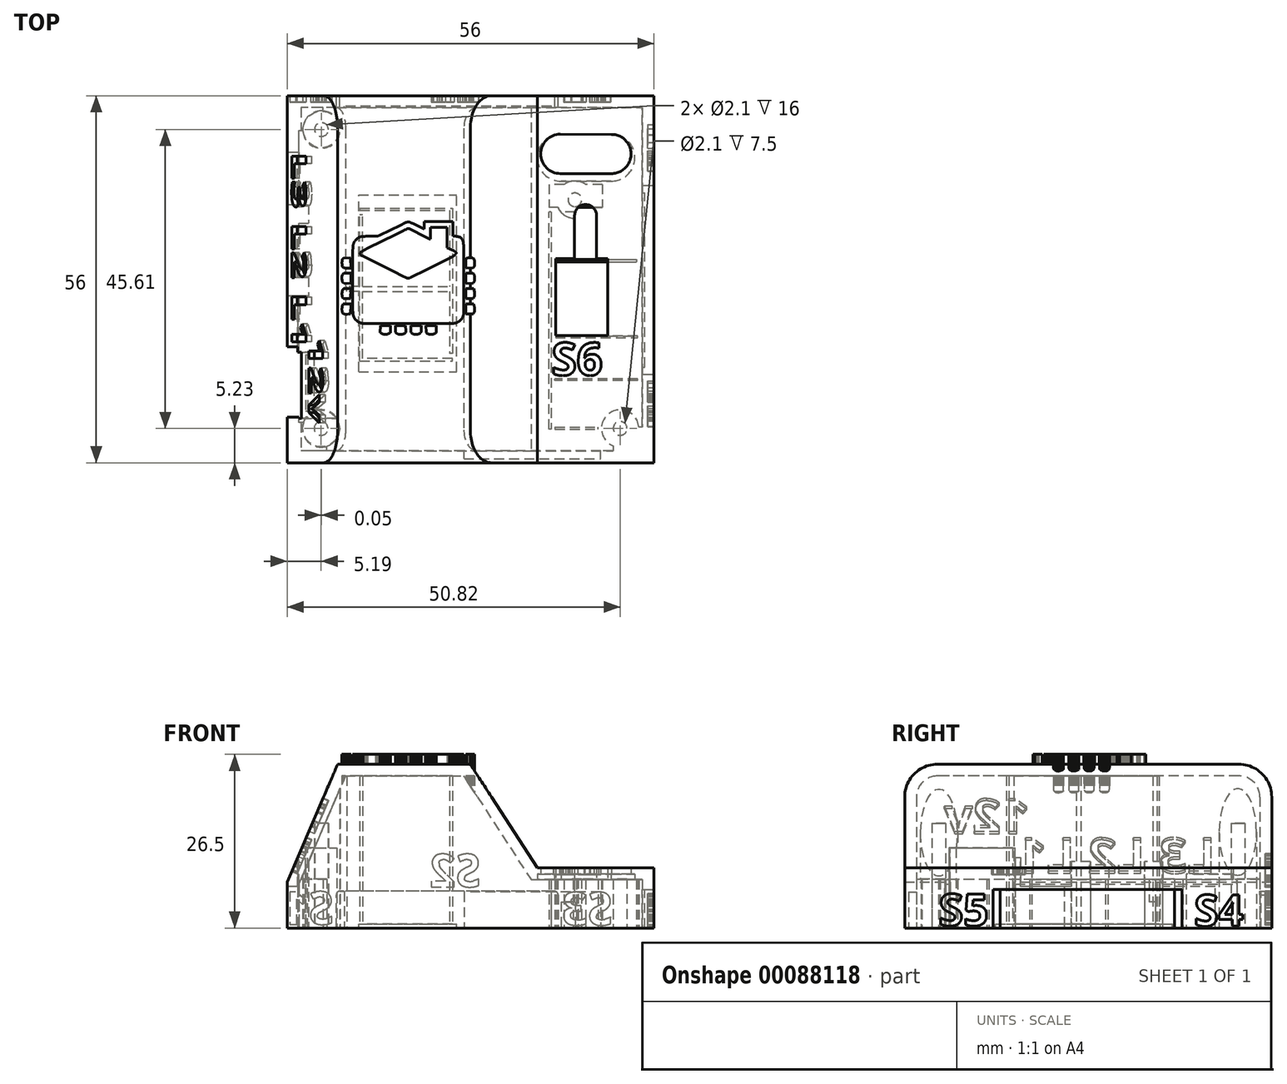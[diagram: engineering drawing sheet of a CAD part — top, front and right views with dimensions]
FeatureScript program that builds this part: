
annotation { "Feature Type Name" : "Feature", "Feature Type Description" : "" }
export const myFeature = defineFeature(function(context is Context, id is Id, definition is map)
    precondition{}
    {
        {
            var Q0;
            Q0=qCreatedBy(makeId("Top.planeOp"),FACE);
            var sketch = newSketch(context, id + "F0", { "sketchPlane" : qUnion([Q0])});
            skLineSegment(sketch, "E0.rect.bottom", {"start": v(22.84, -21.13) * mm, "end": v(-26.83, -21.13) * mm});
            skLineSegment(sketch, "E0.rect.top", {"start": v(22.84, 28.7) * mm, "end": v(-26.83, 28.7) * mm});
            skLineSegment(sketch, "E0.rect.left", {"start": v(22.84, -21.13) * mm, "end": v(22.84, 28.7) * mm});
            skPoint(sketch, "E0.rect.middle", {"position": v(-2, 3.78) * mm});
            skCircle(sketch, "E1", {"center": v(-24.81, -18.99) * mm, "radius": 1.05 * mm});
            skCircle(sketch, "E2", {"center": v(-24.76, 26.62) * mm, "radius": 1.05 * mm});
            skCircle(sketch, "E3", {"center": v(13.92, 15.91) * mm, "radius": 1.05 * mm});
            skLineSegment(sketch, "E4", {"start": v(-2, -21.13) * mm, "end": v(-2, -18.21) * mm});
            skCircle(sketch, "E5.MirrorC", {"center": v(20.82, -18.99) * mm, "radius": 1.05 * mm});
            skLineSegment(sketch, "E6.rect.bottom", {"start": v(24.75, -22.97) * mm, "end": v(-28.75, -22.97) * mm});
            skLineSegment(sketch, "E6.rect.top", {"start": v(24.75, 30.53) * mm, "end": v(-28.75, 30.53) * mm});
            skLineSegment(sketch, "E6.rect.left", {"start": v(24.75, -22.97) * mm, "end": v(24.75, 30.53) * mm});
            skLineSegment(sketch, "E6.rect.right", {"start": v(-28.75, -22.97) * mm, "end": v(-28.75, 30.53) * mm});
            skLineSegment(sketch, "E7.rect.bottom", {"start": v(26, -24.22) * mm, "end": v(-30, -24.22) * mm});
            skLineSegment(sketch, "E7.rect.top", {"start": v(26, 31.78) * mm, "end": v(-30, 31.78) * mm});
            skLineSegment(sketch, "E7.rect.left", {"start": v(26, -24.22) * mm, "end": v(26, 31.78) * mm});
            skLineSegment(sketch, "E7.rect.right", {"start": v(-30, -24.22) * mm, "end": v(-30, 31.78) * mm});
            skPoint(sketch, "E8", {"position": v(8.65, 14) * mm});
            skSolve(sketch);
        }
        {
            var Q0;
            Q0=qSketchRegion(id+"F0",true);
            var Q1;
            Q1=makeQuery(id+"F0.imprint","IMPRINT",FACE,{"disambiguationData":[TD([[makeQuery(id+"F0.imprint","IMPRINT",EDGE,{"derivedFrom":sQuery(id+"F0.wireOp",EDGE,"E1")}),-1.0]])]});
            extrude(context, id + "F1", {"entities" : qUnion([Q0, Q1]), "depth" : 25 * mm});
        }
        {
            var Q0;
            Q0=qCreatedBy(makeId("Front.planeOp"),FACE);
            var sketch = newSketch(context, id + "F2", { "sketchPlane" : qUnion([Q0])});
            skLineSegment(sketch, "E9", {"start": v(0, 0) * mm, "end": v(0, 7) * mm});
            skLineSegment(sketch, "E10", {"start": v(0, 7) * mm, "end": v(26.03, 7) * mm});
            skLineSegment(sketch, "E11", {"start": v(26.03, 9.19) * mm, "end": v(26.03, 25.51) * mm});
            skLineSegment(sketch, "E12", {"start": v(15.3, 7) * mm, "end": v(26.03, 7) * mm});
            skLineSegment(sketch, "E13", {"start": v(0, 7) * mm, "end": v(-30.02, 7) * mm});
            skLineSegment(sketch, "E14", {"start": v(-30.02, 7) * mm, "end": v(-22.06, 25.51) * mm});
            skLineSegment(sketch, "E15", {"start": v(-22.06, 25.51) * mm, "end": v(-2.39, 25.51) * mm});
            skLineSegment(sketch, "E16", {"start": v(26.03, 25.51) * mm, "end": v(-2.39, 25.51) * mm});
            skLineSegment(sketch, "E17", {"start": v(-22.06, 25.51) * mm, "end": v(-30.02, 25.51) * mm});
            skLineSegment(sketch, "E18", {"start": v(-30.02, 25.51) * mm, "end": v(-30.02, 7) * mm});
            skLineSegment(sketch, "E19", {"start": v(18.06, 10.7) * mm, "end": v(18.04, 10.7) * mm});
            skLineSegment(sketch, "E20", {"start": v(19.86, 9.19) * mm, "end": v(8.2, 9.19) * mm});
            skLineSegment(sketch, "E21", {"start": v(8.2, 9.19) * mm, "end": v(-2.39, 25.51) * mm});
            skLineSegment(sketch, "E22", {"start": v(19.86, 9.19) * mm, "end": v(26.03, 9.19) * mm});
            skSolve(sketch);
        }
        {
            var Q0;
            Q0=makeQuery(id+"F2.imprint","IMPRINT",FACE,{"disambiguationData":[TD([[makeQuery(id+"F2.imprint","IMPRINT",EDGE,{"derivedFrom":sQuery(id+"F2.wireOp",EDGE,"E14")}),1.0]])]});
            var Q1;
            {var subQ0=sQuery(id+"F2.wireOp",EDGE,"E11");Q1=makeQuery(id+"F2.imprint","IMPRINT",FACE,{"disambiguationData":[TD([[makeQuery(id+"F2.imprint","IMPRINT",EDGE,{"derivedFrom":subQ0}),1.0]])]});}
            extrude(context, id + "F3", {"entities" : qUnion([Q0, Q1]), "operationType" : NewBodyOperationType.REMOVE, "endBound" : BoundingType.UP_TO_NEXT, "oppositeDirection" : true, "depth" : 25 * mm, "hasSecondDirection" : true, "secondDirectionOppositeDirection" : false, "secondDirectionDepth" : 25 * mm});
        }
        {
            var Q0;
            Q0=makeQuery(id+"F1.opExtrude","CAP_EDGE",EDGE,{"disambiguationData":[OSD([sQuery(id+"F0.wireOp",EDGE,"E7.rect.right")])],"isStart":false});
            var Q1;
            Q1=makeQuery(id+"F3.boolean.opBoolean","COPY",EDGE,{"derivedFrom":makeQuery(id+"F3.opExtrude","TWEAK_EDGE",EDGE,{"derivedFrom":[makeQuery(id+"F1.opExtrude","CAP_FACE",FACE,{"disambiguationData":[OSD([sQuery(id+"F0.wireOp",EDGE,"E1"),sQuery(id+"F0.wireOp",EDGE,"E2"),sQuery(id+"F0.wireOp",EDGE,"E3"),sQuery(id+"F0.wireOp",EDGE,"E5.MirrorC"),sQuery(id+"F0.wireOp",EDGE,"E7.rect.bottom"),sQuery(id+"F0.wireOp",EDGE,"E7.rect.top"),sQuery(id+"F0.wireOp",EDGE,"E7.rect.left"),sQuery(id+"F0.wireOp",EDGE,"E7.rect.right")])],"isStart":false}),makeQuery(id+"F2.imprint","IMPRINT",EDGE,{"derivedFrom":sQuery(id+"F2.wireOp",EDGE,"ff17f17f-c23f-4b7b-92e3-773d52701edb")})]})});
            var Q2;
            Q2=makeQuery(id+"F3.boolean.opBoolean","COPY",EDGE,{"derivedFrom":makeQuery(id+"F3.opExtrude","TWEAK_EDGE",EDGE,{"derivedFrom":[makeQuery(id+"F1.opExtrude","CAP_FACE",FACE,{"disambiguationData":[OSD([sQuery(id+"F0.wireOp",EDGE,"E1"),sQuery(id+"F0.wireOp",EDGE,"E2"),sQuery(id+"F0.wireOp",EDGE,"E3"),sQuery(id+"F0.wireOp",EDGE,"E5.MirrorC"),sQuery(id+"F0.wireOp",EDGE,"E7.rect.bottom"),sQuery(id+"F0.wireOp",EDGE,"E7.rect.top"),sQuery(id+"F0.wireOp",EDGE,"E7.rect.left"),sQuery(id+"F0.wireOp",EDGE,"E7.rect.right")])],"isStart":false}),makeQuery(id+"F2.imprint","IMPRINT",EDGE,{"derivedFrom":sQuery(id+"F2.wireOp",EDGE,"7c30f75c-de24-4105-9ec6-0528e7197d9e")})]})});
            var Q3;
            {var subQ0=sQuery(id+"F2.wireOp",EDGE,"cpQ2IQLn-lepx-jHqE-Occg-QwCyzWVKbBFz");var subQ1=sQuery(id+"F2.wireOp",EDGE,"9136473a-ce9f-4df1-8e41-d79c079f6f02");var subQ2=makeQuery(id+"F2.imprint","INTERSECT",VERTEX,{"disambiguationData":[OD(0.0)],"derivedFrom":[subQ1,subQ0]});var subQ4=makeQuery(id+"F2.imprint","INTERSECT",VERTEX,{"disambiguationData":[OD(1.0)],"derivedFrom":[subQ1,subQ0]});Q3=makeQuery(id+"F3.boolean.opBoolean","COPY",EDGE,{"derivedFrom":makeQuery(id+"F3.opExtrude","TWEAK_EDGE",EDGE,{"derivedFrom":[makeQuery(id+"F1.opExtrude","CAP_FACE",FACE,{"disambiguationData":[OSD([sQuery(id+"F0.wireOp",EDGE,"E1"),sQuery(id+"F0.wireOp",EDGE,"E2"),sQuery(id+"F0.wireOp",EDGE,"E3"),sQuery(id+"F0.wireOp",EDGE,"E5.MirrorC"),sQuery(id+"F0.wireOp",EDGE,"E7.rect.bottom"),sQuery(id+"F0.wireOp",EDGE,"E7.rect.top"),sQuery(id+"F0.wireOp",EDGE,"E7.rect.left"),sQuery(id+"F0.wireOp",EDGE,"E7.rect.right")])],"isStart":false}),makeQuery(id+"F2.imprint","IMPRINT",EDGE,{"disambiguationData":[TD([[subQ4,1.0]])],"derivedFrom":subQ0}),makeQuery(id+"F2.imprint","IMPRINT",EDGE,{"disambiguationData":[TD([[subQ2,1.0]])],"derivedFrom":subQ0}),makeQuery(id+"F2.imprint","IMPRINT",EDGE,{"disambiguationData":[TD([[subQ2,-1.0]])],"derivedFrom":subQ0})]})});}
            var Q4;
            {var subQ0=sQuery(id+"F2.wireOp",EDGE,"cpQ2IQLn-lepx-jHqE-Occg-QwCyzWVKbBFz");var subQ1=sQuery(id+"F2.wireOp",EDGE,"9136473a-ce9f-4df1-8e41-d79c079f6f02");var subQ2=makeQuery(id+"F2.imprint","INTERSECT",VERTEX,{"disambiguationData":[OD(0.0)],"derivedFrom":[subQ1,subQ0]});var subQ3=sQuery(id+"F2.wireOp",EDGE,"7c30f75c-de24-4105-9ec6-0528e7197d9e");var subQ4=makeQuery(id+"F2.imprint","INTERSECT",VERTEX,{"derivedFrom":[subQ3,subQ0]});var subQ5=makeQuery(id+"F2.imprint","INTERSECT",VERTEX,{"disambiguationData":[OD(1.0)],"derivedFrom":[subQ1,subQ0]});Q4=makeQuery(id+"F3.boolean.opBoolean","COPY",EDGE,{"derivedFrom":makeQuery(id+"F3.opExtrude","TWEAK_EDGE",EDGE,{"disambiguationData":[OD(0.0)],"derivedFrom":[makeQuery(id+"F2.imprint","IMPRINT",EDGE,{"disambiguationData":[TD([[subQ4,1.0]])],"derivedFrom":subQ3}),makeQuery(id+"F2.imprint","IMPRINT",EDGE,{"disambiguationData":[TD([[subQ5,1.0]])],"derivedFrom":subQ0}),makeQuery(id+"F2.imprint","IMPRINT",EDGE,{"disambiguationData":[TD([[subQ2,1.0]])],"derivedFrom":subQ0}),makeQuery(id+"F2.imprint","IMPRINT",EDGE,{"disambiguationData":[TD([[subQ2,-1.0]])],"derivedFrom":subQ0})]})});}
            var Q5;
            {var subQ0=sQuery(id+"F2.wireOp",EDGE,"cpQ2IQLn-lepx-jHqE-Occg-QwCyzWVKbBFz");var subQ1=sQuery(id+"F2.wireOp",EDGE,"9136473a-ce9f-4df1-8e41-d79c079f6f02");var subQ2=makeQuery(id+"F2.imprint","INTERSECT",VERTEX,{"disambiguationData":[OD(0.0)],"derivedFrom":[subQ1,subQ0]});var subQ3=sQuery(id+"F2.wireOp",EDGE,"7c30f75c-de24-4105-9ec6-0528e7197d9e");var subQ4=makeQuery(id+"F2.imprint","INTERSECT",VERTEX,{"derivedFrom":[subQ3,subQ0]});var subQ5=makeQuery(id+"F2.imprint","INTERSECT",VERTEX,{"disambiguationData":[OD(1.0)],"derivedFrom":[subQ1,subQ0]});Q5=makeQuery(id+"F3.boolean.opBoolean","COPY",EDGE,{"derivedFrom":makeQuery(id+"F3.opExtrude","TWEAK_EDGE",EDGE,{"disambiguationData":[OD(1.0)],"derivedFrom":[makeQuery(id+"F2.imprint","IMPRINT",EDGE,{"disambiguationData":[TD([[subQ4,1.0]])],"derivedFrom":subQ3}),makeQuery(id+"F2.imprint","IMPRINT",EDGE,{"disambiguationData":[TD([[subQ5,1.0]])],"derivedFrom":subQ0}),makeQuery(id+"F2.imprint","IMPRINT",EDGE,{"disambiguationData":[TD([[subQ2,1.0]])],"derivedFrom":subQ0}),makeQuery(id+"F2.imprint","IMPRINT",EDGE,{"disambiguationData":[TD([[subQ2,-1.0]])],"derivedFrom":subQ0})]})});}
            var Q6;
            Q6=makeQuery(id+"F1.opExtrude","CAP_EDGE",EDGE,{"disambiguationData":[OSD([sQuery(id+"F0.wireOp",EDGE,"E7.rect.bottom")])],"isStart":false});
            var Q7;
            {var subQ0=sQuery(id+"F2.wireOp",EDGE,"cpQ2IQLn-lepx-jHqE-Occg-QwCyzWVKbBFz");var subQ1=sQuery(id+"F2.wireOp",EDGE,"9136473a-ce9f-4df1-8e41-d79c079f6f02");var subQ2=makeQuery(id+"F2.imprint","INTERSECT",VERTEX,{"disambiguationData":[OD(0.0)],"derivedFrom":[subQ1,subQ0]});var subQ4=makeQuery(id+"F2.imprint","INTERSECT",VERTEX,{"disambiguationData":[OD(1.0)],"derivedFrom":[subQ1,subQ0]});Q7=makeQuery(id+"F3.boolean.opBoolean","COPY",EDGE,{"derivedFrom":makeQuery(id+"F3.opExtrude","TWEAK_EDGE",EDGE,{"derivedFrom":[makeQuery(id+"F1.opExtrude","SWEPT_FACE",FACE,{"disambiguationData":[OSD([sQuery(id+"F0.wireOp",EDGE,"E7.rect.bottom")])]}),makeQuery(id+"F2.imprint","IMPRINT",EDGE,{"disambiguationData":[TD([[subQ4,1.0]])],"derivedFrom":subQ0}),makeQuery(id+"F2.imprint","IMPRINT",EDGE,{"disambiguationData":[TD([[subQ2,1.0]])],"derivedFrom":subQ0}),makeQuery(id+"F2.imprint","IMPRINT",EDGE,{"disambiguationData":[TD([[subQ2,-1.0]])],"derivedFrom":subQ0})]})});}
            var Q8;
            Q8=makeQuery(id+"F1.opExtrude","CAP_EDGE",EDGE,{"disambiguationData":[OSD([sQuery(id+"F0.wireOp",EDGE,"E7.rect.top")])],"isStart":false});
            var Q9;
            {var subQ0=sQuery(id+"F2.wireOp",EDGE,"cpQ2IQLn-lepx-jHqE-Occg-QwCyzWVKbBFz");var subQ1=sQuery(id+"F2.wireOp",EDGE,"9136473a-ce9f-4df1-8e41-d79c079f6f02");var subQ2=makeQuery(id+"F2.imprint","INTERSECT",VERTEX,{"disambiguationData":[OD(0.0)],"derivedFrom":[subQ1,subQ0]});var subQ4=makeQuery(id+"F2.imprint","INTERSECT",VERTEX,{"disambiguationData":[OD(1.0)],"derivedFrom":[subQ1,subQ0]});Q9=makeQuery(id+"F3.boolean.opBoolean","COPY",EDGE,{"derivedFrom":makeQuery(id+"F3.opExtrude","TWEAK_EDGE",EDGE,{"derivedFrom":[makeQuery(id+"F1.opExtrude","SWEPT_FACE",FACE,{"disambiguationData":[OSD([sQuery(id+"F0.wireOp",EDGE,"E7.rect.top")])]}),makeQuery(id+"F2.imprint","IMPRINT",EDGE,{"disambiguationData":[TD([[subQ4,1.0]])],"derivedFrom":subQ0}),makeQuery(id+"F2.imprint","IMPRINT",EDGE,{"disambiguationData":[TD([[subQ2,1.0]])],"derivedFrom":subQ0}),makeQuery(id+"F2.imprint","IMPRINT",EDGE,{"disambiguationData":[TD([[subQ2,-1.0]])],"derivedFrom":subQ0})]})});}
            var Q10;
            Q10=makeQuery(id+"F3.boolean.opBoolean","COPY",EDGE,{"derivedFrom":makeQuery(id+"F3.opExtrude","TWEAK_EDGE",EDGE,{"derivedFrom":[makeQuery(id+"F1.opExtrude","CAP_FACE",FACE,{"disambiguationData":[OSD([sQuery(id+"F0.wireOp",EDGE,"E1"),sQuery(id+"F0.wireOp",EDGE,"E2"),sQuery(id+"F0.wireOp",EDGE,"E3"),sQuery(id+"F0.wireOp",EDGE,"E5.MirrorC"),sQuery(id+"F0.wireOp",EDGE,"E7.rect.bottom"),sQuery(id+"F0.wireOp",EDGE,"E7.rect.top"),sQuery(id+"F0.wireOp",EDGE,"E7.rect.left"),sQuery(id+"F0.wireOp",EDGE,"E7.rect.right")])],"isStart":false}),makeQuery(id+"F2.imprint","IMPRINT",EDGE,{"derivedFrom":sQuery(id+"F2.wireOp",EDGE,"99fa5713-44e2-4710-8a3e-a5a5802f03ed")})]})});
            var Q11;
            Q11=makeQuery(id+"F3.boolean.opBoolean","COPY",EDGE,{"derivedFrom":makeQuery(id+"F3.opExtrude","TWEAK_EDGE",EDGE,{"derivedFrom":[makeQuery(id+"F1.opExtrude","CAP_FACE",FACE,{"disambiguationData":[OSD([sQuery(id+"F0.wireOp",EDGE,"E1"),sQuery(id+"F0.wireOp",EDGE,"E2"),sQuery(id+"F0.wireOp",EDGE,"E3"),sQuery(id+"F0.wireOp",EDGE,"E5.MirrorC"),sQuery(id+"F0.wireOp",EDGE,"E7.rect.bottom"),sQuery(id+"F0.wireOp",EDGE,"E7.rect.top"),sQuery(id+"F0.wireOp",EDGE,"E7.rect.left"),sQuery(id+"F0.wireOp",EDGE,"E7.rect.right")])],"isStart":false}),makeQuery(id+"F2.imprint","IMPRINT",EDGE,{"derivedFrom":sQuery(id+"F2.wireOp",EDGE,"E14")})]})});
            var Q12;
            Q12=makeQuery(id+"F3.boolean.opBoolean","COPY",EDGE,{"derivedFrom":makeQuery(id+"F3.opExtrude","TWEAK_EDGE",EDGE,{"derivedFrom":[makeQuery(id+"F1.opExtrude","CAP_FACE",FACE,{"disambiguationData":[OSD([sQuery(id+"F0.wireOp",EDGE,"E1"),sQuery(id+"F0.wireOp",EDGE,"E2"),sQuery(id+"F0.wireOp",EDGE,"E3"),sQuery(id+"F0.wireOp",EDGE,"E5.MirrorC"),sQuery(id+"F0.wireOp",EDGE,"E7.rect.bottom"),sQuery(id+"F0.wireOp",EDGE,"E7.rect.top"),sQuery(id+"F0.wireOp",EDGE,"E7.rect.left"),sQuery(id+"F0.wireOp",EDGE,"E7.rect.right")])],"isStart":false}),makeQuery(id+"F2.imprint","IMPRINT",EDGE,{"derivedFrom":sQuery(id+"F2.wireOp",EDGE,"E21")})]})});
            var Q13;
            Q13=makeQuery(id+"F3.boolean.opBoolean","COPY",EDGE,{"derivedFrom":makeQuery(id+"F3.opExtrude","TWEAK_EDGE",EDGE,{"derivedFrom":[makeQuery(id+"F2.imprint","IMPRINT",EDGE,{"derivedFrom":sQuery(id+"F2.wireOp",EDGE,"E20")}),makeQuery(id+"F2.imprint","IMPRINT",EDGE,{"derivedFrom":sQuery(id+"F2.wireOp",EDGE,"E21")})]})});
            var Q14;
            Q14=makeQuery(id+"F3.boolean.opBoolean","COPY",EDGE,{"derivedFrom":makeQuery(id+"F3.opExtrude","TWEAK_EDGE",EDGE,{"derivedFrom":[makeQuery(id+"F1.opExtrude","SWEPT_FACE",FACE,{"disambiguationData":[OSD([sQuery(id+"F0.wireOp",EDGE,"E7.rect.bottom")])]}),makeQuery(id+"F2.imprint","IMPRINT",EDGE,{"derivedFrom":sQuery(id+"F2.wireOp",EDGE,"E21")})]})});
            var Q15;
            Q15=makeQuery(id+"F3.boolean.opBoolean","COPY",EDGE,{"derivedFrom":makeQuery(id+"F3.opExtrude","TWEAK_EDGE",EDGE,{"derivedFrom":[makeQuery(id+"F1.opExtrude","SWEPT_FACE",FACE,{"disambiguationData":[OSD([sQuery(id+"F0.wireOp",EDGE,"E7.rect.top")])]}),makeQuery(id+"F2.imprint","IMPRINT",EDGE,{"derivedFrom":sQuery(id+"F2.wireOp",EDGE,"E21")})]})});
            var Q16;
            Q16=makeQuery(id+"F3.boolean.opBoolean","COPY",EDGE,{"derivedFrom":makeQuery(id+"F3.opExtrude","TWEAK_EDGE",EDGE,{"derivedFrom":[makeQuery(id+"F1.opExtrude","SWEPT_FACE",FACE,{"disambiguationData":[OSD([sQuery(id+"F0.wireOp",EDGE,"E7.rect.left")])]}),makeQuery(id+"F2.imprint","IMPRINT",EDGE,{"derivedFrom":sQuery(id+"F2.wireOp",EDGE,"E20")}),makeQuery(id+"F2.imprint","IMPRINT",EDGE,{"derivedFrom":sQuery(id+"F2.wireOp",EDGE,"E22")})]})});
            var Q17;
            Q17=makeQuery(id+"F3.boolean.opBoolean","COPY",EDGE,{"derivedFrom":makeQuery(id+"F3.opExtrude","TWEAK_EDGE",EDGE,{"derivedFrom":[makeQuery(id+"F2.imprint","IMPRINT",EDGE,{"derivedFrom":sQuery(id+"F2.wireOp",EDGE,"E20")}),makeQuery(id+"F2.imprint","IMPRINT",EDGE,{"derivedFrom":sQuery(id+"F2.wireOp",EDGE,"E21")}),makeQuery(id+"F2.imprint","IMPRINT",EDGE,{"derivedFrom":sQuery(id+"F2.wireOp",EDGE,"E22")})]})});
            fillet(context, id + "F4", {"entities" : qUnion([Q0, Q1, Q2, Q3, Q4, Q5, Q6, Q7, Q8, Q9, Q10, Q11, Q12, Q13, Q14, Q15, Q16, Q17]), "radius" : 5 * mm, "tangentPropagation" : true, "allowEdgeOverflow" : false});
        }
        {
            var Q0;
            Q0=makeQuery(id+"F1.opExtrude","SWEPT_BODY",BODY,{"disambiguationData":[OSD([sQuery(id+"F0.wireOp",EDGE,"E1"),sQuery(id+"F0.wireOp",EDGE,"E2"),sQuery(id+"F0.wireOp",EDGE,"E3"),sQuery(id+"F0.wireOp",EDGE,"E5.MirrorC"),sQuery(id+"F0.wireOp",EDGE,"E7.rect.bottom"),sQuery(id+"F0.wireOp",EDGE,"E7.rect.top"),sQuery(id+"F0.wireOp",EDGE,"E7.rect.left"),sQuery(id+"F0.wireOp",EDGE,"E7.rect.right")])]});
            transform(context, id + "F5", {"entities" : qUnion([Q0]), "transformType" : TransformType.TRANSLATION_3D, "dx" : -5 * mm, "dy" : -12 * mm, "dz" : 0 * mm, "makeCopy" : false});
        }
        {
            var Q0;
            Q0=makeQuery(id+"F1.opExtrude","CAP_FACE",FACE,{"disambiguationData":[OSD([sQuery(id+"F0.wireOp",EDGE,"E1"),sQuery(id+"F0.wireOp",EDGE,"E2"),sQuery(id+"F0.wireOp",EDGE,"E3"),sQuery(id+"F0.wireOp",EDGE,"E5.MirrorC"),sQuery(id+"F0.wireOp",EDGE,"E7.rect.bottom"),sQuery(id+"F0.wireOp",EDGE,"E7.rect.top"),sQuery(id+"F0.wireOp",EDGE,"E7.rect.left"),sQuery(id+"F0.wireOp",EDGE,"E7.rect.right")])],"isStart":true});
            shell(context, id + "F6", {"entities" : qUnion([Q0]), "thickness" : 1.8 * mm});
        }
        {
            var Q0;
            Q0=makeQuery(id+"F1.opExtrude","SWEPT_FACE",FACE,{"disambiguationData":[OSD([sQuery(id+"F0.wireOp",EDGE,"E7.rect.left")])]});
            cPlane(context, id + "F7", {"entities" : qUnion([Q0]), "cplaneType" : CPlaneType.OFFSET, "offset" : 0 * mm, "width" : 150 * mm, "height" : 150 * mm});
        }
        {
            var Q0;
            Q0=qCreatedBy(id+"F7.planeOp",FACE);
            var sketch = newSketch(context, id + "F8", { "sketchPlane" : qUnion([Q0])});
            skLineSegment(sketch, "E23.bottom", {"start": v(6.92, 0) * mm, "end": v(-20.2, 0) * mm});
            skLineSegment(sketch, "E23.top", {"start": v(6.12, 5.87) * mm, "end": v(-20.2, 5.87) * mm});
            skLineSegment(sketch, "E24", {"start": v(-20.2, 5.87) * mm, "end": v(-21.64, 5.87) * mm});
            skLineSegment(sketch, "E25", {"start": v(-21.64, 5.87) * mm, "end": v(-21.64, 0) * mm});
            skLineSegment(sketch, "E26", {"start": v(-21.64, 0) * mm, "end": v(-20.2, 0) * mm});
            skLineSegment(sketch, "E27", {"start": v(6.12, 5.87) * mm, "end": v(6.12, 0) * mm});
            skPoint(sketch, "E28.orphan", {"position": v(7.84, 0) * mm});
            skLineSegment(sketch, "E29", {"start": v(4.97, 0) * mm, "end": v(4.97, 5.87) * mm});
            skLineSegment(sketch, "E30", {"start": v(-21.64, 5.87) * mm, "end": v(-22.73, 5.87) * mm});
            skLineSegment(sketch, "E31", {"start": v(-22.73, 5.87) * mm, "end": v(-22.73, 0) * mm});
            skLineSegment(sketch, "E32", {"start": v(-22.73, 0) * mm, "end": v(-21.64, 0) * mm});
            skSolve(sketch);
        }
        {
            var Q0;
            {var subQ1=sQuery(id+"F8.wireOp",EDGE,"E24");Q0=makeQuery(id+"F8.imprint","IMPRINT",FACE,{"disambiguationData":[TD([[makeQuery(id+"F8.imprint","IMPRINT",EDGE,{"derivedFrom":subQ1}),1.0]])]});}
            extrude(context, id + "F9", {"entities" : qUnion([Q0]), "operationType" : NewBodyOperationType.REMOVE, "oppositeDirection" : true, "depth" : (1.7 - 0.3) * mm});
        }
        {
            var Q0;
            Q0=makeQuery(id+"F8.imprint","IMPRINT",FACE,{"disambiguationData":[TD([[makeQuery(id+"F8.imprint","IMPRINT",EDGE,{"derivedFrom":sQuery(id+"F8.wireOp",EDGE,"E25")}),-1.0]])]});
            var Q1;
            {var subQ0=sQuery(id+"F8.wireOp",EDGE,"E27");Q1=makeQuery(id+"F8.imprint","IMPRINT",FACE,{"disambiguationData":[TD([[makeQuery(id+"F8.imprint","IMPRINT",EDGE,{"derivedFrom":subQ0}),-1.0]])]});}
            extrude(context, id + "F10", {"entities" : qUnion([Q0, Q1]), "operationType" : NewBodyOperationType.REMOVE, "oppositeDirection" : true, "depth" : 2 * mm});
        }
        {
            var Q0;
            Q0=makeQuery(id+"F1.opExtrude","SWEPT_FACE",FACE,{"disambiguationData":[OSD([sQuery(id+"F0.wireOp",EDGE,"E7.rect.right")])]});
            cPlane(context, id + "F11", {"entities" : qUnion([Q0]), "cplaneType" : CPlaneType.OFFSET, "offset" : 0 * mm, "width" : 150 * mm, "height" : 150 * mm});
        }
        {
            var Q0;
            Q0=qCreatedBy(id+"F11.planeOp",FACE);
            var sketch = newSketch(context, id + "F12", { "sketchPlane" : qUnion([Q0])});
            skLineSegment(sketch, "E33.top", {"start": v(-11.15, 6.31) * mm, "end": v(-3.45, 6.31) * mm});
            skLineSegment(sketch, "E34", {"start": v(27.25, 11.15) * mm, "end": v(27.25, 11.15) * mm});
            skLineSegment(sketch, "E35", {"start": v(-11.15, 0) * mm, "end": v(-11.15, 6.31) * mm});
            skPoint(sketch, "E36.start.orphan", {"position": v(-15.15, 0) * mm});
            skLineSegment(sketch, "E37", {"start": v(29.28, 0) * mm, "end": v(-11.15, 0) * mm});
            skLineSegment(sketch, "E38", {"start": v(-10.29, 6.31) * mm, "end": v(-10.29, 0) * mm});
            skLineSegment(sketch, "E39", {"start": v(19.35, 12.2) * mm, "end": v(29.28, 12.2) * mm});
            skLineSegment(sketch, "E40", {"start": v(-11.15, 3.16) * mm, "end": v(-3.45, 3.16) * mm, "construction": true});
            skLineSegment(sketch, "E41", {"start": v(-3.45, 3.16) * mm, "end": v(-0.05, 3.16) * mm, "construction": true});
            skLineSegment(sketch, "E42", {"start": v(-0.05, 3.16) * mm, "end": v(7.65, 3.16) * mm, "construction": true});
            skLineSegment(sketch, "E43", {"start": v(7.65, 3.16) * mm, "end": v(11.05, 3.16) * mm, "construction": true});
            skLineSegment(sketch, "E44.trimOffspring", {"start": v(11.05, 6.31) * mm, "end": v(18.53, 6.31) * mm});
            skLineSegment(sketch, "E45", {"start": v(11.9, 6.31) * mm, "end": v(11.9, 0) * mm});
            skLineSegment(sketch, "E46", {"start": v(0, 6.31) * mm, "end": v(7.65, 6.31) * mm});
            skLineSegment(sketch, "E47", {"start": v(7.65, 0) * mm, "end": v(0, 0) * mm});
            skLineSegment(sketch, "E48", {"start": v(-3.45, 0) * mm, "end": v(-11.15, 0) * mm});
            skLineSegment(sketch, "E49", {"start": v(30.08, 0) * mm, "end": v(11.05, 0) * mm});
            skLineSegment(sketch, "E50.bottom", {"start": v(-0.32, 0) * mm, "end": v(-3.15, 0) * mm});
            skLineSegment(sketch, "E50.top", {"start": v(-0.32, 6.31) * mm, "end": v(-3.15, 6.31) * mm});
            skLineSegment(sketch, "E50.left", {"start": v(-0.32, 0) * mm, "end": v(-0.32, 6.31) * mm});
            skLineSegment(sketch, "E50.right", {"start": v(-3.15, 0) * mm, "end": v(-3.15, 6.31) * mm});
            skLineSegment(sketch, "E51.bottom", {"start": v(10.8, 0) * mm, "end": v(7.92, 0) * mm});
            skLineSegment(sketch, "E51.top", {"start": v(10.8, 6.31) * mm, "end": v(7.92, 6.31) * mm});
            skLineSegment(sketch, "E51.left", {"start": v(10.8, 0) * mm, "end": v(10.8, 6.31) * mm});
            skLineSegment(sketch, "E51.right", {"start": v(7.92, 0) * mm, "end": v(7.92, 6.31) * mm});
            skLineSegment(sketch, "E52", {"start": v(-3.45, 6.31) * mm, "end": v(11.05, 6.31) * mm});
            skLineSegment(sketch, "E53", {"start": v(29.28, 12.2) * mm, "end": v(29.28, 0) * mm});
            skPoint(sketch, "E54.end.orphan", {"position": v(30.08, 11.15) * mm});
            skPoint(sketch, "E54.start.orphan", {"position": v(30.08, 12.2) * mm});
            skLineSegment(sketch, "E55", {"start": v(18.53, 6.31) * mm, "end": v(18.53, 12.2) * mm});
            skLineSegment(sketch, "E56", {"start": v(18.53, 12.2) * mm, "end": v(19.35, 12.2) * mm});
            skPoint(sketch, "E57.start.orphan", {"position": v(19.35, 11.15) * mm});
            skPoint(sketch, "E58.end.orphan", {"position": v(19.35, 0) * mm});
            skPoint(sketch, "E58.start.orphan", {"position": v(19.35, 6.31) * mm});
            skLineSegment(sketch, "E59", {"start": v(28.38, 0) * mm, "end": v(28.38, 12.2) * mm});
            skLineSegment(sketch, "E60", {"start": v(19.35, 12.2) * mm, "end": v(19.35, 0) * mm});
            skSolve(sketch);
        }
        {
            var Q0;
            {var subQ0=sQuery(id+"F12.wireOp",EDGE,"E35");Q0=makeQuery(id+"F12.imprint","IMPRINT",FACE,{"disambiguationData":[TD([[makeQuery(id+"F12.imprint","IMPRINT",EDGE,{"derivedFrom":subQ0}),-1.0]])]});}
            var Q1;
            {var subQ1=sQuery(id+"F12.wireOp",EDGE,"E38");Q1=makeQuery(id+"F12.imprint","IMPRINT",FACE,{"disambiguationData":[TD([[makeQuery(id+"F12.imprint","IMPRINT",EDGE,{"derivedFrom":subQ1}),1.0]])]});}
            var Q2;
            {var subQ0=sQuery(id+"F12.wireOp",EDGE,"LVVauTd6-uSLQ-SWm0-nvuu-HrEgJgk2loCY");Q2=makeQuery(id+"F12.imprint","IMPRINT",FACE,{"disambiguationData":[TD([[makeQuery(id+"F12.imprint","IMPRINT",EDGE,{"derivedFrom":subQ0}),-1.0]])]});}
            var Q3;
            Q3=makeQuery(id+"F12.imprint","IMPRINT",FACE,{"disambiguationData":[TD([[makeQuery(id+"F12.imprint","IMPRINT",EDGE,{"derivedFrom":sQuery(id+"F12.wireOp",EDGE,"Bzj0w9RH-aYdH-ZF7y-Z4mK-Pif1xP8myCSu")}),1.0]])]});
            var Q4;
            {var subQ2=sQuery(id+"F12.wireOp",EDGE,"E45");Q4=makeQuery(id+"F12.imprint","IMPRINT",FACE,{"disambiguationData":[TD([[makeQuery(id+"F12.imprint","IMPRINT",EDGE,{"derivedFrom":subQ2}),1.0]])]});}
            extrude(context, id + "F13", {"entities" : qUnion([Q0, Q1, Q2, Q3, Q4]), "operationType" : NewBodyOperationType.REMOVE, "oppositeDirection" : true, "depth" : 1.6 * mm});
        }
        {
            var Q0;
            {var subQ2=sQuery(id+"F12.wireOp",EDGE,"E59");Q0=makeQuery(id+"F12.imprint","IMPRINT",FACE,{"disambiguationData":[TD([[makeQuery(id+"F12.imprint","IMPRINT",EDGE,{"derivedFrom":subQ2}),1.0]])]});}
            var Q1;
            {var subQ0=sQuery(id+"F12.wireOp",EDGE,"E35");Q1=makeQuery(id+"F12.imprint","IMPRINT",FACE,{"disambiguationData":[TD([[makeQuery(id+"F12.imprint","IMPRINT",EDGE,{"derivedFrom":subQ0}),-1.0]])]});}
            var Q2;
            {var subQ1=sQuery(id+"F12.wireOp",EDGE,"E47");Q2=makeQuery(id+"F12.imprint","IMPRINT",FACE,{"disambiguationData":[TD([[makeQuery(id+"F12.imprint","IMPRINT",EDGE,{"derivedFrom":subQ1}),-1.0]])]});}
            var Q3;
            {var subQ3=sQuery(id+"F12.wireOp",EDGE,"E38");Q3=makeQuery(id+"F12.imprint","IMPRINT",FACE,{"disambiguationData":[TD([[makeQuery(id+"F12.imprint","IMPRINT",EDGE,{"derivedFrom":subQ3}),1.0]])]});}
            var Q4;
            {var subQ3=sQuery(id+"F12.wireOp",EDGE,"E45");Q4=makeQuery(id+"F12.imprint","IMPRINT",FACE,{"disambiguationData":[TD([[makeQuery(id+"F12.imprint","IMPRINT",EDGE,{"derivedFrom":subQ3}),-1.0]])]});}
            var Q5;
            {var subQ0=sQuery(id+"F12.wireOp",EDGE,"E53");Q5=makeQuery(id+"F12.imprint","IMPRINT",FACE,{"disambiguationData":[TD([[makeQuery(id+"F12.imprint","IMPRINT",EDGE,{"derivedFrom":subQ0}),-1.0]])]});}
            extrude(context, id + "F14", {"entities" : qUnion([Q0, Q1, Q2, Q3, Q4, Q5]), "operationType" : NewBodyOperationType.REMOVE, "oppositeDirection" : true, "depth" : 8 * mm});
        }
        {
            var Q0;
            Q0=qCreatedBy(makeId("Top.planeOp"),FACE);
            var sketch = newSketch(context, id + "F15", { "sketchPlane" : qUnion([Q0])});
            skLineSegment(sketch, "E61.bottom", {"start": v(-27.19, -29.45) * mm, "end": v(-33.17, -29.45) * mm});
            skLineSegment(sketch, "E61.top", {"start": v(-27.19, -20) * mm, "end": v(-33.17, -20) * mm});
            skLineSegment(sketch, "E61.left", {"start": v(-27.19, -29.45) * mm, "end": v(-27.19, -21.32) * mm});
            skLineSegment(sketch, "E61.right", {"start": v(-33.17, -29.45) * mm, "end": v(-33.17, -21.32) * mm});
            skLineSegment(sketch, "E62", {"start": v(-33.17, -20.99) * mm, "end": v(-27.19, -20.99) * mm});
            skLineSegment(sketch, "E63", {"start": v(-33.17, -21.32) * mm, "end": v(-27.19, -21.32) * mm});
            skLineSegment(sketch, "E64.trimOffspring", {"start": v(-27.19, -20.99) * mm, "end": v(-27.19, -20) * mm});
            skLineSegment(sketch, "E65.trimOffspring", {"start": v(-33.17, -20.99) * mm, "end": v(-33.17, -20) * mm});
            skSolve(sketch);
        }
        {
            var Q0;
            Q0=qSketchRegion(id+"F15",true);
            var Q1;
            {var subQ0=sQuery(id+"F12.wireOp",EDGE,"E39");Q1=makeQuery(id+"F14.boolean.opBoolean","COPY",FACE,{"derivedFrom":makeQuery(id+"F14.opExtrude","SWEPT_FACE",FACE,{"disambiguationData":[OSD([subQ0]),TDD([makeQuery(id+"F12.imprint","IMPRINT",EDGE,{"disambiguationData":[TD([[makeQuery(id+"F12.imprint","INTERSECT",VERTEX,{"derivedFrom":[subQ0,sQuery(id+"F12.wireOp",EDGE,"E54")]}),1.0]])],"derivedFrom":subQ0})])]})});}
            extrude(context, id + "F16", {"entities" : qUnion([Q0]), "operationType" : NewBodyOperationType.REMOVE, "endBound" : BoundingType.UP_TO_SURFACE, "endBoundEntityFace" : qUnion([Q1]), "depth" : 11.3 * mm});
        }
        {
            var Q0;
            Q0=makeQuery(id+"F1.opExtrude","SWEPT_FACE",FACE,{"disambiguationData":[OSD([sQuery(id+"F0.wireOp",EDGE,"E7.rect.top")])]});
            cPlane(context, id + "F17", {"entities" : qUnion([Q0]), "cplaneType" : CPlaneType.OFFSET, "offset" : 0 * mm, "width" : 150 * mm, "height" : 150 * mm});
        }
        {
            var Q0;
            Q0=qCreatedBy(id+"F17.planeOp",FACE);
            var sketch = newSketch(context, id + "F18", { "sketchPlane" : qUnion([Q0])});
            skLineSegment(sketch, "E66.bottom", {"start": v(-6.36, 0) * mm, "end": v(27.5, 0) * mm});
            skLineSegment(sketch, "E66.left", {"start": v(-6.36, 0) * mm, "end": v(-6.36, 2.05) * mm});
            skLineSegment(sketch, "E67", {"start": v(-5.32, 3.26) * mm, "end": v(-5.32, 0) * mm});
            skLineSegment(sketch, "E68", {"start": v(27.5, 2.61) * mm, "end": v(27.5, 0) * mm});
            skLineSegment(sketch, "E69", {"start": v(26.27, 5.04) * mm, "end": v(26.27, 0) * mm});
            skPoint(sketch, "E70.visualSharp", {"position": v(-6.36, 7.05) * mm});
            skLineSegment(sketch, "E71", {"start": v(24.5, 5.61) * mm, "end": v(-1.9, 5.61) * mm});
            skPoint(sketch, "E72.visualSharp", {"position": v(-3.28, 5.61) * mm});
            skPoint(sketch, "E73.visualSharp", {"position": v(27.5, 5.61) * mm});
            skLineSegment(sketch, "E74", {"start": v(-6.36, 2.05) * mm, "end": v(-6.36, 5.08) * mm});
            skLineSegment(sketch, "E75", {"start": v(-5.83, 5.61) * mm, "end": v(-1.9, 5.61) * mm});
            skPoint(sketch, "E76.visualSharp", {"position": v(-6.36, 5.61) * mm});
            skArc(sketch, "E76.filletArc", {"start": v(-5.83, 5.61) * mm, "mid": v(-6.2, 5.45) * mm, "end": v(-6.36, 5.08) * mm});
            skLineSegment(sketch, "E77", {"start": v(-5.32, 3.26) * mm, "end": v(-5.32, 5.61) * mm});
            skLineSegment(sketch, "E78", {"start": v(24.5, 5.61) * mm, "end": v(26.98, 5.61) * mm});
            skLineSegment(sketch, "E79", {"start": v(27.5, 2.61) * mm, "end": v(27.5, 5.08) * mm});
            skLineSegment(sketch, "E80", {"start": v(26.27, 5.04) * mm, "end": v(26.27, 5.61) * mm});
            skArc(sketch, "E81.filletArc", {"start": v(27.5, 5.08) * mm, "mid": v(27.35, 5.45) * mm, "end": v(26.98, 5.61) * mm});
            skSolve(sketch);
        }
        {
            var Q0;
            Q0=qSketchRegion(id+"F18",true);
            extrude(context, id + "F19", {"entities" : qUnion([Q0]), "operationType" : NewBodyOperationType.REMOVE, "oppositeDirection" : true, "depth" : 1.6 * mm});
        }
        {
            var Q0;
            Q0=qCreatedBy(makeId("Top.planeOp"),FACE);
            var sketch = newSketch(context, id + "F20", { "sketchPlane" : qUnion([Q0])});
            skArc(sketch, "E82", {"start": v(6.16, 2.02) * mm, "mid": v(8.9, 0.56) * mm, "end": v(11.63, 2.02) * mm});
            skLineSegment(sketch, "E83", {"start": v(11.63, 2.02) * mm, "end": v(6.16, 2.02) * mm});
            skSolve(sketch);
        }
        {
            var Q0;
            Q0=qSketchRegion(id+"F20",true);
            extrude(context, id + "F21", {"entities" : qUnion([Q0]), "operationType" : NewBodyOperationType.REMOVE, "depth" : 4 * mm});
        }
        {
            var Q0;
            {var subQ0=sQuery(id+"F18.wireOp",EDGE,"E66.left");Q0=makeQuery(id+"F18.imprint","IMPRINT",FACE,{"disambiguationData":[TD([[makeQuery(id+"F18.imprint","IMPRINT",EDGE,{"derivedFrom":subQ0}),-1.0]])]});}
            var Q1;
            {var subQ0=sQuery(id+"F18.wireOp",EDGE,"E66.right");Q1=makeQuery(id+"F18.imprint","IMPRINT",FACE,{"disambiguationData":[TD([[makeQuery(id+"F18.imprint","IMPRINT",EDGE,{"derivedFrom":subQ0}),1.0]])]});}
            extrude(context, id + "F22", {"entities" : qUnion([Q0, Q1]), "operationType" : NewBodyOperationType.REMOVE, "oppositeDirection" : true, "depth" : 2 * mm});
        }
        {
            var Q0;
            Q0=qCreatedBy(makeId("Top.planeOp"),FACE);
            var sketch = newSketch(context, id + "F23", { "sketchPlane" : qUnion([Q0])});
            skLineSegment(sketch, "E84", {"start": v(21, 19.9) * mm, "end": v(21, 10.4) * mm, "construction": true});
            skLineSegment(sketch, "E85", {"start": v(12.22, 0) * mm, "end": v(12.22, -5.06) * mm});
            skLineSegment(sketch, "E86", {"start": v(12.22, 0) * mm, "end": v(12.22, 1.5) * mm});
            skArc(sketch, "E87", {"start": v(14.47, 7.9) * mm, "mid": v(17.49, 10.88) * mm, "end": v(14.5, 13.88) * mm});
            skArc(sketch, "E88", {"start": v(6.7, 13.9) * mm, "mid": v(3.7, 10.9) * mm, "end": v(6.7, 7.9) * mm});
            skLineSegment(sketch, "E89", {"start": v(14.5, 13.88) * mm, "end": v(6.7, 13.9) * mm});
            skLineSegment(sketch, "E90", {"start": v(6.7, 7.9) * mm, "end": v(14.54, 7.9) * mm});
            skLineSegment(sketch, "E91", {"start": v(6, -5.57) * mm, "end": v(6, -16.85) * mm});
            skLineSegment(sketch, "E92", {"start": v(12.6, -16.85) * mm, "end": v(6, -16.85) * mm});
            skPoint(sketch, "E93.center.orphan", {"position": v(10.72, -16.85) * mm});
            skLineSegment(sketch, "E94", {"start": v(8.87, -5.06) * mm, "end": v(8.87, 1.5) * mm});
            skArc(sketch, "E95", {"start": v(12.22, 1.5) * mm, "mid": v(10.54, 3.17) * mm, "end": v(8.87, 1.5) * mm});
            skPoint(sketch, "E96.orphan", {"position": v(12.22, -16.85) * mm});
            skLineSegment(sketch, "E97", {"start": v(0, 0) * mm, "end": v(0, 19.9) * mm, "construction": true});
            skLineSegment(sketch, "E98", {"start": v(0, 19.9) * mm, "end": v(21, 19.9) * mm, "construction": true});
            skLineSegment(sketch, "E99", {"start": v(14.5, 10.9) * mm, "end": v(21, 10.9) * mm, "construction": true});
            skLineSegment(sketch, "E100", {"start": v(8.87, -5.06) * mm, "end": v(6, -5.06) * mm});
            skLineSegment(sketch, "E101", {"start": v(6, -5.06) * mm, "end": v(6, -5.57) * mm});
            skLineSegment(sketch, "E102", {"start": v(12.22, -5.06) * mm, "end": v(12.6, -5.06) * mm});
            skLineSegment(sketch, "E103", {"start": v(12.6, -16.85) * mm, "end": v(13.95, -16.85) * mm});
            skLineSegment(sketch, "E104", {"start": v(13.95, -16.85) * mm, "end": v(13.95, -5.06) * mm});
            skLineSegment(sketch, "E105", {"start": v(13.95, -5.06) * mm, "end": v(12.6, -5.06) * mm});
            skPoint(sketch, "E106.end.orphan", {"position": v(12.6, -5.57) * mm});
            skSolve(sketch);
        }
        {
            var Q0;
            Q0=qSketchRegion(id+"F23",true);
            extrude(context, id + "F24", {"entities" : qUnion([Q0]), "operationType" : NewBodyOperationType.REMOVE, "depth" : 25 * mm});
        }
        {
            var Q0;
            Q0=qCreatedBy(makeId("Top.planeOp"),FACE);
            var sketch = newSketch(context, id + "F25", { "sketchPlane" : qUnion([Q0])});
            skLineSegment(sketch, "E107", {"start": v(18.49, -17.16) * mm, "end": v(5.97, -17.16) * mm});
            skLineSegment(sketch, "E108", {"start": v(18.49, -16.86) * mm, "end": v(5.97, -16.86) * mm});
            skLineSegment(sketch, "E109", {"start": v(12.44, -31.08) * mm, "end": v(5.87, -31.08) * mm});
            skLineSegment(sketch, "E110", {"start": v(12.44, -30.78) * mm, "end": v(5.87, -30.78) * mm});
            skLineSegment(sketch, "E111.bottom", {"start": v(-33.84, 14.47) * mm, "end": v(-32.16, 14.47) * mm});
            skLineSegment(sketch, "E111.top", {"start": v(-33.84, 18.7) * mm, "end": v(-29.5, 18.7) * mm});
            skLineSegment(sketch, "E111.left", {"start": v(-33.84, 14.47) * mm, "end": v(-33.84, 18.7) * mm});
            skLineSegment(sketch, "E111.right", {"start": v(-29.5, 16.74) * mm, "end": v(-29.5, 18.7) * mm});
            skArc(sketch, "E112", {"start": v(-29.5, 16.74) * mm, "mid": v(-31.35, 16.22) * mm, "end": v(-32.16, 14.47) * mm});
            skLineSegment(sketch, "E113.bottom", {"start": v(-33.6, -31.08) * mm, "end": v(-33.6, -31.08) * mm});
            skLineSegment(sketch, "E113.top", {"start": v(-33.6, -34.81) * mm, "end": v(-31.03, -34.81) * mm});
            skLineSegment(sketch, "E113.left", {"start": v(-33.6, -31.08) * mm, "end": v(-33.6, -34.81) * mm});
            skLineSegment(sketch, "E113.right", {"start": v(-31.03, -31.08) * mm, "end": v(-31.03, -33.21) * mm});
            skLineSegment(sketch, "E114.bottom", {"start": v(-31.03, -34.81) * mm, "end": v(-28.95, -34.81) * mm});
            skLineSegment(sketch, "E114.top", {"start": v(-31.03, -33.21) * mm, "end": v(-28.95, -33.21) * mm});
            skLineSegment(sketch, "E114.right", {"start": v(-28.95, -34.81) * mm, "end": v(-28.95, -33.21) * mm});
            skPoint(sketch, "E115.end.orphan", {"position": v(-34.98, -31.08) * mm});
            skPoint(sketch, "E115.start.orphan", {"position": v(-34.98, -30.78) * mm});
            skLineSegment(sketch, "E116.bottom", {"start": v(16.87, -34.88) * mm, "end": v(19.69, -34.88) * mm});
            skLineSegment(sketch, "E116.top", {"start": v(16.87, -30.79) * mm, "end": v(19.69, -30.79) * mm});
            skLineSegment(sketch, "E116.left", {"start": v(16.87, -33.4) * mm, "end": v(16.87, -30.79) * mm});
            skLineSegment(sketch, "E116.right", {"start": v(19.69, -34.88) * mm, "end": v(19.69, -30.79) * mm});
            skLineSegment(sketch, "E117.bottom", {"start": v(16.87, -34.88) * mm, "end": v(14.73, -34.88) * mm});
            skLineSegment(sketch, "E117.top", {"start": v(16.87, -33.4) * mm, "end": v(14.73, -33.4) * mm});
            skLineSegment(sketch, "E117.right", {"start": v(14.73, -34.88) * mm, "end": v(14.73, -33.4) * mm});
            skLineSegment(sketch, "E118.top", {"start": v(-31.03, -30.09) * mm, "end": v(-33.6, -30.09) * mm});
            skLineSegment(sketch, "E118.left", {"start": v(-31.03, -31.08) * mm, "end": v(-31.03, -30.09) * mm});
            skLineSegment(sketch, "E118.right", {"start": v(-33.6, -31.08) * mm, "end": v(-33.6, -30.09) * mm});
            skLineSegment(sketch, "E119", {"start": v(5.87, -31.08) * mm, "end": v(5.87, -30.78) * mm});
            skPoint(sketch, "E120.end.orphan", {"position": v(-34.98, -17.16) * mm});
            skPoint(sketch, "E120.start.orphan", {"position": v(-34.98, -16.86) * mm});
            skLineSegment(sketch, "E121.trimOffspring", {"start": v(5.97, -17.16) * mm, "end": v(5.97, -16.86) * mm});
            skLineSegment(sketch, "E122.bottom", {"start": v(5.85, -23.4) * mm, "end": v(18.49, -23.4) * mm});
            skLineSegment(sketch, "E122.top", {"start": v(5.85, -23.7) * mm, "end": v(18.49, -23.7) * mm});
            skLineSegment(sketch, "E122.left", {"start": v(5.85, -23.4) * mm, "end": v(5.85, -23.7) * mm});
            skLineSegment(sketch, "E123", {"start": v(5.29, -31.08) * mm, "end": v(5.29, 2.03) * mm});
            skLineSegment(sketch, "E124", {"start": v(4.99, -31.08) * mm, "end": v(5.29, -31.08) * mm});
            skLineSegment(sketch, "E125", {"start": v(12.44, -30.78) * mm, "end": v(12.44, -31.08) * mm});
            skLineSegment(sketch, "E126", {"start": v(18.49, -16.86) * mm, "end": v(18.49, -17.16) * mm});
            skPoint(sketch, "E127.orphan", {"position": v(19.24, -17.16) * mm});
            skLineSegment(sketch, "E128.trimOffspring", {"start": v(18.49, -23.4) * mm, "end": v(18.49, -23.7) * mm});
            skPoint(sketch, "E129.orphan", {"position": v(19.24, -23.7) * mm});
            skLineSegment(sketch, "E130.trimOffspring", {"start": v(4.99, 2.03) * mm, "end": v(4.99, -31.08) * mm});
            skLineSegment(sketch, "E131", {"start": v(4.99, 2.03) * mm, "end": v(5.29, 2.03) * mm});
            skLineSegment(sketch, "E132.bottom", {"start": v(4.99, 2.73) * mm, "end": v(13.12, 2.73) * mm});
            skLineSegment(sketch, "E132.top", {"start": v(4.99, 6.24) * mm, "end": v(13.12, 6.24) * mm});
            skLineSegment(sketch, "E132.left", {"start": v(4.99, 2.73) * mm, "end": v(4.99, 6.24) * mm});
            skLineSegment(sketch, "E132.right", {"start": v(13.12, 2.73) * mm, "end": v(13.12, 6.24) * mm});
            skCircle(sketch, "E133", {"center": v(8.91, 3.9) * mm, "radius": 1.04 * mm});
            skPoint(sketch, "E133.first.point", {"position": v(8.9, 2.86) * mm});
            skPoint(sketch, "E133.second.point", {"position": v(8.95, 4.94) * mm});
            skPoint(sketch, "E133.third.point", {"position": v(9.95, 3.84) * mm});
            skSolve(sketch);
        }
        {
            var Q0;
            Q0=qSketchRegion(id+"F25",true);
            var Q1;
            Q1=makeQuery(id+"F6.opShell","OFFSET_FACE",FACE,{"disambiguationData":[OSD([sQuery(id+"F2.wireOp",EDGE,"E20"),sQuery(id+"F2.wireOp",EDGE,"E22")])]});
            extrude(context, id + "F26", {"entities" : qUnion([Q0]), "operationType" : NewBodyOperationType.ADD, "endBoundEntityFace" : qUnion([Q1]), "depth" : 7.5 * mm});
        }
        {
            var Q0;
            Q0=qCreatedBy(makeId("Top.planeOp"),FACE);
            var sketch = newSketch(context, id + "F27", { "sketchPlane" : qUnion([Q0])});
            skLineSegment(sketch, "E134", {"start": v(-14.06, 0.58) * mm, "end": v(-9.7, 0.57) * mm});
            skLineSegment(sketch, "E135", {"start": v(-8.04, -3.57) * mm, "end": v(-8.03, -3.84) * mm});
            skLineSegment(sketch, "E136", {"start": v(-8.03, -3.84) * mm, "end": v(-8.04, -13.15) * mm});
            skLineSegment(sketch, "E137", {"start": v(-8.04, -13.15) * mm, "end": v(-8.03, -13.22) * mm});
            skLineSegment(sketch, "E138", {"start": v(-8.03, -13.22) * mm, "end": v(-8.03, -13.28) * mm});
            skLineSegment(sketch, "E139", {"start": v(-8.03, -13.28) * mm, "end": v(-8.04, -13.35) * mm});
            skLineSegment(sketch, "E140", {"start": v(-8.04, -13.35) * mm, "end": v(-8.04, -13.42) * mm});
            skLineSegment(sketch, "E141", {"start": v(-8.04, -13.42) * mm, "end": v(-8.05, -13.48) * mm});
            skLineSegment(sketch, "E142", {"start": v(-8.05, -13.48) * mm, "end": v(-8.06, -13.55) * mm});
            skLineSegment(sketch, "E143", {"start": v(-8.06, -13.55) * mm, "end": v(-8.07, -13.61) * mm});
            skLineSegment(sketch, "E144", {"start": v(-8.07, -13.61) * mm, "end": v(-8.1, -13.68) * mm});
            skLineSegment(sketch, "E145", {"start": v(-8.1, -13.68) * mm, "end": v(-8.1, -13.74) * mm});
            skLineSegment(sketch, "E146", {"start": v(-8.1, -13.74) * mm, "end": v(-8.13, -13.8) * mm});
            skLineSegment(sketch, "E147", {"start": v(-8.13, -13.8) * mm, "end": v(-8.15, -13.86) * mm});
            skLineSegment(sketch, "E148", {"start": v(-8.15, -13.86) * mm, "end": v(-8.18, -13.93) * mm});
            skLineSegment(sketch, "E149", {"start": v(-8.18, -13.93) * mm, "end": v(-8.2, -13.99) * mm});
            skLineSegment(sketch, "E150", {"start": v(-8.2, -13.99) * mm, "end": v(-8.23, -14.05) * mm});
            skLineSegment(sketch, "E151", {"start": v(-8.23, -14.05) * mm, "end": v(-8.26, -14.1) * mm});
            skLineSegment(sketch, "E152", {"start": v(-8.26, -14.1) * mm, "end": v(-8.3, -14.16) * mm});
            skLineSegment(sketch, "E153", {"start": v(-8.3, -14.16) * mm, "end": v(-8.33, -14.22) * mm});
            skLineSegment(sketch, "E154", {"start": v(-8.33, -14.22) * mm, "end": v(-8.37, -14.27) * mm});
            skLineSegment(sketch, "E155", {"start": v(-8.37, -14.27) * mm, "end": v(-8.4, -14.32) * mm});
            skLineSegment(sketch, "E156", {"start": v(-8.4, -14.32) * mm, "end": v(-8.45, -14.37) * mm});
            skLineSegment(sketch, "E157", {"start": v(-8.45, -14.37) * mm, "end": v(-8.5, -14.42) * mm});
            skLineSegment(sketch, "E158", {"start": v(-8.5, -14.42) * mm, "end": v(-8.54, -14.47) * mm});
            skLineSegment(sketch, "E159", {"start": v(-8.54, -14.47) * mm, "end": v(-8.59, -14.52) * mm});
            skLineSegment(sketch, "E160", {"start": v(-8.59, -14.52) * mm, "end": v(-8.63, -14.56) * mm});
            skLineSegment(sketch, "E161", {"start": v(-8.63, -14.56) * mm, "end": v(-8.69, -14.6) * mm});
            skLineSegment(sketch, "E162", {"start": v(-8.69, -14.6) * mm, "end": v(-8.74, -14.64) * mm});
            skLineSegment(sketch, "E163", {"start": v(-8.74, -14.64) * mm, "end": v(-8.8, -14.68) * mm});
            skLineSegment(sketch, "E164", {"start": v(-8.8, -14.68) * mm, "end": v(-8.85, -14.72) * mm});
            skLineSegment(sketch, "E165", {"start": v(-8.85, -14.72) * mm, "end": v(-8.9, -14.75) * mm});
            skLineSegment(sketch, "E166", {"start": v(-8.9, -14.75) * mm, "end": v(-8.95, -14.77) * mm});
            skLineSegment(sketch, "E167", {"start": v(-8.95, -14.77) * mm, "end": v(-8.99, -14.8) * mm});
            skLineSegment(sketch, "E168", {"start": v(-8.99, -14.8) * mm, "end": v(-9.03, -14.81) * mm});
            skLineSegment(sketch, "E169", {"start": v(-9.03, -14.81) * mm, "end": v(-9.07, -14.83) * mm});
            skLineSegment(sketch, "E170", {"start": v(-9.07, -14.83) * mm, "end": v(-9.11, -14.85) * mm});
            skLineSegment(sketch, "E171", {"start": v(-9.11, -14.85) * mm, "end": v(-9.16, -14.86) * mm});
            skLineSegment(sketch, "E172", {"start": v(-9.16, -14.86) * mm, "end": v(-9.2, -14.88) * mm});
            skLineSegment(sketch, "E173", {"start": v(-9.2, -14.88) * mm, "end": v(-9.24, -14.9) * mm});
            skLineSegment(sketch, "E174", {"start": v(-9.24, -14.9) * mm, "end": v(-9.29, -14.9) * mm});
            skLineSegment(sketch, "E175", {"start": v(-9.29, -14.9) * mm, "end": v(-9.33, -14.91) * mm});
            skLineSegment(sketch, "E176", {"start": v(-9.33, -14.91) * mm, "end": v(-9.38, -14.92) * mm});
            skLineSegment(sketch, "E177", {"start": v(-9.38, -14.92) * mm, "end": v(-9.42, -14.93) * mm});
            skLineSegment(sketch, "E178", {"start": v(-9.42, -14.93) * mm, "end": v(-9.51, -14.94) * mm});
            skLineSegment(sketch, "E179", {"start": v(-9.51, -14.94) * mm, "end": v(-9.6, -14.96) * mm});
            skLineSegment(sketch, "E180", {"start": v(-9.6, -14.96) * mm, "end": v(-9.74, -14.97) * mm});
            skLineSegment(sketch, "E181", {"start": v(-9.74, -14.97) * mm, "end": v(-10.2, -14.98) * mm});
            skLineSegment(sketch, "E182", {"start": v(-10.2, -14.98) * mm, "end": v(-23.2, -14.97) * mm});
            skLineSegment(sketch, "E183", {"start": v(-23.2, -14.97) * mm, "end": v(-23.28, -14.97) * mm});
            skLineSegment(sketch, "E184", {"start": v(-23.28, -14.97) * mm, "end": v(-23.35, -14.97) * mm});
            skLineSegment(sketch, "E185", {"start": v(-23.35, -14.97) * mm, "end": v(-23.43, -14.97) * mm});
            skLineSegment(sketch, "E186", {"start": v(-23.43, -14.97) * mm, "end": v(-23.5, -14.96) * mm});
            skLineSegment(sketch, "E187", {"start": v(-23.5, -14.96) * mm, "end": v(-23.58, -14.94) * mm});
            skLineSegment(sketch, "E188", {"start": v(-23.58, -14.94) * mm, "end": v(-23.65, -14.93) * mm});
            skLineSegment(sketch, "E189", {"start": v(-23.65, -14.93) * mm, "end": v(-23.72, -14.9) * mm});
            skLineSegment(sketch, "E190", {"start": v(-23.72, -14.9) * mm, "end": v(-23.8, -14.89) * mm});
            skLineSegment(sketch, "E191", {"start": v(-23.8, -14.89) * mm, "end": v(-23.86, -14.86) * mm});
            skLineSegment(sketch, "E192", {"start": v(-23.86, -14.86) * mm, "end": v(-23.93, -14.83) * mm});
            skLineSegment(sketch, "E193", {"start": v(-23.93, -14.83) * mm, "end": v(-24, -14.8) * mm});
            skLineSegment(sketch, "E194", {"start": v(-24, -14.8) * mm, "end": v(-24.07, -14.77) * mm});
            skLineSegment(sketch, "E195", {"start": v(-24.07, -14.77) * mm, "end": v(-24.13, -14.73) * mm});
            skLineSegment(sketch, "E196", {"start": v(-24.13, -14.73) * mm, "end": v(-24.2, -14.7) * mm});
            skLineSegment(sketch, "E197", {"start": v(-24.2, -14.7) * mm, "end": v(-24.26, -14.65) * mm});
            skLineSegment(sketch, "E198", {"start": v(-24.26, -14.65) * mm, "end": v(-24.32, -14.6) * mm});
            skLineSegment(sketch, "E199", {"start": v(-24.32, -14.6) * mm, "end": v(-24.38, -14.56) * mm});
            skLineSegment(sketch, "E200", {"start": v(-24.38, -14.56) * mm, "end": v(-24.43, -14.51) * mm});
            skLineSegment(sketch, "E201", {"start": v(-24.43, -14.51) * mm, "end": v(-24.48, -14.46) * mm});
            skLineSegment(sketch, "E202", {"start": v(-24.48, -14.46) * mm, "end": v(-24.54, -14.4) * mm});
            skLineSegment(sketch, "E203", {"start": v(-24.54, -14.4) * mm, "end": v(-24.59, -14.35) * mm});
            skLineSegment(sketch, "E204", {"start": v(-24.59, -14.35) * mm, "end": v(-24.63, -14.3) * mm});
            skLineSegment(sketch, "E205", {"start": v(-24.63, -14.3) * mm, "end": v(-24.68, -14.23) * mm});
            skLineSegment(sketch, "E206", {"start": v(-24.68, -14.23) * mm, "end": v(-24.72, -14.17) * mm});
            skLineSegment(sketch, "E207", {"start": v(-24.72, -14.17) * mm, "end": v(-24.76, -14.1) * mm});
            skLineSegment(sketch, "E208", {"start": v(-24.76, -14.1) * mm, "end": v(-24.8, -14.04) * mm});
            skLineSegment(sketch, "E209", {"start": v(-24.8, -14.04) * mm, "end": v(-24.82, -13.97) * mm});
            skLineSegment(sketch, "E210", {"start": v(-24.82, -13.97) * mm, "end": v(-24.85, -13.9) * mm});
            skLineSegment(sketch, "E211", {"start": v(-24.85, -13.9) * mm, "end": v(-24.88, -13.83) * mm});
            skLineSegment(sketch, "E212", {"start": v(-24.88, -13.83) * mm, "end": v(-24.9, -13.76) * mm});
            skLineSegment(sketch, "E213", {"start": v(-24.9, -13.76) * mm, "end": v(-24.92, -13.66) * mm});
            skLineSegment(sketch, "E214", {"start": v(-24.92, -13.66) * mm, "end": v(-24.94, -13.55) * mm});
            skLineSegment(sketch, "E215", {"start": v(-24.94, -13.55) * mm, "end": v(-24.96, -13.38) * mm});
            skLineSegment(sketch, "E216", {"start": v(-24.96, -13.38) * mm, "end": v(-24.98, -12.8) * mm});
            skLineSegment(sketch, "E217", {"start": v(-24.98, -12.8) * mm, "end": v(-24.98, -3.92) * mm});
            skLineSegment(sketch, "E218", {"start": v(-24.98, -3.92) * mm, "end": v(-24.97, -3.38) * mm});
            skLineSegment(sketch, "E219", {"start": v(-24.97, -3.38) * mm, "end": v(-24.96, -3.24) * mm});
            skLineSegment(sketch, "E220", {"start": v(-24.96, -3.24) * mm, "end": v(-24.95, -3.15) * mm});
            skLineSegment(sketch, "E221", {"start": v(-24.95, -3.15) * mm, "end": v(-24.94, -3.1) * mm});
            skLineSegment(sketch, "E222", {"start": v(-24.94, -3.1) * mm, "end": v(-24.93, -3.06) * mm});
            skLineSegment(sketch, "E223", {"start": v(-24.93, -3.06) * mm, "end": v(-24.93, -3.02) * mm});
            skLineSegment(sketch, "E224", {"start": v(-24.93, -3.02) * mm, "end": v(-24.92, -2.97) * mm});
            skLineSegment(sketch, "E225", {"start": v(-24.92, -2.97) * mm, "end": v(-24.9, -2.93) * mm});
            skLineSegment(sketch, "E226", {"start": v(-24.9, -2.93) * mm, "end": v(-24.9, -2.88) * mm});
            skLineSegment(sketch, "E227", {"start": v(-24.9, -2.88) * mm, "end": v(-24.88, -2.84) * mm});
            skLineSegment(sketch, "E228", {"start": v(-24.88, -2.84) * mm, "end": v(-24.87, -2.8) * mm});
            skLineSegment(sketch, "E229", {"start": v(-24.87, -2.8) * mm, "end": v(-24.85, -2.76) * mm});
            skLineSegment(sketch, "E230", {"start": v(-24.85, -2.76) * mm, "end": v(-24.83, -2.71) * mm});
            skLineSegment(sketch, "E231", {"start": v(-24.83, -2.71) * mm, "end": v(-24.81, -2.67) * mm});
            skLineSegment(sketch, "E232", {"start": v(-24.81, -2.67) * mm, "end": v(-24.8, -2.63) * mm});
            skLineSegment(sketch, "E233", {"start": v(-24.8, -2.63) * mm, "end": v(-24.77, -2.58) * mm});
            skLineSegment(sketch, "E234", {"start": v(-24.77, -2.58) * mm, "end": v(-24.74, -2.53) * mm});
            skLineSegment(sketch, "E235", {"start": v(-24.74, -2.53) * mm, "end": v(-24.7, -2.48) * mm});
            skLineSegment(sketch, "E236", {"start": v(-24.7, -2.48) * mm, "end": v(-24.68, -2.43) * mm});
            skLineSegment(sketch, "E237", {"start": v(-24.68, -2.43) * mm, "end": v(-24.64, -2.38) * mm});
            skLineSegment(sketch, "E238", {"start": v(-24.64, -2.38) * mm, "end": v(-24.6, -2.34) * mm});
            skLineSegment(sketch, "E239", {"start": v(-24.6, -2.34) * mm, "end": v(-24.57, -2.3) * mm});
            skLineSegment(sketch, "E240", {"start": v(-24.57, -2.3) * mm, "end": v(-24.53, -2.25) * mm});
            skLineSegment(sketch, "E241", {"start": v(-24.53, -2.25) * mm, "end": v(-24.5, -2.2) * mm});
            skLineSegment(sketch, "E242", {"start": v(-24.5, -2.2) * mm, "end": v(-24.45, -2.16) * mm});
            skLineSegment(sketch, "E243", {"start": v(-24.45, -2.16) * mm, "end": v(-24.41, -2.12) * mm});
            skLineSegment(sketch, "E244", {"start": v(-24.41, -2.12) * mm, "end": v(-24.37, -2.08) * mm});
            skLineSegment(sketch, "E245", {"start": v(-24.37, -2.08) * mm, "end": v(-24.32, -2.05) * mm});
            skLineSegment(sketch, "E246", {"start": v(-24.32, -2.05) * mm, "end": v(-24.28, -2.01) * mm});
            skLineSegment(sketch, "E247", {"start": v(-24.28, -2.01) * mm, "end": v(-24.23, -1.98) * mm});
            skLineSegment(sketch, "E248", {"start": v(-24.23, -1.98) * mm, "end": v(-24.18, -1.94) * mm});
            skLineSegment(sketch, "E249", {"start": v(-24.18, -1.94) * mm, "end": v(-24.13, -1.91) * mm});
            skLineSegment(sketch, "E250", {"start": v(-24.13, -1.91) * mm, "end": v(-24.08, -1.88) * mm});
            skLineSegment(sketch, "E251", {"start": v(-24.08, -1.88) * mm, "end": v(-24.03, -1.86) * mm});
            skLineSegment(sketch, "E252", {"start": v(-24.03, -1.86) * mm, "end": v(-23.98, -1.83) * mm});
            skLineSegment(sketch, "E253", {"start": v(-23.98, -1.83) * mm, "end": v(-23.93, -1.8) * mm});
            skLineSegment(sketch, "E254", {"start": v(-23.93, -1.8) * mm, "end": v(-23.87, -1.79) * mm});
            skLineSegment(sketch, "E255", {"start": v(-23.87, -1.79) * mm, "end": v(-23.82, -1.77) * mm});
            skLineSegment(sketch, "E256", {"start": v(-23.82, -1.77) * mm, "end": v(-23.76, -1.75) * mm});
            skLineSegment(sketch, "E257", {"start": v(-23.76, -1.75) * mm, "end": v(-23.7, -1.73) * mm});
            skLineSegment(sketch, "E258", {"start": v(-23.7, -1.73) * mm, "end": v(-23.65, -1.72) * mm});
            skLineSegment(sketch, "E259", {"start": v(-23.65, -1.72) * mm, "end": v(-23.6, -1.71) * mm});
            skLineSegment(sketch, "E260", {"start": v(-23.6, -1.71) * mm, "end": v(-23.53, -1.7) * mm});
            skLineSegment(sketch, "E261", {"start": v(-23.53, -1.7) * mm, "end": v(-23.48, -1.7) * mm});
            skLineSegment(sketch, "E262", {"start": v(-23.48, -1.7) * mm, "end": v(-23.32, -1.69) * mm});
            skLineSegment(sketch, "E263", {"start": v(-23.32, -1.69) * mm, "end": v(-23.17, -1.68) * mm});
            skLineSegment(sketch, "E264", {"start": v(-23.17, -1.68) * mm, "end": v(-22.95, -1.67) * mm});
            skLineSegment(sketch, "E265", {"start": v(-22.95, -1.67) * mm, "end": v(-21.9, -1.67) * mm});
            skLineSegment(sketch, "E266", {"start": v(-21.9, -1.67) * mm, "end": v(-21.52, -1.67) * mm});
            skLineSegment(sketch, "E267", {"start": v(-21.52, -1.67) * mm, "end": v(-21.3, -1.66) * mm});
            skLineSegment(sketch, "E268", {"start": v(-21.3, -1.66) * mm, "end": v(-21.2, -1.64) * mm});
            skLineSegment(sketch, "E269", {"start": v(-21.2, -1.64) * mm, "end": v(-20.86, -1.5) * mm});
            skLineSegment(sketch, "E270", {"start": v(-20.86, -1.5) * mm, "end": v(-17.7, 0.02) * mm});
            skLineSegment(sketch, "E271", {"start": v(-17.7, 0.02) * mm, "end": v(-17.01, 0.36) * mm});
            skLineSegment(sketch, "E272", {"start": v(-15.75, 0.24) * mm, "end": v(-14.06, -0.59) * mm});
            skLineSegment(sketch, "E273", {"start": v(-14.06, -0.59) * mm, "end": v(-14.06, 0.58) * mm});
            skLineSegment(sketch, "E274", {"start": v(-13.15, -0.33) * mm, "end": v(-13.15, -2.1) * mm});
            skLineSegment(sketch, "E275", {"start": v(-13.15, -2.1) * mm, "end": v(-13.26, -2.06) * mm});
            skLineSegment(sketch, "E276", {"start": v(-13.26, -2.06) * mm, "end": v(-13.9, -1.75) * mm});
            skLineSegment(sketch, "E277", {"start": v(-16.83, -0.6) * mm, "end": v(-17.05, -0.71) * mm});
            skLineSegment(sketch, "E278", {"start": v(-17.05, -0.71) * mm, "end": v(-17.27, -0.83) * mm});
            skLineSegment(sketch, "E279", {"start": v(-17.27, -0.83) * mm, "end": v(-18.4, -1.4) * mm});
            skLineSegment(sketch, "E280", {"start": v(-18.4, -1.4) * mm, "end": v(-22.7, -3.51) * mm});
            skLineSegment(sketch, "E281", {"start": v(-22.7, -3.51) * mm, "end": v(-23.6, -3.97) * mm});
            skLineSegment(sketch, "E282", {"start": v(-23.6, -3.97) * mm, "end": v(-23.64, -4) * mm});
            skLineSegment(sketch, "E283", {"start": v(-23.64, -4) * mm, "end": v(-23.69, -4.02) * mm});
            skLineSegment(sketch, "E284", {"start": v(-23.69, -4.02) * mm, "end": v(-23.73, -4.05) * mm});
            skLineSegment(sketch, "E285", {"start": v(-23.73, -4.05) * mm, "end": v(-23.76, -4.08) * mm});
            skLineSegment(sketch, "E286", {"start": v(-23.76, -4.08) * mm, "end": v(-23.79, -4.1) * mm});
            skLineSegment(sketch, "E287", {"start": v(-23.79, -4.1) * mm, "end": v(-23.8, -4.13) * mm});
            skLineSegment(sketch, "E288", {"start": v(-23.8, -4.13) * mm, "end": v(-23.82, -4.15) * mm});
            skLineSegment(sketch, "E289", {"start": v(-23.82, -4.15) * mm, "end": v(-23.83, -4.16) * mm});
            skLineSegment(sketch, "E290", {"start": v(-23.83, -4.16) * mm, "end": v(-23.83, -4.18) * mm});
            skLineSegment(sketch, "E291", {"start": v(-23.83, -4.18) * mm, "end": v(-23.84, -4.2) * mm});
            skLineSegment(sketch, "E292", {"start": v(-23.84, -4.2) * mm, "end": v(-23.85, -4.21) * mm});
            skLineSegment(sketch, "E293", {"start": v(-23.85, -4.21) * mm, "end": v(-23.85, -4.23) * mm});
            skLineSegment(sketch, "E294", {"start": v(-23.85, -4.23) * mm, "end": v(-23.85, -4.25) * mm});
            skLineSegment(sketch, "E295", {"start": v(-23.85, -4.25) * mm, "end": v(-23.86, -4.27) * mm});
            skLineSegment(sketch, "E296", {"start": v(-23.86, -4.27) * mm, "end": v(-23.86, -4.29) * mm});
            skLineSegment(sketch, "E297", {"start": v(-23.86, -4.29) * mm, "end": v(-23.86, -4.3) * mm});
            skLineSegment(sketch, "E298", {"start": v(-23.86, -4.3) * mm, "end": v(-23.85, -4.32) * mm});
            skLineSegment(sketch, "E299", {"start": v(-23.85, -4.32) * mm, "end": v(-23.85, -4.34) * mm});
            skLineSegment(sketch, "E300", {"start": v(-23.85, -4.34) * mm, "end": v(-23.84, -4.36) * mm});
            skLineSegment(sketch, "E301", {"start": v(-23.84, -4.36) * mm, "end": v(-23.84, -4.38) * mm});
            skLineSegment(sketch, "E302", {"start": v(-23.84, -4.38) * mm, "end": v(-23.83, -4.4) * mm});
            skLineSegment(sketch, "E303", {"start": v(-23.83, -4.4) * mm, "end": v(-23.82, -4.42) * mm});
            skLineSegment(sketch, "E304", {"start": v(-23.82, -4.42) * mm, "end": v(-23.81, -4.44) * mm});
            skLineSegment(sketch, "E305", {"start": v(-23.81, -4.44) * mm, "end": v(-23.8, -4.45) * mm});
            skLineSegment(sketch, "E306", {"start": v(-23.8, -4.45) * mm, "end": v(-23.8, -4.47) * mm});
            skLineSegment(sketch, "E307", {"start": v(-23.8, -4.47) * mm, "end": v(-23.78, -4.48) * mm});
            skLineSegment(sketch, "E308", {"start": v(-23.78, -4.48) * mm, "end": v(-23.76, -4.5) * mm});
            skLineSegment(sketch, "E309", {"start": v(-23.76, -4.5) * mm, "end": v(-23.73, -4.53) * mm});
            skLineSegment(sketch, "E310", {"start": v(-23.73, -4.53) * mm, "end": v(-23.7, -4.55) * mm});
            skLineSegment(sketch, "E311", {"start": v(-23.7, -4.55) * mm, "end": v(-23.58, -4.62) * mm});
            skLineSegment(sketch, "E312", {"start": v(-23.58, -4.62) * mm, "end": v(-23.42, -4.7) * mm});
            skLineSegment(sketch, "E313", {"start": v(-23.42, -4.7) * mm, "end": v(-19.6, -6.6) * mm});
            skLineSegment(sketch, "E314", {"start": v(-19.6, -6.6) * mm, "end": v(-18.6, -7.09) * mm});
            skLineSegment(sketch, "E315", {"start": v(-18.6, -7.09) * mm, "end": v(-17.5, -7.65) * mm});
            skLineSegment(sketch, "E316", {"start": v(-17.5, -7.65) * mm, "end": v(-16.7, -8.03) * mm});
            skLineSegment(sketch, "E317", {"start": v(-16.7, -8.03) * mm, "end": v(-16.68, -8.04) * mm});
            skLineSegment(sketch, "E318", {"start": v(-16.68, -8.04) * mm, "end": v(-16.66, -8.05) * mm});
            skLineSegment(sketch, "E319", {"start": v(-16.66, -8.05) * mm, "end": v(-16.64, -8.06) * mm});
            skLineSegment(sketch, "E320", {"start": v(-16.64, -8.06) * mm, "end": v(-16.62, -8.06) * mm});
            skLineSegment(sketch, "E321", {"start": v(-16.62, -8.06) * mm, "end": v(-16.6, -8.07) * mm});
            skLineSegment(sketch, "E322", {"start": v(-16.6, -8.07) * mm, "end": v(-16.58, -8.07) * mm});
            skLineSegment(sketch, "E323", {"start": v(-16.58, -8.07) * mm, "end": v(-16.56, -8.07) * mm});
            skLineSegment(sketch, "E324", {"start": v(-16.56, -8.07) * mm, "end": v(-16.54, -8.07) * mm});
            skLineSegment(sketch, "E325", {"start": v(-16.54, -8.07) * mm, "end": v(-16.52, -8.08) * mm});
            skLineSegment(sketch, "E326", {"start": v(-16.52, -8.08) * mm, "end": v(-16.48, -8.07) * mm});
            skLineSegment(sketch, "E327", {"start": v(-16.48, -8.07) * mm, "end": v(-16.44, -8.07) * mm});
            skLineSegment(sketch, "E328", {"start": v(-16.44, -8.07) * mm, "end": v(-16.4, -8.06) * mm});
            skLineSegment(sketch, "E329", {"start": v(-16.4, -8.06) * mm, "end": v(-16.32, -8.04) * mm});
            skLineSegment(sketch, "E330", {"start": v(-16.32, -8.04) * mm, "end": v(-16.14, -7.96) * mm});
            skLineSegment(sketch, "E331", {"start": v(-16.14, -7.96) * mm, "end": v(-13.76, -6.78) * mm});
            skLineSegment(sketch, "E332", {"start": v(-13.76, -6.78) * mm, "end": v(-9.85, -4.84) * mm});
            skLineSegment(sketch, "E333", {"start": v(-9.4, -3.99) * mm, "end": v(-9.57, -3.89) * mm});
            skLineSegment(sketch, "E334", {"start": v(-9.57, -3.89) * mm, "end": v(-10.59, -3.4) * mm});
            skLineSegment(sketch, "E335", {"start": v(-10.59, -3.4) * mm, "end": v(-10.6, -0.33) * mm});
            skLineSegment(sketch, "E336", {"start": v(-10.6, -0.33) * mm, "end": v(-13.15, -0.33) * mm});
            skLineSegment(sketch, "E337", {"start": v(-26.34, -4.98) * mm, "end": v(-25.3, -4.97) * mm});
            skLineSegment(sketch, "E338", {"start": v(-25.3, -4.97) * mm, "end": v(-25.28, -6.53) * mm});
            skLineSegment(sketch, "E339", {"start": v(-25.28, -6.53) * mm, "end": v(-26.11, -6.52) * mm});
            skLineSegment(sketch, "E340", {"start": v(-26.11, -6.52) * mm, "end": v(-26.27, -6.5) * mm});
            skLineSegment(sketch, "E341", {"start": v(-26.27, -6.5) * mm, "end": v(-26.38, -6.49) * mm});
            skLineSegment(sketch, "E342", {"start": v(-26.38, -6.49) * mm, "end": v(-26.4, -6.47) * mm});
            skLineSegment(sketch, "E343", {"start": v(-26.4, -6.47) * mm, "end": v(-26.43, -6.45) * mm});
            skLineSegment(sketch, "E344", {"start": v(-26.43, -6.45) * mm, "end": v(-26.45, -6.43) * mm});
            skLineSegment(sketch, "E345", {"start": v(-26.45, -6.43) * mm, "end": v(-26.47, -6.41) * mm});
            skLineSegment(sketch, "E346", {"start": v(-26.47, -6.41) * mm, "end": v(-26.49, -6.39) * mm});
            skLineSegment(sketch, "E347", {"start": v(-26.49, -6.39) * mm, "end": v(-26.5, -6.37) * mm});
            skLineSegment(sketch, "E348", {"start": v(-26.5, -6.37) * mm, "end": v(-26.52, -6.34) * mm});
            skLineSegment(sketch, "E349", {"start": v(-26.52, -6.34) * mm, "end": v(-26.54, -6.32) * mm});
            skLineSegment(sketch, "E350", {"start": v(-26.54, -6.32) * mm, "end": v(-26.55, -6.29) * mm});
            skLineSegment(sketch, "E351", {"start": v(-26.55, -6.29) * mm, "end": v(-26.56, -6.26) * mm});
            skLineSegment(sketch, "E352", {"start": v(-26.56, -6.26) * mm, "end": v(-26.57, -6.23) * mm});
            skLineSegment(sketch, "E353", {"start": v(-26.57, -6.23) * mm, "end": v(-26.58, -6.2) * mm});
            skLineSegment(sketch, "E354", {"start": v(-26.58, -6.2) * mm, "end": v(-26.59, -6.18) * mm});
            skLineSegment(sketch, "E355", {"start": v(-26.59, -6.18) * mm, "end": v(-26.6, -6.15) * mm});
            skLineSegment(sketch, "E356", {"start": v(-26.6, -6.15) * mm, "end": v(-26.6, -6.09) * mm});
            skLineSegment(sketch, "E357", {"start": v(-26.6, -6.09) * mm, "end": v(-26.62, -6.03) * mm});
            skLineSegment(sketch, "E358", {"start": v(-26.62, -6.03) * mm, "end": v(-26.62, -5.9) * mm});
            skLineSegment(sketch, "E359", {"start": v(-26.62, -5.9) * mm, "end": v(-26.63, -5.75) * mm});
            skLineSegment(sketch, "E360", {"start": v(-26.63, -5.75) * mm, "end": v(-26.63, -5.7) * mm});
            skLineSegment(sketch, "E361", {"start": v(-26.63, -5.7) * mm, "end": v(-26.63, -5.62) * mm});
            skLineSegment(sketch, "E362", {"start": v(-26.63, -5.62) * mm, "end": v(-26.62, -5.5) * mm});
            skLineSegment(sketch, "E363", {"start": v(-26.62, -5.5) * mm, "end": v(-26.6, -5.42) * mm});
            skLineSegment(sketch, "E364", {"start": v(-26.6, -5.42) * mm, "end": v(-26.6, -5.36) * mm});
            skLineSegment(sketch, "E365", {"start": v(-26.6, -5.36) * mm, "end": v(-26.58, -5.3) * mm});
            skLineSegment(sketch, "E366", {"start": v(-26.58, -5.3) * mm, "end": v(-26.58, -5.28) * mm});
            skLineSegment(sketch, "E367", {"start": v(-26.58, -5.28) * mm, "end": v(-26.57, -5.25) * mm});
            skLineSegment(sketch, "E368", {"start": v(-26.57, -5.25) * mm, "end": v(-26.56, -5.23) * mm});
            skLineSegment(sketch, "E369", {"start": v(-26.56, -5.23) * mm, "end": v(-26.55, -5.2) * mm});
            skLineSegment(sketch, "E370", {"start": v(-26.55, -5.2) * mm, "end": v(-26.53, -5.18) * mm});
            skLineSegment(sketch, "E371", {"start": v(-26.53, -5.18) * mm, "end": v(-26.52, -5.15) * mm});
            skLineSegment(sketch, "E372", {"start": v(-26.52, -5.15) * mm, "end": v(-26.5, -5.13) * mm});
            skLineSegment(sketch, "E373", {"start": v(-26.5, -5.13) * mm, "end": v(-26.5, -5.1) * mm});
            skLineSegment(sketch, "E374", {"start": v(-26.5, -5.1) * mm, "end": v(-26.47, -5.09) * mm});
            skLineSegment(sketch, "E375", {"start": v(-26.47, -5.09) * mm, "end": v(-26.46, -5.07) * mm});
            skLineSegment(sketch, "E376", {"start": v(-26.46, -5.07) * mm, "end": v(-26.44, -5.05) * mm});
            skLineSegment(sketch, "E377", {"start": v(-26.44, -5.05) * mm, "end": v(-26.42, -5.03) * mm});
            skLineSegment(sketch, "E378", {"start": v(-26.42, -5.03) * mm, "end": v(-26.4, -5.01) * mm});
            skLineSegment(sketch, "E379", {"start": v(-26.4, -5.01) * mm, "end": v(-26.37, -5) * mm});
            skLineSegment(sketch, "E380", {"start": v(-26.37, -5) * mm, "end": v(-26.34, -4.98) * mm});
            skLineSegment(sketch, "E381", {"start": v(-7.72, -4.97) * mm, "end": v(-7.68, -4.98) * mm});
            skLineSegment(sketch, "E382", {"start": v(-7.68, -4.98) * mm, "end": v(-7.64, -4.98) * mm});
            skLineSegment(sketch, "E383", {"start": v(-7.64, -4.98) * mm, "end": v(-7.6, -4.98) * mm});
            skLineSegment(sketch, "E384", {"start": v(-7.6, -4.98) * mm, "end": v(-7.55, -4.98) * mm});
            skLineSegment(sketch, "E385", {"start": v(-7.55, -4.98) * mm, "end": v(-7.5, -4.98) * mm});
            skLineSegment(sketch, "E386", {"start": v(-7.5, -4.98) * mm, "end": v(-7.41, -4.97) * mm});
            skLineSegment(sketch, "E387", {"start": v(-7.41, -4.97) * mm, "end": v(-7.13, -4.95) * mm});
            skLineSegment(sketch, "E388", {"start": v(-7.13, -4.95) * mm, "end": v(-7.09, -4.94) * mm});
            skLineSegment(sketch, "E389", {"start": v(-7.09, -4.94) * mm, "end": v(-7.04, -4.94) * mm});
            skLineSegment(sketch, "E390", {"start": v(-7.04, -4.94) * mm, "end": v(-7, -4.94) * mm});
            skLineSegment(sketch, "E391", {"start": v(-7, -4.94) * mm, "end": v(-6.95, -4.94) * mm});
            skLineSegment(sketch, "E392", {"start": v(-6.95, -4.94) * mm, "end": v(-6.9, -4.94) * mm});
            skLineSegment(sketch, "E393", {"start": v(-6.9, -4.94) * mm, "end": v(-6.86, -4.95) * mm});
            skLineSegment(sketch, "E394", {"start": v(-6.86, -4.95) * mm, "end": v(-6.82, -4.95) * mm});
            skLineSegment(sketch, "E395", {"start": v(-6.82, -4.95) * mm, "end": v(-6.78, -4.96) * mm});
            skLineSegment(sketch, "E396", {"start": v(-6.78, -4.96) * mm, "end": v(-6.74, -4.97) * mm});
            skLineSegment(sketch, "E397", {"start": v(-6.74, -4.97) * mm, "end": v(-6.7, -4.99) * mm});
            skLineSegment(sketch, "E398", {"start": v(-6.7, -4.99) * mm, "end": v(-6.66, -5) * mm});
            skLineSegment(sketch, "E399", {"start": v(-6.66, -5) * mm, "end": v(-6.62, -5.03) * mm});
            skLineSegment(sketch, "E400", {"start": v(-6.62, -5.03) * mm, "end": v(-6.58, -5.05) * mm});
            skLineSegment(sketch, "E401", {"start": v(-6.58, -5.05) * mm, "end": v(-6.55, -5.08) * mm});
            skLineSegment(sketch, "E402", {"start": v(-6.55, -5.08) * mm, "end": v(-6.52, -5.1) * mm});
            skLineSegment(sketch, "E403", {"start": v(-6.52, -5.1) * mm, "end": v(-6.48, -5.14) * mm});
            skLineSegment(sketch, "E404", {"start": v(-6.48, -5.14) * mm, "end": v(-6.47, -5.18) * mm});
            skLineSegment(sketch, "E405", {"start": v(-6.47, -5.18) * mm, "end": v(-6.46, -5.21) * mm});
            skLineSegment(sketch, "E406", {"start": v(-6.46, -5.21) * mm, "end": v(-6.45, -5.24) * mm});
            skLineSegment(sketch, "E407", {"start": v(-6.45, -5.24) * mm, "end": v(-6.43, -5.31) * mm});
            skLineSegment(sketch, "E408", {"start": v(-6.43, -5.31) * mm, "end": v(-6.41, -5.38) * mm});
            skLineSegment(sketch, "E409", {"start": v(-6.41, -5.38) * mm, "end": v(-6.4, -5.45) * mm});
            skLineSegment(sketch, "E410", {"start": v(-6.4, -5.45) * mm, "end": v(-6.4, -5.52) * mm});
            skLineSegment(sketch, "E411", {"start": v(-6.4, -5.52) * mm, "end": v(-6.39, -5.59) * mm});
            skLineSegment(sketch, "E412", {"start": v(-6.39, -5.59) * mm, "end": v(-6.38, -5.7) * mm});
            skLineSegment(sketch, "E413", {"start": v(-6.38, -5.7) * mm, "end": v(-6.39, -5.83) * mm});
            skLineSegment(sketch, "E414", {"start": v(-6.39, -5.83) * mm, "end": v(-6.4, -6.08) * mm});
            skLineSegment(sketch, "E415", {"start": v(-6.4, -6.08) * mm, "end": v(-6.42, -6.15) * mm});
            skLineSegment(sketch, "E416", {"start": v(-6.42, -6.15) * mm, "end": v(-6.47, -6.3) * mm});
            skLineSegment(sketch, "E417", {"start": v(-6.47, -6.3) * mm, "end": v(-6.5, -6.36) * mm});
            skLineSegment(sketch, "E418", {"start": v(-6.5, -6.36) * mm, "end": v(-6.53, -6.4) * mm});
            skLineSegment(sketch, "E419", {"start": v(-6.53, -6.4) * mm, "end": v(-6.56, -6.43) * mm});
            skLineSegment(sketch, "E420", {"start": v(-6.56, -6.43) * mm, "end": v(-6.59, -6.46) * mm});
            skLineSegment(sketch, "E421", {"start": v(-6.59, -6.46) * mm, "end": v(-6.61, -6.47) * mm});
            skLineSegment(sketch, "E422", {"start": v(-6.61, -6.47) * mm, "end": v(-6.64, -6.49) * mm});
            skLineSegment(sketch, "E423", {"start": v(-6.64, -6.49) * mm, "end": v(-6.67, -6.5) * mm});
            skLineSegment(sketch, "E424", {"start": v(-6.67, -6.5) * mm, "end": v(-7.74, -6.53) * mm});
            skLineSegment(sketch, "E425", {"start": v(-7.74, -6.53) * mm, "end": v(-7.72, -4.97) * mm});
            skLineSegment(sketch, "E426", {"start": v(-26.35, -7.32) * mm, "end": v(-25.28, -7.3) * mm});
            skLineSegment(sketch, "E427", {"start": v(-25.28, -7.3) * mm, "end": v(-25.28, -8.87) * mm});
            skLineSegment(sketch, "E428", {"start": v(-25.28, -8.87) * mm, "end": v(-26.35, -8.85) * mm});
            skLineSegment(sketch, "E429", {"start": v(-26.35, -8.85) * mm, "end": v(-26.5, -8.7) * mm});
            skLineSegment(sketch, "E430", {"start": v(-26.5, -8.7) * mm, "end": v(-26.55, -8.62) * mm});
            skLineSegment(sketch, "E431", {"start": v(-26.55, -8.62) * mm, "end": v(-26.57, -8.57) * mm});
            skLineSegment(sketch, "E432", {"start": v(-26.57, -8.57) * mm, "end": v(-26.6, -8.52) * mm});
            skLineSegment(sketch, "E433", {"start": v(-26.6, -8.52) * mm, "end": v(-26.6, -8.47) * mm});
            skLineSegment(sketch, "E434", {"start": v(-26.6, -8.47) * mm, "end": v(-26.6, -8.45) * mm});
            skLineSegment(sketch, "E435", {"start": v(-26.6, -8.45) * mm, "end": v(-26.61, -8.37) * mm});
            skLineSegment(sketch, "E436", {"start": v(-26.61, -8.37) * mm, "end": v(-26.63, -8.2) * mm});
            skLineSegment(sketch, "E437", {"start": v(-26.63, -8.2) * mm, "end": v(-26.63, -8.08) * mm});
            skLineSegment(sketch, "E438", {"start": v(-26.63, -8.08) * mm, "end": v(-26.64, -8) * mm});
            skLineSegment(sketch, "E439", {"start": v(-26.64, -8) * mm, "end": v(-26.64, -7.95) * mm});
            skLineSegment(sketch, "E440", {"start": v(-26.64, -7.95) * mm, "end": v(-26.63, -7.9) * mm});
            skLineSegment(sketch, "E441", {"start": v(-26.63, -7.9) * mm, "end": v(-26.63, -7.86) * mm});
            skLineSegment(sketch, "E442", {"start": v(-26.63, -7.86) * mm, "end": v(-26.63, -7.82) * mm});
            skLineSegment(sketch, "E443", {"start": v(-26.63, -7.82) * mm, "end": v(-26.62, -7.78) * mm});
            skLineSegment(sketch, "E444", {"start": v(-26.62, -7.78) * mm, "end": v(-26.61, -7.74) * mm});
            skLineSegment(sketch, "E445", {"start": v(-26.61, -7.74) * mm, "end": v(-26.6, -7.7) * mm});
            skLineSegment(sketch, "E446", {"start": v(-26.6, -7.7) * mm, "end": v(-26.6, -7.66) * mm});
            skLineSegment(sketch, "E447", {"start": v(-26.6, -7.66) * mm, "end": v(-26.58, -7.62) * mm});
            skLineSegment(sketch, "E448", {"start": v(-26.58, -7.62) * mm, "end": v(-26.56, -7.58) * mm});
            skLineSegment(sketch, "E449", {"start": v(-26.56, -7.58) * mm, "end": v(-26.55, -7.54) * mm});
            skLineSegment(sketch, "E450", {"start": v(-26.55, -7.54) * mm, "end": v(-26.53, -7.5) * mm});
            skLineSegment(sketch, "E451", {"start": v(-26.53, -7.5) * mm, "end": v(-26.5, -7.47) * mm});
            skLineSegment(sketch, "E452", {"start": v(-26.5, -7.47) * mm, "end": v(-26.48, -7.44) * mm});
            skLineSegment(sketch, "E453", {"start": v(-26.48, -7.44) * mm, "end": v(-26.45, -7.4) * mm});
            skLineSegment(sketch, "E454", {"start": v(-26.45, -7.4) * mm, "end": v(-26.42, -7.38) * mm});
            skLineSegment(sketch, "E455", {"start": v(-26.42, -7.38) * mm, "end": v(-26.39, -7.35) * mm});
            skLineSegment(sketch, "E456", {"start": v(-26.39, -7.35) * mm, "end": v(-26.35, -7.32) * mm});
            skLineSegment(sketch, "E457", {"start": v(-7.73, -7.3) * mm, "end": v(-6.66, -7.32) * mm});
            skLineSegment(sketch, "E458", {"start": v(-6.66, -7.32) * mm, "end": v(-6.53, -7.44) * mm});
            skLineSegment(sketch, "E459", {"start": v(-6.53, -7.44) * mm, "end": v(-6.47, -7.53) * mm});
            skLineSegment(sketch, "E460", {"start": v(-6.47, -7.53) * mm, "end": v(-6.44, -7.58) * mm});
            skLineSegment(sketch, "E461", {"start": v(-6.44, -7.58) * mm, "end": v(-6.43, -7.63) * mm});
            skLineSegment(sketch, "E462", {"start": v(-6.43, -7.63) * mm, "end": v(-6.41, -7.68) * mm});
            skLineSegment(sketch, "E463", {"start": v(-6.41, -7.68) * mm, "end": v(-6.4, -7.7) * mm});
            skLineSegment(sketch, "E464", {"start": v(-6.4, -7.7) * mm, "end": v(-6.4, -7.79) * mm});
            skLineSegment(sketch, "E465", {"start": v(-6.4, -7.79) * mm, "end": v(-6.39, -7.96) * mm});
            skLineSegment(sketch, "E466", {"start": v(-6.39, -7.96) * mm, "end": v(-6.38, -8.09) * mm});
            skLineSegment(sketch, "E467", {"start": v(-6.38, -8.09) * mm, "end": v(-6.38, -8.17) * mm});
            skLineSegment(sketch, "E468", {"start": v(-6.38, -8.17) * mm, "end": v(-6.38, -8.22) * mm});
            skLineSegment(sketch, "E469", {"start": v(-6.38, -8.22) * mm, "end": v(-6.38, -8.26) * mm});
            skLineSegment(sketch, "E470", {"start": v(-6.38, -8.26) * mm, "end": v(-6.38, -8.3) * mm});
            skLineSegment(sketch, "E471", {"start": v(-6.38, -8.3) * mm, "end": v(-6.39, -8.34) * mm});
            skLineSegment(sketch, "E472", {"start": v(-6.39, -8.34) * mm, "end": v(-6.4, -8.39) * mm});
            skLineSegment(sketch, "E473", {"start": v(-6.4, -8.39) * mm, "end": v(-6.4, -8.43) * mm});
            skLineSegment(sketch, "E474", {"start": v(-6.4, -8.43) * mm, "end": v(-6.4, -8.47) * mm});
            skLineSegment(sketch, "E475", {"start": v(-6.4, -8.47) * mm, "end": v(-6.42, -8.5) * mm});
            skLineSegment(sketch, "E476", {"start": v(-6.42, -8.5) * mm, "end": v(-6.43, -8.55) * mm});
            skLineSegment(sketch, "E477", {"start": v(-6.43, -8.55) * mm, "end": v(-6.45, -8.58) * mm});
            skLineSegment(sketch, "E478", {"start": v(-6.45, -8.58) * mm, "end": v(-6.47, -8.62) * mm});
            skLineSegment(sketch, "E479", {"start": v(-6.47, -8.62) * mm, "end": v(-6.49, -8.66) * mm});
            skLineSegment(sketch, "E480", {"start": v(-6.49, -8.66) * mm, "end": v(-6.5, -8.7) * mm});
            skLineSegment(sketch, "E481", {"start": v(-6.5, -8.7) * mm, "end": v(-6.53, -8.73) * mm});
            skLineSegment(sketch, "E482", {"start": v(-6.53, -8.73) * mm, "end": v(-6.56, -8.76) * mm});
            skLineSegment(sketch, "E483", {"start": v(-6.56, -8.76) * mm, "end": v(-6.6, -8.79) * mm});
            skLineSegment(sketch, "E484", {"start": v(-6.6, -8.79) * mm, "end": v(-6.62, -8.82) * mm});
            skLineSegment(sketch, "E485", {"start": v(-6.62, -8.82) * mm, "end": v(-6.66, -8.85) * mm});
            skLineSegment(sketch, "E486", {"start": v(-6.66, -8.85) * mm, "end": v(-7.73, -8.87) * mm});
            skLineSegment(sketch, "E487", {"start": v(-7.73, -8.87) * mm, "end": v(-7.73, -7.3) * mm});
            skLineSegment(sketch, "E488", {"start": v(-26.38, -9.67) * mm, "end": v(-26.27, -9.66) * mm});
            skLineSegment(sketch, "E489", {"start": v(-26.27, -9.66) * mm, "end": v(-26.08, -9.64) * mm});
            skLineSegment(sketch, "E490", {"start": v(-26.08, -9.64) * mm, "end": v(-25.28, -9.63) * mm});
            skLineSegment(sketch, "E491", {"start": v(-25.28, -9.63) * mm, "end": v(-25.3, -11.2) * mm});
            skLineSegment(sketch, "E492", {"start": v(-25.3, -11.2) * mm, "end": v(-26.03, -11.2) * mm});
            skLineSegment(sketch, "E493", {"start": v(-26.03, -11.2) * mm, "end": v(-26.17, -11.2) * mm});
            skLineSegment(sketch, "E494", {"start": v(-26.17, -11.2) * mm, "end": v(-26.27, -11.19) * mm});
            skLineSegment(sketch, "E495", {"start": v(-26.27, -11.19) * mm, "end": v(-26.3, -11.18) * mm});
            skLineSegment(sketch, "E496", {"start": v(-26.3, -11.18) * mm, "end": v(-26.34, -11.17) * mm});
            skLineSegment(sketch, "E497", {"start": v(-26.34, -11.17) * mm, "end": v(-26.36, -11.16) * mm});
            skLineSegment(sketch, "E498", {"start": v(-26.36, -11.16) * mm, "end": v(-26.39, -11.15) * mm});
            skLineSegment(sketch, "E499", {"start": v(-26.39, -11.15) * mm, "end": v(-26.41, -11.13) * mm});
            skLineSegment(sketch, "E500", {"start": v(-26.41, -11.13) * mm, "end": v(-26.43, -11.11) * mm});
            skLineSegment(sketch, "E501", {"start": v(-26.43, -11.11) * mm, "end": v(-26.46, -11.1) * mm});
            skLineSegment(sketch, "E502", {"start": v(-26.46, -11.1) * mm, "end": v(-26.47, -11.08) * mm});
            skLineSegment(sketch, "E503", {"start": v(-26.47, -11.08) * mm, "end": v(-26.5, -11.05) * mm});
            skLineSegment(sketch, "E504", {"start": v(-26.5, -11.05) * mm, "end": v(-26.5, -11.03) * mm});
            skLineSegment(sketch, "E505", {"start": v(-26.5, -11.03) * mm, "end": v(-26.52, -11) * mm});
            skLineSegment(sketch, "E506", {"start": v(-26.52, -11) * mm, "end": v(-26.54, -10.98) * mm});
            skLineSegment(sketch, "E507", {"start": v(-26.54, -10.98) * mm, "end": v(-26.55, -10.95) * mm});
            skLineSegment(sketch, "E508", {"start": v(-26.55, -10.95) * mm, "end": v(-26.56, -10.93) * mm});
            skLineSegment(sketch, "E509", {"start": v(-26.56, -10.93) * mm, "end": v(-26.57, -10.9) * mm});
            skLineSegment(sketch, "E510", {"start": v(-26.57, -10.9) * mm, "end": v(-26.58, -10.87) * mm});
            skLineSegment(sketch, "E511", {"start": v(-26.58, -10.87) * mm, "end": v(-26.59, -10.84) * mm});
            skLineSegment(sketch, "E512", {"start": v(-26.59, -10.84) * mm, "end": v(-26.6, -10.78) * mm});
            skLineSegment(sketch, "E513", {"start": v(-26.6, -10.78) * mm, "end": v(-26.61, -10.72) * mm});
            skLineSegment(sketch, "E514", {"start": v(-26.61, -10.72) * mm, "end": v(-26.62, -10.63) * mm});
            skLineSegment(sketch, "E515", {"start": v(-26.62, -10.63) * mm, "end": v(-26.63, -10.55) * mm});
            skLineSegment(sketch, "E516", {"start": v(-26.63, -10.55) * mm, "end": v(-26.63, -10.5) * mm});
            skLineSegment(sketch, "E517", {"start": v(-26.63, -10.5) * mm, "end": v(-26.63, -10.47) * mm});
            skLineSegment(sketch, "E518", {"start": v(-26.63, -10.47) * mm, "end": v(-26.63, -10.38) * mm});
            skLineSegment(sketch, "E519", {"start": v(-26.63, -10.38) * mm, "end": v(-26.62, -10.23) * mm});
            skLineSegment(sketch, "E520", {"start": v(-26.62, -10.23) * mm, "end": v(-26.62, -10.14) * mm});
            skLineSegment(sketch, "E521", {"start": v(-26.62, -10.14) * mm, "end": v(-26.6, -10.08) * mm});
            skLineSegment(sketch, "E522", {"start": v(-26.6, -10.08) * mm, "end": v(-26.6, -10.02) * mm});
            skLineSegment(sketch, "E523", {"start": v(-26.6, -10.02) * mm, "end": v(-26.59, -9.99) * mm});
            skLineSegment(sketch, "E524", {"start": v(-26.59, -9.99) * mm, "end": v(-26.58, -9.96) * mm});
            skLineSegment(sketch, "E525", {"start": v(-26.58, -9.96) * mm, "end": v(-26.57, -9.93) * mm});
            skLineSegment(sketch, "E526", {"start": v(-26.57, -9.93) * mm, "end": v(-26.56, -9.9) * mm});
            skLineSegment(sketch, "E527", {"start": v(-26.56, -9.9) * mm, "end": v(-26.55, -9.87) * mm});
            skLineSegment(sketch, "E528", {"start": v(-26.55, -9.87) * mm, "end": v(-26.54, -9.85) * mm});
            skLineSegment(sketch, "E529", {"start": v(-26.54, -9.85) * mm, "end": v(-26.52, -9.82) * mm});
            skLineSegment(sketch, "E530", {"start": v(-26.52, -9.82) * mm, "end": v(-26.5, -9.8) * mm});
            skLineSegment(sketch, "E531", {"start": v(-26.5, -9.8) * mm, "end": v(-26.49, -9.77) * mm});
            skLineSegment(sketch, "E532", {"start": v(-26.49, -9.77) * mm, "end": v(-26.47, -9.75) * mm});
            skLineSegment(sketch, "E533", {"start": v(-26.47, -9.75) * mm, "end": v(-26.45, -9.73) * mm});
            skLineSegment(sketch, "E534", {"start": v(-26.45, -9.73) * mm, "end": v(-26.43, -9.71) * mm});
            skLineSegment(sketch, "E535", {"start": v(-26.43, -9.71) * mm, "end": v(-26.4, -9.7) * mm});
            skLineSegment(sketch, "E536", {"start": v(-26.4, -9.7) * mm, "end": v(-26.38, -9.67) * mm});
            skLineSegment(sketch, "E537", {"start": v(-7.73, -9.64) * mm, "end": v(-6.54, -9.67) * mm});
            skLineSegment(sketch, "E538", {"start": v(-6.54, -9.67) * mm, "end": v(-6.51, -9.75) * mm});
            skLineSegment(sketch, "E539", {"start": v(-6.51, -9.75) * mm, "end": v(-6.48, -9.83) * mm});
            skLineSegment(sketch, "E540", {"start": v(-6.48, -9.83) * mm, "end": v(-6.46, -9.9) * mm});
            skLineSegment(sketch, "E541", {"start": v(-6.46, -9.9) * mm, "end": v(-6.44, -9.99) * mm});
            skLineSegment(sketch, "E542", {"start": v(-6.44, -9.99) * mm, "end": v(-6.42, -10.07) * mm});
            skLineSegment(sketch, "E543", {"start": v(-6.42, -10.07) * mm, "end": v(-6.4, -10.15) * mm});
            skLineSegment(sketch, "E544", {"start": v(-6.4, -10.15) * mm, "end": v(-6.4, -10.23) * mm});
            skLineSegment(sketch, "E545", {"start": v(-6.4, -10.23) * mm, "end": v(-6.39, -10.32) * mm});
            skLineSegment(sketch, "E546", {"start": v(-6.39, -10.32) * mm, "end": v(-6.38, -10.4) * mm});
            skLineSegment(sketch, "E547", {"start": v(-6.38, -10.4) * mm, "end": v(-6.38, -10.44) * mm});
            skLineSegment(sketch, "E548", {"start": v(-6.38, -10.44) * mm, "end": v(-6.38, -10.48) * mm});
            skLineSegment(sketch, "E549", {"start": v(-6.38, -10.48) * mm, "end": v(-6.38, -10.53) * mm});
            skLineSegment(sketch, "E550", {"start": v(-6.38, -10.53) * mm, "end": v(-6.39, -10.57) * mm});
            skLineSegment(sketch, "E551", {"start": v(-6.39, -10.57) * mm, "end": v(-6.39, -10.6) * mm});
            skLineSegment(sketch, "E552", {"start": v(-6.39, -10.6) * mm, "end": v(-6.4, -10.65) * mm});
            skLineSegment(sketch, "E553", {"start": v(-6.4, -10.65) * mm, "end": v(-6.4, -10.7) * mm});
            skLineSegment(sketch, "E554", {"start": v(-6.4, -10.7) * mm, "end": v(-6.4, -10.73) * mm});
            skLineSegment(sketch, "E555", {"start": v(-6.4, -10.73) * mm, "end": v(-6.41, -10.77) * mm});
            skLineSegment(sketch, "E556", {"start": v(-6.41, -10.77) * mm, "end": v(-6.42, -10.82) * mm});
            skLineSegment(sketch, "E557", {"start": v(-6.42, -10.82) * mm, "end": v(-6.43, -10.86) * mm});
            skLineSegment(sketch, "E558", {"start": v(-6.43, -10.86) * mm, "end": v(-6.45, -10.92) * mm});
            skLineSegment(sketch, "E559", {"start": v(-6.45, -10.92) * mm, "end": v(-6.47, -10.97) * mm});
            skLineSegment(sketch, "E560", {"start": v(-6.47, -10.97) * mm, "end": v(-6.5, -11.03) * mm});
            skLineSegment(sketch, "E561", {"start": v(-6.5, -11.03) * mm, "end": v(-6.53, -11.07) * mm});
            skLineSegment(sketch, "E562", {"start": v(-6.53, -11.07) * mm, "end": v(-6.56, -11.1) * mm});
            skLineSegment(sketch, "E563", {"start": v(-6.56, -11.1) * mm, "end": v(-6.58, -11.12) * mm});
            skLineSegment(sketch, "E564", {"start": v(-6.58, -11.12) * mm, "end": v(-6.6, -11.14) * mm});
            skLineSegment(sketch, "E565", {"start": v(-6.6, -11.14) * mm, "end": v(-6.64, -11.15) * mm});
            skLineSegment(sketch, "E566", {"start": v(-6.64, -11.15) * mm, "end": v(-6.66, -11.17) * mm});
            skLineSegment(sketch, "E567", {"start": v(-6.66, -11.17) * mm, "end": v(-6.7, -11.18) * mm});
            skLineSegment(sketch, "E568", {"start": v(-6.7, -11.18) * mm, "end": v(-6.7, -11.18) * mm});
            skLineSegment(sketch, "E569", {"start": v(-6.7, -11.18) * mm, "end": v(-7.72, -11.2) * mm});
            skLineSegment(sketch, "E570", {"start": v(-7.72, -11.2) * mm, "end": v(-7.73, -9.64) * mm});
            skLineSegment(sketch, "E571", {"start": v(-26.47, -12.01) * mm, "end": v(-25.28, -11.98) * mm});
            skLineSegment(sketch, "E572", {"start": v(-25.28, -11.98) * mm, "end": v(-25.3, -13.53) * mm});
            skLineSegment(sketch, "E573", {"start": v(-25.3, -13.53) * mm, "end": v(-25.33, -13.53) * mm});
            skLineSegment(sketch, "E574", {"start": v(-25.33, -13.53) * mm, "end": v(-25.38, -13.52) * mm});
            skLineSegment(sketch, "E575", {"start": v(-25.38, -13.52) * mm, "end": v(-25.42, -13.52) * mm});
            skLineSegment(sketch, "E576", {"start": v(-25.42, -13.52) * mm, "end": v(-25.47, -13.52) * mm});
            skLineSegment(sketch, "E577", {"start": v(-25.47, -13.52) * mm, "end": v(-25.5, -13.52) * mm});
            skLineSegment(sketch, "E578", {"start": v(-25.5, -13.52) * mm, "end": v(-25.6, -13.53) * mm});
            skLineSegment(sketch, "E579", {"start": v(-25.6, -13.53) * mm, "end": v(-25.88, -13.56) * mm});
            skLineSegment(sketch, "E580", {"start": v(-25.88, -13.56) * mm, "end": v(-25.93, -13.56) * mm});
            skLineSegment(sketch, "E581", {"start": v(-25.93, -13.56) * mm, "end": v(-25.97, -13.56) * mm});
            skLineSegment(sketch, "E582", {"start": v(-25.97, -13.56) * mm, "end": v(-26.02, -13.56) * mm});
            skLineSegment(sketch, "E583", {"start": v(-26.02, -13.56) * mm, "end": v(-26.06, -13.56) * mm});
            skLineSegment(sketch, "E584", {"start": v(-26.06, -13.56) * mm, "end": v(-26.1, -13.56) * mm});
            skLineSegment(sketch, "E585", {"start": v(-26.1, -13.56) * mm, "end": v(-26.15, -13.56) * mm});
            skLineSegment(sketch, "E586", {"start": v(-26.15, -13.56) * mm, "end": v(-26.2, -13.55) * mm});
            skLineSegment(sketch, "E587", {"start": v(-26.2, -13.55) * mm, "end": v(-26.24, -13.54) * mm});
            skLineSegment(sketch, "E588", {"start": v(-26.24, -13.54) * mm, "end": v(-26.28, -13.53) * mm});
            skLineSegment(sketch, "E589", {"start": v(-26.28, -13.53) * mm, "end": v(-26.32, -13.52) * mm});
            skLineSegment(sketch, "E590", {"start": v(-26.32, -13.52) * mm, "end": v(-26.36, -13.5) * mm});
            skLineSegment(sketch, "E591", {"start": v(-26.36, -13.5) * mm, "end": v(-26.4, -13.48) * mm});
            skLineSegment(sketch, "E592", {"start": v(-26.4, -13.48) * mm, "end": v(-26.43, -13.45) * mm});
            skLineSegment(sketch, "E593", {"start": v(-26.43, -13.45) * mm, "end": v(-26.46, -13.43) * mm});
            skLineSegment(sketch, "E594", {"start": v(-26.46, -13.43) * mm, "end": v(-26.5, -13.4) * mm});
            skLineSegment(sketch, "E595", {"start": v(-26.5, -13.4) * mm, "end": v(-26.53, -13.36) * mm});
            skLineSegment(sketch, "E596", {"start": v(-26.53, -13.36) * mm, "end": v(-26.55, -13.31) * mm});
            skLineSegment(sketch, "E597", {"start": v(-26.55, -13.31) * mm, "end": v(-26.56, -13.27) * mm});
            skLineSegment(sketch, "E598", {"start": v(-26.56, -13.27) * mm, "end": v(-26.57, -13.22) * mm});
            skLineSegment(sketch, "E599", {"start": v(-26.57, -13.22) * mm, "end": v(-26.59, -13.18) * mm});
            skLineSegment(sketch, "E600", {"start": v(-26.59, -13.18) * mm, "end": v(-26.6, -13.13) * mm});
            skLineSegment(sketch, "E601", {"start": v(-26.6, -13.13) * mm, "end": v(-26.6, -13.08) * mm});
            skLineSegment(sketch, "E602", {"start": v(-26.6, -13.08) * mm, "end": v(-26.61, -13.04) * mm});
            skLineSegment(sketch, "E603", {"start": v(-26.61, -13.04) * mm, "end": v(-26.62, -12.99) * mm});
            skLineSegment(sketch, "E604", {"start": v(-26.62, -12.99) * mm, "end": v(-26.63, -12.94) * mm});
            skLineSegment(sketch, "E605", {"start": v(-26.63, -12.94) * mm, "end": v(-26.63, -12.9) * mm});
            skLineSegment(sketch, "E606", {"start": v(-26.63, -12.9) * mm, "end": v(-26.63, -12.85) * mm});
            skLineSegment(sketch, "E607", {"start": v(-26.63, -12.85) * mm, "end": v(-26.63, -12.8) * mm});
            skLineSegment(sketch, "E608", {"start": v(-26.63, -12.8) * mm, "end": v(-26.63, -12.75) * mm});
            skLineSegment(sketch, "E609", {"start": v(-26.63, -12.75) * mm, "end": v(-26.63, -12.7) * mm});
            skLineSegment(sketch, "E610", {"start": v(-26.63, -12.7) * mm, "end": v(-26.63, -12.66) * mm});
            skLineSegment(sketch, "E611", {"start": v(-26.63, -12.66) * mm, "end": v(-26.62, -12.6) * mm});
            skLineSegment(sketch, "E612", {"start": v(-26.62, -12.6) * mm, "end": v(-26.62, -12.56) * mm});
            skLineSegment(sketch, "E613", {"start": v(-26.62, -12.56) * mm, "end": v(-26.61, -12.51) * mm});
            skLineSegment(sketch, "E614", {"start": v(-26.61, -12.51) * mm, "end": v(-26.6, -12.47) * mm});
            skLineSegment(sketch, "E615", {"start": v(-26.6, -12.47) * mm, "end": v(-26.6, -12.42) * mm});
            skLineSegment(sketch, "E616", {"start": v(-26.6, -12.42) * mm, "end": v(-26.59, -12.37) * mm});
            skLineSegment(sketch, "E617", {"start": v(-26.59, -12.37) * mm, "end": v(-26.58, -12.33) * mm});
            skLineSegment(sketch, "E618", {"start": v(-26.58, -12.33) * mm, "end": v(-26.56, -12.28) * mm});
            skLineSegment(sketch, "E619", {"start": v(-26.56, -12.28) * mm, "end": v(-26.55, -12.23) * mm});
            skLineSegment(sketch, "E620", {"start": v(-26.55, -12.23) * mm, "end": v(-26.54, -12.19) * mm});
            skLineSegment(sketch, "E621", {"start": v(-26.54, -12.19) * mm, "end": v(-26.52, -12.14) * mm});
            skLineSegment(sketch, "E622", {"start": v(-26.52, -12.14) * mm, "end": v(-26.5, -12.1) * mm});
            skLineSegment(sketch, "E623", {"start": v(-26.5, -12.1) * mm, "end": v(-26.49, -12.05) * mm});
            skLineSegment(sketch, "E624", {"start": v(-26.49, -12.05) * mm, "end": v(-26.47, -12.01) * mm});
            skLineSegment(sketch, "E625", {"start": v(-7.73, -11.98) * mm, "end": v(-6.54, -12.01) * mm});
            skLineSegment(sketch, "E626", {"start": v(-6.54, -12.01) * mm, "end": v(-6.52, -12.06) * mm});
            skLineSegment(sketch, "E627", {"start": v(-6.52, -12.06) * mm, "end": v(-6.5, -12.1) * mm});
            skLineSegment(sketch, "E628", {"start": v(-6.5, -12.1) * mm, "end": v(-6.49, -12.16) * mm});
            skLineSegment(sketch, "E629", {"start": v(-6.49, -12.16) * mm, "end": v(-6.47, -12.2) * mm});
            skLineSegment(sketch, "E630", {"start": v(-6.47, -12.2) * mm, "end": v(-6.46, -12.26) * mm});
            skLineSegment(sketch, "E631", {"start": v(-6.46, -12.26) * mm, "end": v(-6.44, -12.31) * mm});
            skLineSegment(sketch, "E632", {"start": v(-6.44, -12.31) * mm, "end": v(-6.43, -12.37) * mm});
            skLineSegment(sketch, "E633", {"start": v(-6.43, -12.37) * mm, "end": v(-6.42, -12.42) * mm});
            skLineSegment(sketch, "E634", {"start": v(-6.42, -12.42) * mm, "end": v(-6.4, -12.48) * mm});
            skLineSegment(sketch, "E635", {"start": v(-6.4, -12.48) * mm, "end": v(-6.4, -12.53) * mm});
            skLineSegment(sketch, "E636", {"start": v(-6.4, -12.53) * mm, "end": v(-6.39, -12.59) * mm});
            skLineSegment(sketch, "E637", {"start": v(-6.39, -12.59) * mm, "end": v(-6.38, -12.64) * mm});
            skLineSegment(sketch, "E638", {"start": v(-6.38, -12.64) * mm, "end": v(-6.38, -12.7) * mm});
            skLineSegment(sketch, "E639", {"start": v(-6.38, -12.7) * mm, "end": v(-6.37, -12.75) * mm});
            skLineSegment(sketch, "E640", {"start": v(-6.37, -12.75) * mm, "end": v(-6.37, -12.8) * mm});
            skLineSegment(sketch, "E641", {"start": v(-6.37, -12.8) * mm, "end": v(-6.37, -12.86) * mm});
            skLineSegment(sketch, "E642", {"start": v(-6.37, -12.86) * mm, "end": v(-6.38, -12.91) * mm});
            skLineSegment(sketch, "E643", {"start": v(-6.38, -12.91) * mm, "end": v(-6.38, -12.97) * mm});
            skLineSegment(sketch, "E644", {"start": v(-6.38, -12.97) * mm, "end": v(-6.39, -13.02) * mm});
            skLineSegment(sketch, "E645", {"start": v(-6.39, -13.02) * mm, "end": v(-6.4, -13.07) * mm});
            skLineSegment(sketch, "E646", {"start": v(-6.4, -13.07) * mm, "end": v(-6.4, -13.12) * mm});
            skLineSegment(sketch, "E647", {"start": v(-6.4, -13.12) * mm, "end": v(-6.42, -13.17) * mm});
            skLineSegment(sketch, "E648", {"start": v(-6.42, -13.17) * mm, "end": v(-6.44, -13.22) * mm});
            skLineSegment(sketch, "E649", {"start": v(-6.44, -13.22) * mm, "end": v(-6.46, -13.27) * mm});
            skLineSegment(sketch, "E650", {"start": v(-6.46, -13.27) * mm, "end": v(-6.49, -13.32) * mm});
            skLineSegment(sketch, "E651", {"start": v(-6.49, -13.32) * mm, "end": v(-6.51, -13.36) * mm});
            skLineSegment(sketch, "E652", {"start": v(-6.51, -13.36) * mm, "end": v(-6.54, -13.4) * mm});
            skLineSegment(sketch, "E653", {"start": v(-6.54, -13.4) * mm, "end": v(-6.58, -13.45) * mm});
            skLineSegment(sketch, "E654", {"start": v(-6.58, -13.45) * mm, "end": v(-6.61, -13.49) * mm});
            skLineSegment(sketch, "E655", {"start": v(-6.61, -13.49) * mm, "end": v(-6.65, -13.5) * mm});
            skLineSegment(sketch, "E656", {"start": v(-6.65, -13.5) * mm, "end": v(-6.69, -13.5) * mm});
            skLineSegment(sketch, "E657", {"start": v(-6.69, -13.5) * mm, "end": v(-6.72, -13.52) * mm});
            skLineSegment(sketch, "E658", {"start": v(-6.72, -13.52) * mm, "end": v(-6.76, -13.52) * mm});
            skLineSegment(sketch, "E659", {"start": v(-6.76, -13.52) * mm, "end": v(-6.8, -13.53) * mm});
            skLineSegment(sketch, "E660", {"start": v(-6.8, -13.53) * mm, "end": v(-6.87, -13.54) * mm});
            skLineSegment(sketch, "E661", {"start": v(-6.87, -13.54) * mm, "end": v(-6.95, -13.55) * mm});
            skLineSegment(sketch, "E662", {"start": v(-6.95, -13.55) * mm, "end": v(-7.06, -13.55) * mm});
            skLineSegment(sketch, "E663", {"start": v(-7.06, -13.55) * mm, "end": v(-7.6, -13.53) * mm});
            skLineSegment(sketch, "E664", {"start": v(-7.6, -13.53) * mm, "end": v(-7.72, -13.53) * mm});
            skLineSegment(sketch, "E665", {"start": v(-7.72, -13.53) * mm, "end": v(-7.73, -11.98) * mm});
            skLineSegment(sketch, "E666", {"start": v(-20.77, -15.27) * mm, "end": v(-19.21, -15.27) * mm});
            skLineSegment(sketch, "E667", {"start": v(-19.21, -15.27) * mm, "end": v(-19.21, -16.13) * mm});
            skLineSegment(sketch, "E668", {"start": v(-19.21, -16.13) * mm, "end": v(-19.22, -16.27) * mm});
            skLineSegment(sketch, "E669", {"start": v(-19.22, -16.27) * mm, "end": v(-19.23, -16.29) * mm});
            skLineSegment(sketch, "E670", {"start": v(-19.23, -16.29) * mm, "end": v(-19.23, -16.3) * mm});
            skLineSegment(sketch, "E671", {"start": v(-19.23, -16.3) * mm, "end": v(-19.24, -16.32) * mm});
            skLineSegment(sketch, "E672", {"start": v(-19.24, -16.32) * mm, "end": v(-19.24, -16.34) * mm});
            skLineSegment(sketch, "E673", {"start": v(-19.24, -16.34) * mm, "end": v(-19.25, -16.35) * mm});
            skLineSegment(sketch, "E674", {"start": v(-19.25, -16.35) * mm, "end": v(-19.26, -16.37) * mm});
            skLineSegment(sketch, "E675", {"start": v(-19.26, -16.37) * mm, "end": v(-19.27, -16.38) * mm});
            skLineSegment(sketch, "E676", {"start": v(-19.27, -16.38) * mm, "end": v(-19.28, -16.4) * mm});
            skLineSegment(sketch, "E677", {"start": v(-19.28, -16.4) * mm, "end": v(-19.3, -16.41) * mm});
            skLineSegment(sketch, "E678", {"start": v(-19.3, -16.41) * mm, "end": v(-19.32, -16.43) * mm});
            skLineSegment(sketch, "E679", {"start": v(-19.32, -16.43) * mm, "end": v(-19.34, -16.46) * mm});
            skLineSegment(sketch, "E680", {"start": v(-19.34, -16.46) * mm, "end": v(-19.39, -16.49) * mm});
            skLineSegment(sketch, "E681", {"start": v(-19.39, -16.49) * mm, "end": v(-19.47, -16.53) * mm});
            skLineSegment(sketch, "E682", {"start": v(-19.47, -16.53) * mm, "end": v(-19.6, -16.58) * mm});
            skLineSegment(sketch, "E683", {"start": v(-19.6, -16.58) * mm, "end": v(-19.69, -16.6) * mm});
            skLineSegment(sketch, "E684", {"start": v(-19.69, -16.6) * mm, "end": v(-19.73, -16.6) * mm});
            skLineSegment(sketch, "E685", {"start": v(-19.73, -16.6) * mm, "end": v(-19.77, -16.6) * mm});
            skLineSegment(sketch, "E686", {"start": v(-19.77, -16.6) * mm, "end": v(-19.81, -16.61) * mm});
            skLineSegment(sketch, "E687", {"start": v(-19.81, -16.61) * mm, "end": v(-19.86, -16.62) * mm});
            skLineSegment(sketch, "E688", {"start": v(-19.86, -16.62) * mm, "end": v(-19.9, -16.62) * mm});
            skLineSegment(sketch, "E689", {"start": v(-19.9, -16.62) * mm, "end": v(-19.94, -16.62) * mm});
            skLineSegment(sketch, "E690", {"start": v(-19.94, -16.62) * mm, "end": v(-19.98, -16.62) * mm});
            skLineSegment(sketch, "E691", {"start": v(-19.98, -16.62) * mm, "end": v(-20.03, -16.62) * mm});
            skLineSegment(sketch, "E692", {"start": v(-20.03, -16.62) * mm, "end": v(-20.07, -16.62) * mm});
            skLineSegment(sketch, "E693", {"start": v(-20.07, -16.62) * mm, "end": v(-20.11, -16.62) * mm});
            skLineSegment(sketch, "E694", {"start": v(-20.11, -16.62) * mm, "end": v(-20.15, -16.62) * mm});
            skLineSegment(sketch, "E695", {"start": v(-20.15, -16.62) * mm, "end": v(-20.2, -16.61) * mm});
            skLineSegment(sketch, "E696", {"start": v(-20.2, -16.61) * mm, "end": v(-20.24, -16.6) * mm});
            skLineSegment(sketch, "E697", {"start": v(-20.24, -16.6) * mm, "end": v(-20.28, -16.6) * mm});
            skLineSegment(sketch, "E698", {"start": v(-20.28, -16.6) * mm, "end": v(-20.32, -16.6) * mm});
            skLineSegment(sketch, "E699", {"start": v(-20.32, -16.6) * mm, "end": v(-20.36, -16.58) * mm});
            skLineSegment(sketch, "E700", {"start": v(-20.36, -16.58) * mm, "end": v(-20.4, -16.57) * mm});
            skLineSegment(sketch, "E701", {"start": v(-20.4, -16.57) * mm, "end": v(-20.44, -16.56) * mm});
            skLineSegment(sketch, "E702", {"start": v(-20.44, -16.56) * mm, "end": v(-20.48, -16.54) * mm});
            skLineSegment(sketch, "E703", {"start": v(-20.48, -16.54) * mm, "end": v(-20.52, -16.53) * mm});
            skLineSegment(sketch, "E704", {"start": v(-20.52, -16.53) * mm, "end": v(-20.56, -16.51) * mm});
            skLineSegment(sketch, "E705", {"start": v(-20.56, -16.51) * mm, "end": v(-20.6, -16.5) * mm});
            skLineSegment(sketch, "E706", {"start": v(-20.6, -16.5) * mm, "end": v(-20.64, -16.47) * mm});
            skLineSegment(sketch, "E707", {"start": v(-20.64, -16.47) * mm, "end": v(-20.68, -16.45) * mm});
            skLineSegment(sketch, "E708", {"start": v(-20.68, -16.45) * mm, "end": v(-20.71, -16.43) * mm});
            skLineSegment(sketch, "E709", {"start": v(-20.71, -16.43) * mm, "end": v(-20.75, -16.4) * mm});
            skLineSegment(sketch, "E710", {"start": v(-20.75, -16.4) * mm, "end": v(-20.78, -16.38) * mm});
            skLineSegment(sketch, "E711", {"start": v(-20.78, -16.38) * mm, "end": v(-20.77, -15.27) * mm});
            skLineSegment(sketch, "E712", {"start": v(-18.48, -15.27) * mm, "end": v(-16.91, -15.27) * mm});
            skLineSegment(sketch, "E713", {"start": v(-16.91, -15.27) * mm, "end": v(-16.89, -16.15) * mm});
            skLineSegment(sketch, "E714", {"start": v(-16.89, -16.15) * mm, "end": v(-16.9, -16.21) * mm});
            skLineSegment(sketch, "E715", {"start": v(-16.9, -16.21) * mm, "end": v(-16.9, -16.27) * mm});
            skLineSegment(sketch, "E716", {"start": v(-16.9, -16.27) * mm, "end": v(-16.93, -16.32) * mm});
            skLineSegment(sketch, "E717", {"start": v(-16.93, -16.32) * mm, "end": v(-16.96, -16.37) * mm});
            skLineSegment(sketch, "E718", {"start": v(-16.96, -16.37) * mm, "end": v(-17, -16.42) * mm});
            skLineSegment(sketch, "E719", {"start": v(-17, -16.42) * mm, "end": v(-17.02, -16.45) * mm});
            skLineSegment(sketch, "E720", {"start": v(-17.02, -16.45) * mm, "end": v(-17.04, -16.47) * mm});
            skLineSegment(sketch, "E721", {"start": v(-17.04, -16.47) * mm, "end": v(-17.07, -16.5) * mm});
            skLineSegment(sketch, "E722", {"start": v(-17.07, -16.5) * mm, "end": v(-17.1, -16.52) * mm});
            skLineSegment(sketch, "E723", {"start": v(-17.1, -16.52) * mm, "end": v(-17.13, -16.54) * mm});
            skLineSegment(sketch, "E724", {"start": v(-17.13, -16.54) * mm, "end": v(-17.15, -16.55) * mm});
            skLineSegment(sketch, "E725", {"start": v(-17.15, -16.55) * mm, "end": v(-17.17, -16.56) * mm});
            skLineSegment(sketch, "E726", {"start": v(-17.17, -16.56) * mm, "end": v(-17.19, -16.56) * mm});
            skLineSegment(sketch, "E727", {"start": v(-17.19, -16.56) * mm, "end": v(-17.2, -16.57) * mm});
            skLineSegment(sketch, "E728", {"start": v(-17.2, -16.57) * mm, "end": v(-17.22, -16.57) * mm});
            skLineSegment(sketch, "E729", {"start": v(-17.22, -16.57) * mm, "end": v(-17.24, -16.57) * mm});
            skLineSegment(sketch, "E730", {"start": v(-17.24, -16.57) * mm, "end": v(-17.26, -16.58) * mm});
            skLineSegment(sketch, "E731", {"start": v(-17.26, -16.58) * mm, "end": v(-17.3, -16.58) * mm});
            skLineSegment(sketch, "E732", {"start": v(-17.3, -16.58) * mm, "end": v(-17.39, -16.6) * mm});
            skLineSegment(sketch, "E733", {"start": v(-17.39, -16.6) * mm, "end": v(-17.47, -16.61) * mm});
            skLineSegment(sketch, "E734", {"start": v(-17.47, -16.61) * mm, "end": v(-17.56, -16.62) * mm});
            skLineSegment(sketch, "E735", {"start": v(-17.56, -16.62) * mm, "end": v(-17.6, -16.62) * mm});
            skLineSegment(sketch, "E736", {"start": v(-17.6, -16.62) * mm, "end": v(-17.65, -16.63) * mm});
            skLineSegment(sketch, "E737", {"start": v(-17.65, -16.63) * mm, "end": v(-17.7, -16.63) * mm});
            skLineSegment(sketch, "E738", {"start": v(-17.7, -16.63) * mm, "end": v(-17.74, -16.63) * mm});
            skLineSegment(sketch, "E739", {"start": v(-17.74, -16.63) * mm, "end": v(-17.79, -16.63) * mm});
            skLineSegment(sketch, "E740", {"start": v(-17.79, -16.63) * mm, "end": v(-17.83, -16.62) * mm});
            skLineSegment(sketch, "E741", {"start": v(-17.83, -16.62) * mm, "end": v(-17.88, -16.62) * mm});
            skLineSegment(sketch, "E742", {"start": v(-17.88, -16.62) * mm, "end": v(-17.92, -16.61) * mm});
            skLineSegment(sketch, "E743", {"start": v(-17.92, -16.61) * mm, "end": v(-17.96, -16.6) * mm});
            skLineSegment(sketch, "E744", {"start": v(-17.96, -16.6) * mm, "end": v(-18, -16.6) * mm});
            skLineSegment(sketch, "E745", {"start": v(-18, -16.6) * mm, "end": v(-18.05, -16.59) * mm});
            skLineSegment(sketch, "E746", {"start": v(-18.05, -16.59) * mm, "end": v(-18.1, -16.57) * mm});
            skLineSegment(sketch, "E747", {"start": v(-18.1, -16.57) * mm, "end": v(-18.13, -16.56) * mm});
            skLineSegment(sketch, "E748", {"start": v(-18.13, -16.56) * mm, "end": v(-18.17, -16.54) * mm});
            skLineSegment(sketch, "E749", {"start": v(-18.17, -16.54) * mm, "end": v(-18.2, -16.52) * mm});
            skLineSegment(sketch, "E750", {"start": v(-18.2, -16.52) * mm, "end": v(-18.25, -16.5) * mm});
            skLineSegment(sketch, "E751", {"start": v(-18.25, -16.5) * mm, "end": v(-18.28, -16.48) * mm});
            skLineSegment(sketch, "E752", {"start": v(-18.28, -16.48) * mm, "end": v(-18.32, -16.45) * mm});
            skLineSegment(sketch, "E753", {"start": v(-18.32, -16.45) * mm, "end": v(-18.35, -16.42) * mm});
            skLineSegment(sketch, "E754", {"start": v(-18.35, -16.42) * mm, "end": v(-18.38, -16.39) * mm});
            skLineSegment(sketch, "E755", {"start": v(-18.38, -16.39) * mm, "end": v(-18.4, -16.35) * mm});
            skLineSegment(sketch, "E756", {"start": v(-18.4, -16.35) * mm, "end": v(-18.44, -16.32) * mm});
            skLineSegment(sketch, "E757", {"start": v(-18.44, -16.32) * mm, "end": v(-18.45, -16.25) * mm});
            skLineSegment(sketch, "E758", {"start": v(-18.45, -16.25) * mm, "end": v(-18.46, -16.14) * mm});
            skLineSegment(sketch, "E759", {"start": v(-18.46, -16.14) * mm, "end": v(-18.48, -15.96) * mm});
            skLineSegment(sketch, "E760", {"start": v(-18.48, -15.96) * mm, "end": v(-18.48, -15.27) * mm});
            skLineSegment(sketch, "E761", {"start": v(-16.1, -15.27) * mm, "end": v(-14.53, -15.27) * mm});
            skLineSegment(sketch, "E762", {"start": v(-14.53, -15.27) * mm, "end": v(-14.53, -15.99) * mm});
            skLineSegment(sketch, "E763", {"start": v(-14.53, -15.99) * mm, "end": v(-14.54, -16.16) * mm});
            skLineSegment(sketch, "E764", {"start": v(-14.54, -16.16) * mm, "end": v(-14.55, -16.26) * mm});
            skLineSegment(sketch, "E765", {"start": v(-14.55, -16.26) * mm, "end": v(-14.57, -16.3) * mm});
            skLineSegment(sketch, "E766", {"start": v(-14.57, -16.3) * mm, "end": v(-14.59, -16.33) * mm});
            skLineSegment(sketch, "E767", {"start": v(-14.59, -16.33) * mm, "end": v(-14.6, -16.36) * mm});
            skLineSegment(sketch, "E768", {"start": v(-14.6, -16.36) * mm, "end": v(-14.63, -16.38) * mm});
            skLineSegment(sketch, "E769", {"start": v(-14.63, -16.38) * mm, "end": v(-14.65, -16.41) * mm});
            skLineSegment(sketch, "E770", {"start": v(-14.65, -16.41) * mm, "end": v(-14.67, -16.44) * mm});
            skLineSegment(sketch, "E771", {"start": v(-14.67, -16.44) * mm, "end": v(-14.7, -16.46) * mm});
            skLineSegment(sketch, "E772", {"start": v(-14.7, -16.46) * mm, "end": v(-14.73, -16.48) * mm});
            skLineSegment(sketch, "E773", {"start": v(-14.73, -16.48) * mm, "end": v(-14.76, -16.5) * mm});
            skLineSegment(sketch, "E774", {"start": v(-14.76, -16.5) * mm, "end": v(-14.78, -16.52) * mm});
            skLineSegment(sketch, "E775", {"start": v(-14.78, -16.52) * mm, "end": v(-14.82, -16.53) * mm});
            skLineSegment(sketch, "E776", {"start": v(-14.82, -16.53) * mm, "end": v(-14.85, -16.55) * mm});
            skLineSegment(sketch, "E777", {"start": v(-14.85, -16.55) * mm, "end": v(-14.88, -16.56) * mm});
            skLineSegment(sketch, "E778", {"start": v(-14.88, -16.56) * mm, "end": v(-14.91, -16.57) * mm});
            skLineSegment(sketch, "E779", {"start": v(-14.91, -16.57) * mm, "end": v(-14.95, -16.58) * mm});
            skLineSegment(sketch, "E780", {"start": v(-14.95, -16.58) * mm, "end": v(-14.98, -16.59) * mm});
            skLineSegment(sketch, "E781", {"start": v(-14.98, -16.59) * mm, "end": v(-15.02, -16.6) * mm});
            skLineSegment(sketch, "E782", {"start": v(-15.02, -16.6) * mm, "end": v(-15.05, -16.6) * mm});
            skLineSegment(sketch, "E783", {"start": v(-15.05, -16.6) * mm, "end": v(-15.1, -16.6) * mm});
            skLineSegment(sketch, "E784", {"start": v(-15.1, -16.6) * mm, "end": v(-15.16, -16.61) * mm});
            skLineSegment(sketch, "E785", {"start": v(-15.16, -16.61) * mm, "end": v(-15.24, -16.62) * mm});
            skLineSegment(sketch, "E786", {"start": v(-15.24, -16.62) * mm, "end": v(-15.3, -16.62) * mm});
            skLineSegment(sketch, "E787", {"start": v(-15.3, -16.62) * mm, "end": v(-15.38, -16.62) * mm});
            skLineSegment(sketch, "E788", {"start": v(-15.38, -16.62) * mm, "end": v(-15.44, -16.61) * mm});
            skLineSegment(sketch, "E789", {"start": v(-15.44, -16.61) * mm, "end": v(-15.5, -16.62) * mm});
            skLineSegment(sketch, "E790", {"start": v(-15.5, -16.62) * mm, "end": v(-15.55, -16.61) * mm});
            skLineSegment(sketch, "E791", {"start": v(-15.55, -16.61) * mm, "end": v(-15.6, -16.6) * mm});
            skLineSegment(sketch, "E792", {"start": v(-15.6, -16.6) * mm, "end": v(-15.66, -16.6) * mm});
            skLineSegment(sketch, "E793", {"start": v(-15.66, -16.6) * mm, "end": v(-15.71, -16.59) * mm});
            skLineSegment(sketch, "E794", {"start": v(-15.71, -16.59) * mm, "end": v(-15.74, -16.58) * mm});
            skLineSegment(sketch, "E795", {"start": v(-15.74, -16.58) * mm, "end": v(-15.77, -16.57) * mm});
            skLineSegment(sketch, "E796", {"start": v(-15.77, -16.57) * mm, "end": v(-15.8, -16.56) * mm});
            skLineSegment(sketch, "E797", {"start": v(-15.8, -16.56) * mm, "end": v(-15.82, -16.55) * mm});
            skLineSegment(sketch, "E798", {"start": v(-15.82, -16.55) * mm, "end": v(-15.84, -16.54) * mm});
            skLineSegment(sketch, "E799", {"start": v(-15.84, -16.54) * mm, "end": v(-15.87, -16.53) * mm});
            skLineSegment(sketch, "E800", {"start": v(-15.87, -16.53) * mm, "end": v(-15.9, -16.52) * mm});
            skLineSegment(sketch, "E801", {"start": v(-15.9, -16.52) * mm, "end": v(-15.92, -16.5) * mm});
            skLineSegment(sketch, "E802", {"start": v(-15.92, -16.5) * mm, "end": v(-15.94, -16.49) * mm});
            skLineSegment(sketch, "E803", {"start": v(-15.94, -16.49) * mm, "end": v(-15.96, -16.47) * mm});
            skLineSegment(sketch, "E804", {"start": v(-15.96, -16.47) * mm, "end": v(-15.98, -16.46) * mm});
            skLineSegment(sketch, "E805", {"start": v(-15.98, -16.46) * mm, "end": v(-16, -16.44) * mm});
            skLineSegment(sketch, "E806", {"start": v(-16, -16.44) * mm, "end": v(-16.02, -16.42) * mm});
            skLineSegment(sketch, "E807", {"start": v(-16.02, -16.42) * mm, "end": v(-16.04, -16.4) * mm});
            skLineSegment(sketch, "E808", {"start": v(-16.04, -16.4) * mm, "end": v(-16.05, -16.38) * mm});
            skLineSegment(sketch, "E809", {"start": v(-16.05, -16.38) * mm, "end": v(-16.07, -16.35) * mm});
            skLineSegment(sketch, "E810", {"start": v(-16.07, -16.35) * mm, "end": v(-16.08, -16.33) * mm});
            skLineSegment(sketch, "E811", {"start": v(-16.08, -16.33) * mm, "end": v(-16.1, -16.3) * mm});
            skLineSegment(sketch, "E812", {"start": v(-16.1, -16.3) * mm, "end": v(-16.1, -16.28) * mm});
            skLineSegment(sketch, "E813", {"start": v(-16.1, -16.28) * mm, "end": v(-16.12, -16.18) * mm});
            skLineSegment(sketch, "E814", {"start": v(-16.12, -16.18) * mm, "end": v(-16.13, -16.04) * mm});
            skLineSegment(sketch, "E815", {"start": v(-16.13, -16.04) * mm, "end": v(-16.13, -15.76) * mm});
            skLineSegment(sketch, "E816", {"start": v(-16.13, -15.76) * mm, "end": v(-16.1, -15.27) * mm});
            skLineSegment(sketch, "E817", {"start": v(-13.8, -15.27) * mm, "end": v(-12.24, -15.27) * mm});
            skLineSegment(sketch, "E818", {"start": v(-12.24, -15.27) * mm, "end": v(-12.23, -16.38) * mm});
            skLineSegment(sketch, "E819", {"start": v(-12.23, -16.38) * mm, "end": v(-12.27, -16.4) * mm});
            skLineSegment(sketch, "E820", {"start": v(-12.27, -16.4) * mm, "end": v(-12.3, -16.43) * mm});
            skLineSegment(sketch, "E821", {"start": v(-12.3, -16.43) * mm, "end": v(-12.34, -16.45) * mm});
            skLineSegment(sketch, "E822", {"start": v(-12.34, -16.45) * mm, "end": v(-12.38, -16.48) * mm});
            skLineSegment(sketch, "E823", {"start": v(-12.38, -16.48) * mm, "end": v(-12.42, -16.5) * mm});
            skLineSegment(sketch, "E824", {"start": v(-12.42, -16.5) * mm, "end": v(-12.46, -16.51) * mm});
            skLineSegment(sketch, "E825", {"start": v(-12.46, -16.51) * mm, "end": v(-12.5, -16.53) * mm});
            skLineSegment(sketch, "E826", {"start": v(-12.5, -16.53) * mm, "end": v(-12.54, -16.55) * mm});
            skLineSegment(sketch, "E827", {"start": v(-12.54, -16.55) * mm, "end": v(-12.58, -16.56) * mm});
            skLineSegment(sketch, "E828", {"start": v(-12.58, -16.56) * mm, "end": v(-12.62, -16.57) * mm});
            skLineSegment(sketch, "E829", {"start": v(-12.62, -16.57) * mm, "end": v(-12.66, -16.58) * mm});
            skLineSegment(sketch, "E830", {"start": v(-12.66, -16.58) * mm, "end": v(-12.7, -16.6) * mm});
            skLineSegment(sketch, "E831", {"start": v(-12.7, -16.6) * mm, "end": v(-12.75, -16.6) * mm});
            skLineSegment(sketch, "E832", {"start": v(-12.75, -16.6) * mm, "end": v(-12.8, -16.6) * mm});
            skLineSegment(sketch, "E833", {"start": v(-12.8, -16.6) * mm, "end": v(-12.84, -16.61) * mm});
            skLineSegment(sketch, "E834", {"start": v(-12.84, -16.61) * mm, "end": v(-12.88, -16.62) * mm});
            skLineSegment(sketch, "E835", {"start": v(-12.88, -16.62) * mm, "end": v(-12.92, -16.62) * mm});
            skLineSegment(sketch, "E836", {"start": v(-12.92, -16.62) * mm, "end": v(-12.97, -16.62) * mm});
            skLineSegment(sketch, "E837", {"start": v(-12.97, -16.62) * mm, "end": v(-13.01, -16.62) * mm});
            skLineSegment(sketch, "E838", {"start": v(-13.01, -16.62) * mm, "end": v(-13.05, -16.62) * mm});
            skLineSegment(sketch, "E839", {"start": v(-13.05, -16.62) * mm, "end": v(-13.1, -16.62) * mm});
            skLineSegment(sketch, "E840", {"start": v(-13.1, -16.62) * mm, "end": v(-13.14, -16.62) * mm});
            skLineSegment(sketch, "E841", {"start": v(-13.14, -16.62) * mm, "end": v(-13.19, -16.61) * mm});
            skLineSegment(sketch, "E842", {"start": v(-13.19, -16.61) * mm, "end": v(-13.23, -16.6) * mm});
            skLineSegment(sketch, "E843", {"start": v(-13.23, -16.6) * mm, "end": v(-13.27, -16.6) * mm});
            skLineSegment(sketch, "E844", {"start": v(-13.27, -16.6) * mm, "end": v(-13.32, -16.6) * mm});
            skLineSegment(sketch, "E845", {"start": v(-13.32, -16.6) * mm, "end": v(-13.36, -16.59) * mm});
            skLineSegment(sketch, "E846", {"start": v(-13.36, -16.59) * mm, "end": v(-13.4, -16.58) * mm});
            skLineSegment(sketch, "E847", {"start": v(-13.4, -16.58) * mm, "end": v(-13.44, -16.57) * mm});
            skLineSegment(sketch, "E848", {"start": v(-13.44, -16.57) * mm, "end": v(-13.63, -16.48) * mm});
            skLineSegment(sketch, "E849", {"start": v(-13.63, -16.48) * mm, "end": v(-13.67, -16.46) * mm});
            skLineSegment(sketch, "E850", {"start": v(-13.67, -16.46) * mm, "end": v(-13.7, -16.44) * mm});
            skLineSegment(sketch, "E851", {"start": v(-13.7, -16.44) * mm, "end": v(-13.72, -16.42) * mm});
            skLineSegment(sketch, "E852", {"start": v(-13.72, -16.42) * mm, "end": v(-13.74, -16.4) * mm});
            skLineSegment(sketch, "E853", {"start": v(-13.74, -16.4) * mm, "end": v(-13.74, -16.39) * mm});
            skLineSegment(sketch, "E854", {"start": v(-13.74, -16.39) * mm, "end": v(-13.75, -16.37) * mm});
            skLineSegment(sketch, "E855", {"start": v(-13.75, -16.37) * mm, "end": v(-13.76, -16.36) * mm});
            skLineSegment(sketch, "E856", {"start": v(-13.76, -16.36) * mm, "end": v(-13.76, -16.34) * mm});
            skLineSegment(sketch, "E857", {"start": v(-13.76, -16.34) * mm, "end": v(-13.77, -16.33) * mm});
            skLineSegment(sketch, "E858", {"start": v(-13.77, -16.33) * mm, "end": v(-13.77, -16.31) * mm});
            skLineSegment(sketch, "E859", {"start": v(-13.77, -16.31) * mm, "end": v(-13.78, -16.3) * mm});
            skLineSegment(sketch, "E860", {"start": v(-13.78, -16.3) * mm, "end": v(-13.8, -15.27) * mm});
            skFitSpline(sketch, "E861", {"points": [v(-16.09, 0.4) * mm, v(-16.48, 0.53) * mm, v(-16.87, 0.42) * mm], "startDerivative": vector(-0.77, 0.4) * mm, "endDerivative": vector(-0.8, -0.36) * mm});
            skFitSpline(sketch, "E862", {"points": [v(-9.68, -1.66) * mm, v(-8.41, -1.95) * mm, v(-8.04, -3.41) * mm], "startDerivative": vector(3.1, -0.07) * mm, "endDerivative": vector(0.22, -3.4) * mm});
            skLineSegment(sketch, "E863", {"start": v(-8.04, -3.41) * mm, "end": v(-8.04, -3.57) * mm});
            skLineSegment(sketch, "E864", {"start": v(-16.09, 0.4) * mm, "end": v(-15.75, 0.24) * mm});
            skLineSegment(sketch, "E865", {"start": v(-17.01, 0.36) * mm, "end": v(-16.87, 0.42) * mm});
            skLineSegment(sketch, "E866", {"start": v(-9.68, -1.66) * mm, "end": v(-9.7, 0.57) * mm});
            skLineSegment(sketch, "E867", {"start": v(-13.9, -1.75) * mm, "end": v(-16.26, -0.55) * mm});
            skFitSpline(sketch, "E868", {"points": [v(-16.26, -0.55) * mm, v(-16.5, -0.47) * mm, v(-16.83, -0.6) * mm], "startDerivative": vector(-0.52, 0.27) * mm, "endDerivative": vector(-0.63, -0.37) * mm});
            skFitSpline(sketch, "E869", {"points": [v(-9.4, -3.99) * mm, v(-9.18, -4.2) * mm, v(-9.85, -4.84) * mm], "startDerivative": vector(0.88, -0.52) * mm, "endDerivative": vector(-1.57, -1.12) * mm});
            skSolve(sketch);
        }
        {
            var Q0;
            Q0=qSketchRegion(id+"F27",true);
            extrude(context, id + "F28", {"entities" : qUnion([Q0]), "operationType" : NewBodyOperationType.ADD, "depth" : 26.5 * mm});
        }
        {
            var Q0;
            Q0=qSketchRegion(id+"F27",true);
            var Q1;
            {var subQ0=sQuery(id+"F0.wireOp",EDGE,"E7.rect.top");var subQ1=sQuery(id+"F0.wireOp",EDGE,"E7.rect.right");var subQ2=sQuery(id+"F0.wireOp",EDGE,"E7.rect.left");var subQ3=sQuery(id+"F0.wireOp",EDGE,"E7.rect.bottom");var subQ4=sQuery(id+"F0.wireOp",EDGE,"E5.MirrorC");var subQ5=sQuery(id+"F0.wireOp",EDGE,"E3");var subQ6=sQuery(id+"F0.wireOp",EDGE,"E2");var subQ7=sQuery(id+"F0.wireOp",EDGE,"E1");Q1=makeQuery(id+"F28.boolean.opBoolean","SPLIT",FACE,{"disambiguationData":[TD([makeQuery(id+"F28.opExtrude","SWEPT_FACE",FACE,{"disambiguationData":[OSD([sQuery(id+"F27.wireOp",EDGE,"E134")])]})])],"derivedFrom":makeQuery(id+"F6.opShell","OFFSET_FACE",FACE,{"disambiguationData":[OSD([subQ7,subQ6,subQ5,subQ4,subQ3,subQ0,subQ2,subQ1]),TDD([makeQuery(id+"F1.opExtrude","CAP_FACE",FACE,{"disambiguationData":[OSD([subQ7,subQ6,subQ5,subQ4,subQ3,subQ0,subQ2,subQ1])],"isStart":false})])]})});}
            extrude(context, id + "F29", {"entities" : qUnion([Q0]), "operationType" : NewBodyOperationType.REMOVE, "endBound" : BoundingType.UP_TO_SURFACE, "endBoundEntityFace" : qUnion([Q1]), "depth" : 23 * mm});
        }
        {
            var Q0;
            {var subQ0=sQuery(id+"F18.wireOp",EDGE,"E68");Q0=makeQuery(id+"F18.imprint","IMPRINT",FACE,{"disambiguationData":[TD([[makeQuery(id+"F18.imprint","IMPRINT",EDGE,{"derivedFrom":subQ0}),-1.0]])]});}
            extrude(context, id + "F30", {"entities" : qUnion([Q0]), "operationType" : NewBodyOperationType.REMOVE, "oppositeDirection" : true, "depth" : 2 * mm});
        }
        {
            var Q0;
            Q0=qCreatedBy(makeId("Top.planeOp"),FACE);
            var sketch = newSketch(context, id + "F31", { "sketchPlane" : qUnion([Q0])});
            skLineSegment(sketch, "E870.bottom", {"start": v(7.48, -5.58) * mm, "end": v(13.97, -5.58) * mm});
            skLineSegment(sketch, "E870.top", {"start": v(7.48, -5.2) * mm, "end": v(13.97, -5.2) * mm});
            skLineSegment(sketch, "E871.bottom", {"start": v(6.04, -5.58) * mm, "end": v(16.8, -5.58) * mm});
            skLineSegment(sketch, "E871.top", {"start": v(6.04, -5.2) * mm, "end": v(16.8, -5.2) * mm});
            skLineSegment(sketch, "E871.left", {"start": v(6.04, -5.58) * mm, "end": v(6.04, -5.2) * mm});
            skLineSegment(sketch, "E872", {"start": v(16.8, -5.2) * mm, "end": v(18.32, -5.2) * mm});
            skLineSegment(sketch, "E873", {"start": v(18.32, -5.2) * mm, "end": v(18.32, -5.58) * mm});
            skLineSegment(sketch, "E874", {"start": v(18.32, -5.58) * mm, "end": v(16.8, -5.58) * mm});
            skSolve(sketch);
        }
        {
            var Q0;
            Q0=qSketchRegion(id+"F31",true);
            var Q1;
            {var subQ1=sQuery(id+"F2.wireOp",EDGE,"E22");var subQ3=sQuery(id+"F2.wireOp",EDGE,"E20");Q1=makeQuery(id+"F24.boolean.opBoolean","SPLIT",FACE,{"disambiguationData":[TD([makeQuery(id+"F6.opShell","OFFSET_FACE",FACE,{"disambiguationData":[OSD([sQuery(id+"F0.wireOp",EDGE,"E3")])]})])],"derivedFrom":makeQuery(id+"F6.opShell","OFFSET_FACE",FACE,{"disambiguationData":[OSD([subQ3,subQ1])]})});}
            extrude(context, id + "F32", {"entities" : qUnion([Q0]), "operationType" : NewBodyOperationType.ADD, "endBound" : BoundingType.UP_TO_SURFACE, "endBoundEntityFace" : qUnion([Q1]), "depth" : 25 * mm});
        }
        {
            var Q0;
            {var subQ0=sQuery(id+"F0.wireOp",EDGE,"E7.rect.top");var subQ1=sQuery(id+"F0.wireOp",EDGE,"E7.rect.right");var subQ2=sQuery(id+"F0.wireOp",EDGE,"E7.rect.left");var subQ3=sQuery(id+"F0.wireOp",EDGE,"E7.rect.bottom");var subQ4=sQuery(id+"F0.wireOp",EDGE,"E5.MirrorC");var subQ5=sQuery(id+"F0.wireOp",EDGE,"E3");var subQ6=sQuery(id+"F0.wireOp",EDGE,"E2");var subQ7=sQuery(id+"F0.wireOp",EDGE,"E1");Q0=makeQuery(id+"F28.boolean.opBoolean","SPLIT",FACE,{"disambiguationData":[TD([makeQuery(id+"F4.opFillet","BLEND_FACE",FACE,{"disambiguationData":[OSD([subQ0])]})])],"derivedFrom":makeQuery(id+"F1.opExtrude","CAP_FACE",FACE,{"disambiguationData":[OSD([subQ7,subQ6,subQ5,subQ4,subQ3,subQ0,subQ2,subQ1])],"isStart":false})});}
            cPlane(context, id + "F33", {"entities" : qUnion([Q0]), "cplaneType" : CPlaneType.OFFSET, "offset" : 9 * mm, "oppositeDirection" : true, "width" : 150 * mm, "height" : 150 * mm});
        }
        {
            var Q0;
            Q0=qCreatedBy(id+"F33.planeOp",FACE);
            var sketch = newSketch(context, id + "F34", { "sketchPlane" : qUnion([Q0])});
            skCircle(sketch, "E875", {"center": v(-29.86, -30.9) * mm, "radius": 1.22 * mm});
            skCircle(sketch, "E876", {"center": v(-29.84, 14.65) * mm, "radius": 1.25 * mm});
            skSolve(sketch);
        }
        {
            var Q0;
            Q0=qSketchRegion(id+"F34",true);
            var Q1;
            Q1=makeQuery(id+"F3.boolean.opBoolean","COPY",FACE,{"derivedFrom":makeQuery(id+"F3.opExtrude","SWEPT_FACE",FACE,{"disambiguationData":[OSD([sQuery(id+"F2.wireOp",EDGE,"E14")])]})});
            extrude(context, id + "F35", {"entities" : qUnion([Q0]), "operationType" : NewBodyOperationType.ADD, "endBound" : BoundingType.UP_TO_SURFACE, "endBoundEntityFace" : qUnion([Q1]), "depth" : 25 * mm});
        }
        {
            var Q0;
            {var subQ0=sQuery(id+"F0.wireOp",EDGE,"E7.rect.right");var subQ1=sQuery(id+"F0.wireOp",EDGE,"E7.rect.left");var subQ2=sQuery(id+"F0.wireOp",EDGE,"E7.rect.top");var subQ3=sQuery(id+"F0.wireOp",EDGE,"E7.rect.bottom");var subQ4=sQuery(id+"F0.wireOp",EDGE,"E5.MirrorC");var subQ5=sQuery(id+"F0.wireOp",EDGE,"E3");var subQ6=sQuery(id+"F0.wireOp",EDGE,"E2");var subQ7=sQuery(id+"F0.wireOp",EDGE,"E1");Q0=makeQuery(id+"F28.boolean.opBoolean","SPLIT",FACE,{"disambiguationData":[TD([makeQuery(id+"F4.opFillet","BLEND_FACE",FACE,{"disambiguationData":[OSD([subQ3])]})])],"derivedFrom":makeQuery(id+"F1.opExtrude","CAP_FACE",FACE,{"disambiguationData":[OSD([subQ7,subQ6,subQ5,subQ4,subQ3,subQ2,subQ1,subQ0])],"isStart":false})});}
            cPlane(context, id + "F36", {"entities" : qUnion([Q0]), "cplaneType" : CPlaneType.OFFSET, "offset" : 17.5 * mm, "oppositeDirection" : true, "width" : 150 * mm, "height" : 150 * mm});
        }
        {
            var Q0;
            Q0=qCreatedBy(id+"F36.planeOp",FACE);
            var sketch = newSketch(context, id + "F37", { "sketchPlane" : qUnion([Q0])});
            skCircle(sketch, "E877", {"center": v(8.9, 3.98) * mm, "radius": 1.26 * mm});
            skCircle(sketch, "E878", {"center": v(15.8, -30.92) * mm, "radius": 1.17 * mm});
            skSolve(sketch);
        }
        {
            var Q0;
            Q0=qSketchRegion(id+"F37",true);
            var Q1;
            {var subQ0=sQuery(id+"F2.wireOp",EDGE,"E22");var subQ1=sQuery(id+"F2.wireOp",EDGE,"E20");Q1=makeQuery(id+"F24.boolean.opBoolean","SPLIT",FACE,{"disambiguationData":[TD([makeQuery(id+"F1.opExtrude","SWEPT_FACE",FACE,{"disambiguationData":[OSD([sQuery(id+"F0.wireOp",EDGE,"E3")])]})])],"derivedFrom":makeQuery(id+"F3.boolean.opBoolean","COPY",FACE,{"derivedFrom":makeQuery(id+"F3.opExtrude","SWEPT_FACE",FACE,{"disambiguationData":[OSD([subQ1,subQ0])]})})});}
            extrude(context, id + "F38", {"entities" : qUnion([Q0]), "operationType" : NewBodyOperationType.ADD, "endBound" : BoundingType.UP_TO_SURFACE, "endBoundEntityFace" : qUnion([Q1]), "depth" : 25 * mm});
        }
        {
            var Q0;
            Q0=makeQuery(id+"F1.opExtrude","SWEPT_FACE",FACE,{"disambiguationData":[OSD([sQuery(id+"F0.wireOp",EDGE,"E7.rect.bottom")])]});
            cPlane(context, id + "F39", {"entities" : qUnion([Q0]), "cplaneType" : CPlaneType.OFFSET, "offset" : 1.8 * mm, "oppositeDirection" : true, "width" : 150 * mm, "height" : 150 * mm});
        }
        {
            var Q0;
            Q0=qCreatedBy(id+"F39.planeOp",FACE);
            var sketch = newSketch(context, id + "F40", { "sketchPlane" : qUnion([Q0])});
            skLineSegment(sketch, "E879.top", {"start": v(-5.27, 0) * mm, "end": v(12.86, 0) * mm});
            skLineSegment(sketch, "E880.right", {"start": v(12.86, 5.48) * mm, "end": v(12.86, 0) * mm});
            skLineSegment(sketch, "E881.bottom", {"start": v(12.86, 0) * mm, "end": v(-5.27, 0) * mm});
            skLineSegment(sketch, "E881.top", {"start": v(12.86, 5.48) * mm, "end": v(-5.27, 5.48) * mm});
            skLineSegment(sketch, "E881.left", {"start": v(12.86, 0) * mm, "end": v(12.86, 5.48) * mm});
            skPoint(sketch, "E882.orphan", {"position": v(14.06, 0) * mm});
            skLineSegment(sketch, "E883", {"start": v(-5.27, 5.48) * mm, "end": v(-8, 5.48) * mm});
            skLineSegment(sketch, "E884", {"start": v(-8, 5.48) * mm, "end": v(-8, 0) * mm});
            skLineSegment(sketch, "E885", {"start": v(-8, 0) * mm, "end": v(-5.27, 0) * mm});
            skSolve(sketch);
        }
        {
            var Q0;
            Q0=qSketchRegion(id+"F40",true);
            extrude(context, id + "F41", {"entities" : qUnion([Q0]), "operationType" : NewBodyOperationType.REMOVE, "depth" : 1.2 * mm});
        }
        {
            var Q0;
            Q0=qCreatedBy(makeId("Top.planeOp"),FACE);
            var sketch = newSketch(context, id + "F42", { "sketchPlane" : qUnion([Q0])});
            skLineSegment(sketch, "E886.bottom", {"start": v(-10.2, -20.34) * mm, "end": v(-23.5, -20.34) * mm});
            skLineSegment(sketch, "E886.top", {"start": v(-9.76, -20.7) * mm, "end": v(-23.91, -20.7) * mm});
            skLineSegment(sketch, "E886.left", {"start": v(-9.76, -20.34) * mm, "end": v(-9.76, -20.7) * mm});
            skLineSegment(sketch, "E887", {"start": v(-9.76, -19.58) * mm, "end": v(-9.76, 2.28) * mm});
            skLineSegment(sketch, "E888.bottom", {"start": v(-10.2, 2.28) * mm, "end": v(-23.5, 2.28) * mm});
            skLineSegment(sketch, "E888.top", {"start": v(-9.76, 2.58) * mm, "end": v(-23.91, 2.58) * mm});
            skLineSegment(sketch, "E888.left", {"start": v(-9.76, 2.28) * mm, "end": v(-9.76, 2.58) * mm});
            skLineSegment(sketch, "E888.right", {"start": v(-23.91, 2.28) * mm, "end": v(-23.91, 2.58) * mm});
            skLineSegment(sketch, "E889.bottom", {"start": v(-10.2, -10.06) * mm, "end": v(-23.5, -10.06) * mm});
            skLineSegment(sketch, "E889.top", {"start": v(-10.2, -9.35) * mm, "end": v(-23.5, -9.35) * mm});
            skLineSegment(sketch, "E889.left", {"start": v(-9.76, -10.06) * mm, "end": v(-9.76, -9.35) * mm});
            skLineSegment(sketch, "E889.right", {"start": v(-25.9, -10.06) * mm, "end": v(-25.9, -9.35) * mm});
            skLineSegment(sketch, "E890", {"start": v(-10.2, -19.58) * mm, "end": v(-10.2, -10.06) * mm});
            skLineSegment(sketch, "E891.bottom", {"start": v(-23.91, 2.58) * mm, "end": v(-23.5, 2.58) * mm});
            skLineSegment(sketch, "E891.top", {"start": v(-23.91, -20.7) * mm, "end": v(-23.5, -20.7) * mm});
            skLineSegment(sketch, "E891.left", {"start": v(-23.91, 2.58) * mm, "end": v(-23.91, 2.28) * mm});
            skLineSegment(sketch, "E891.right", {"start": v(-23.5, 1.67) * mm, "end": v(-23.5, -9.35) * mm});
            skLineSegment(sketch, "E892.trimOffspring", {"start": v(-10.2, -9.35) * mm, "end": v(-10.2, 2.28) * mm});
            skLineSegment(sketch, "E893.trimOffspring", {"start": v(-23.91, -10.06) * mm, "end": v(-25.9, -10.06) * mm});
            skLineSegment(sketch, "E894.trimOffspring", {"start": v(-23.91, -10.06) * mm, "end": v(-23.91, -20.7) * mm});
            skLineSegment(sketch, "E895.trimOffspring", {"start": v(-23.5, -10.06) * mm, "end": v(-23.5, -20.34) * mm});
            skLineSegment(sketch, "E896.trimOffspring", {"start": v(-23.91, -9.35) * mm, "end": v(-25.9, -9.35) * mm});
            skLineSegment(sketch, "E897", {"start": v(-10.2, -19.58) * mm, "end": v(-9.76, -19.58) * mm});
            skLineSegment(sketch, "E898", {"start": v(-10.2, -20.34) * mm, "end": v(-9.76, -20.34) * mm});
            skLineSegment(sketch, "E899", {"start": v(-23.5, 2.28) * mm, "end": v(-23.91, 2.28) * mm});
            skLineSegment(sketch, "E900", {"start": v(-23.5, 1.67) * mm, "end": v(-23.91, 1.67) * mm});
            skLineSegment(sketch, "E901.trimOffspring", {"start": v(-23.91, 1.67) * mm, "end": v(-23.91, -9.35) * mm});
            skSolve(sketch);
        }
        {
            var Q0;
            Q0=qSketchRegion(id+"F42",true);
            var Q1;
            {var subQ0=sQuery(id+"F27.wireOp",EDGE,"E860");var subQ1=sQuery(id+"F27.wireOp",EDGE,"E859");var subQ2=sQuery(id+"F27.wireOp",EDGE,"E858");var subQ3=sQuery(id+"F27.wireOp",EDGE,"E857");var subQ4=sQuery(id+"F27.wireOp",EDGE,"E856");var subQ5=sQuery(id+"F27.wireOp",EDGE,"E855");var subQ6=sQuery(id+"F27.wireOp",EDGE,"E854");var subQ7=sQuery(id+"F27.wireOp",EDGE,"E853");var subQ8=sQuery(id+"F27.wireOp",EDGE,"E852");var subQ9=sQuery(id+"F27.wireOp",EDGE,"E851");var subQ10=sQuery(id+"F27.wireOp",EDGE,"E850");var subQ11=sQuery(id+"F27.wireOp",EDGE,"E849");var subQ12=sQuery(id+"F27.wireOp",EDGE,"E848");var subQ13=sQuery(id+"F27.wireOp",EDGE,"E847");var subQ14=sQuery(id+"F27.wireOp",EDGE,"E846");var subQ15=sQuery(id+"F27.wireOp",EDGE,"E845");var subQ16=sQuery(id+"F27.wireOp",EDGE,"E844");var subQ17=sQuery(id+"F27.wireOp",EDGE,"E843");var subQ18=sQuery(id+"F27.wireOp",EDGE,"E842");var subQ19=sQuery(id+"F27.wireOp",EDGE,"E841");var subQ20=sQuery(id+"F27.wireOp",EDGE,"E840");var subQ21=sQuery(id+"F27.wireOp",EDGE,"E839");var subQ22=sQuery(id+"F27.wireOp",EDGE,"E838");var subQ23=sQuery(id+"F27.wireOp",EDGE,"E837");var subQ24=sQuery(id+"F27.wireOp",EDGE,"E836");var subQ25=sQuery(id+"F27.wireOp",EDGE,"E835");var subQ26=sQuery(id+"F27.wireOp",EDGE,"E834");var subQ27=sQuery(id+"F27.wireOp",EDGE,"E833");var subQ28=sQuery(id+"F27.wireOp",EDGE,"E832");var subQ29=sQuery(id+"F27.wireOp",EDGE,"E831");var subQ30=sQuery(id+"F27.wireOp",EDGE,"E830");var subQ31=sQuery(id+"F27.wireOp",EDGE,"E829");var subQ32=sQuery(id+"F27.wireOp",EDGE,"E828");var subQ33=sQuery(id+"F27.wireOp",EDGE,"E827");var subQ34=sQuery(id+"F27.wireOp",EDGE,"E826");var subQ35=sQuery(id+"F27.wireOp",EDGE,"E825");var subQ36=sQuery(id+"F27.wireOp",EDGE,"E824");var subQ37=sQuery(id+"F27.wireOp",EDGE,"E823");var subQ38=sQuery(id+"F27.wireOp",EDGE,"E822");var subQ39=sQuery(id+"F27.wireOp",EDGE,"E821");var subQ40=sQuery(id+"F27.wireOp",EDGE,"E820");var subQ41=sQuery(id+"F27.wireOp",EDGE,"E819");var subQ42=sQuery(id+"F27.wireOp",EDGE,"E818");var subQ43=sQuery(id+"F27.wireOp",EDGE,"E817");var subQ44=sQuery(id+"F27.wireOp",EDGE,"E816");var subQ45=sQuery(id+"F27.wireOp",EDGE,"E815");var subQ46=sQuery(id+"F27.wireOp",EDGE,"E814");var subQ47=sQuery(id+"F27.wireOp",EDGE,"E813");var subQ48=sQuery(id+"F27.wireOp",EDGE,"E812");var subQ49=sQuery(id+"F27.wireOp",EDGE,"E811");var subQ50=sQuery(id+"F27.wireOp",EDGE,"E810");var subQ51=sQuery(id+"F27.wireOp",EDGE,"E809");var subQ52=sQuery(id+"F27.wireOp",EDGE,"E808");var subQ53=sQuery(id+"F27.wireOp",EDGE,"E807");var subQ54=sQuery(id+"F27.wireOp",EDGE,"E806");var subQ55=sQuery(id+"F27.wireOp",EDGE,"E805");var subQ56=sQuery(id+"F27.wireOp",EDGE,"E804");var subQ57=sQuery(id+"F27.wireOp",EDGE,"E803");var subQ58=sQuery(id+"F27.wireOp",EDGE,"E802");var subQ59=sQuery(id+"F27.wireOp",EDGE,"E801");var subQ60=sQuery(id+"F27.wireOp",EDGE,"E800");var subQ61=sQuery(id+"F27.wireOp",EDGE,"E799");var subQ62=sQuery(id+"F27.wireOp",EDGE,"E798");var subQ63=sQuery(id+"F27.wireOp",EDGE,"E797");var subQ64=sQuery(id+"F27.wireOp",EDGE,"E796");var subQ65=sQuery(id+"F27.wireOp",EDGE,"E795");var subQ66=sQuery(id+"F27.wireOp",EDGE,"E794");var subQ67=sQuery(id+"F27.wireOp",EDGE,"E793");var subQ68=sQuery(id+"F27.wireOp",EDGE,"E792");var subQ69=sQuery(id+"F27.wireOp",EDGE,"E791");var subQ70=sQuery(id+"F27.wireOp",EDGE,"E790");var subQ71=sQuery(id+"F27.wireOp",EDGE,"E789");var subQ72=sQuery(id+"F27.wireOp",EDGE,"E788");var subQ73=sQuery(id+"F27.wireOp",EDGE,"E787");var subQ74=sQuery(id+"F27.wireOp",EDGE,"E786");var subQ75=sQuery(id+"F27.wireOp",EDGE,"E785");var subQ76=sQuery(id+"F27.wireOp",EDGE,"E784");var subQ77=sQuery(id+"F27.wireOp",EDGE,"E783");var subQ78=sQuery(id+"F27.wireOp",EDGE,"E782");var subQ79=sQuery(id+"F27.wireOp",EDGE,"E781");var subQ80=sQuery(id+"F27.wireOp",EDGE,"E780");var subQ81=sQuery(id+"F27.wireOp",EDGE,"E779");var subQ82=sQuery(id+"F27.wireOp",EDGE,"E778");var subQ83=sQuery(id+"F27.wireOp",EDGE,"E777");var subQ84=sQuery(id+"F27.wireOp",EDGE,"E776");var subQ85=sQuery(id+"F27.wireOp",EDGE,"E775");var subQ86=sQuery(id+"F27.wireOp",EDGE,"E774");var subQ87=sQuery(id+"F27.wireOp",EDGE,"E773");var subQ88=sQuery(id+"F27.wireOp",EDGE,"E772");var subQ89=sQuery(id+"F27.wireOp",EDGE,"E771");var subQ90=sQuery(id+"F27.wireOp",EDGE,"E770");var subQ91=sQuery(id+"F27.wireOp",EDGE,"E769");var subQ92=sQuery(id+"F27.wireOp",EDGE,"E768");var subQ93=sQuery(id+"F27.wireOp",EDGE,"E767");var subQ94=sQuery(id+"F27.wireOp",EDGE,"E766");var subQ95=sQuery(id+"F27.wireOp",EDGE,"E765");var subQ96=sQuery(id+"F27.wireOp",EDGE,"E764");var subQ97=sQuery(id+"F27.wireOp",EDGE,"E763");var subQ98=sQuery(id+"F27.wireOp",EDGE,"E762");var subQ99=sQuery(id+"F27.wireOp",EDGE,"E761");var subQ100=sQuery(id+"F27.wireOp",EDGE,"E760");var subQ101=sQuery(id+"F27.wireOp",EDGE,"E759");var subQ102=sQuery(id+"F27.wireOp",EDGE,"E758");var subQ103=sQuery(id+"F27.wireOp",EDGE,"E757");var subQ104=sQuery(id+"F27.wireOp",EDGE,"E756");var subQ105=sQuery(id+"F27.wireOp",EDGE,"E755");var subQ106=sQuery(id+"F27.wireOp",EDGE,"E754");var subQ107=sQuery(id+"F27.wireOp",EDGE,"E753");var subQ108=sQuery(id+"F27.wireOp",EDGE,"E752");var subQ109=sQuery(id+"F27.wireOp",EDGE,"E751");var subQ110=sQuery(id+"F27.wireOp",EDGE,"E750");var subQ111=sQuery(id+"F27.wireOp",EDGE,"E749");var subQ112=sQuery(id+"F27.wireOp",EDGE,"E748");var subQ113=sQuery(id+"F27.wireOp",EDGE,"E747");var subQ114=sQuery(id+"F27.wireOp",EDGE,"E746");var subQ115=sQuery(id+"F27.wireOp",EDGE,"E745");var subQ116=sQuery(id+"F27.wireOp",EDGE,"E744");var subQ117=sQuery(id+"F27.wireOp",EDGE,"E743");var subQ118=sQuery(id+"F27.wireOp",EDGE,"E742");var subQ119=sQuery(id+"F27.wireOp",EDGE,"E741");var subQ120=sQuery(id+"F27.wireOp",EDGE,"E740");var subQ121=sQuery(id+"F27.wireOp",EDGE,"E739");var subQ122=sQuery(id+"F27.wireOp",EDGE,"E738");var subQ123=sQuery(id+"F27.wireOp",EDGE,"E737");var subQ124=sQuery(id+"F27.wireOp",EDGE,"E736");var subQ125=sQuery(id+"F27.wireOp",EDGE,"E735");var subQ126=sQuery(id+"F27.wireOp",EDGE,"E734");var subQ127=sQuery(id+"F27.wireOp",EDGE,"E733");var subQ128=sQuery(id+"F27.wireOp",EDGE,"E732");var subQ129=sQuery(id+"F27.wireOp",EDGE,"E731");var subQ130=sQuery(id+"F27.wireOp",EDGE,"E730");var subQ131=sQuery(id+"F27.wireOp",EDGE,"E729");var subQ132=sQuery(id+"F27.wireOp",EDGE,"E728");var subQ133=sQuery(id+"F27.wireOp",EDGE,"E727");var subQ134=sQuery(id+"F27.wireOp",EDGE,"E726");var subQ135=sQuery(id+"F27.wireOp",EDGE,"E725");var subQ136=sQuery(id+"F27.wireOp",EDGE,"E724");var subQ137=sQuery(id+"F27.wireOp",EDGE,"E723");var subQ138=sQuery(id+"F27.wireOp",EDGE,"E722");var subQ139=sQuery(id+"F27.wireOp",EDGE,"E721");var subQ140=sQuery(id+"F27.wireOp",EDGE,"E720");var subQ141=sQuery(id+"F27.wireOp",EDGE,"E719");var subQ142=sQuery(id+"F27.wireOp",EDGE,"E718");var subQ143=sQuery(id+"F27.wireOp",EDGE,"E717");var subQ144=sQuery(id+"F27.wireOp",EDGE,"E716");var subQ145=sQuery(id+"F27.wireOp",EDGE,"E715");var subQ146=sQuery(id+"F27.wireOp",EDGE,"E714");var subQ147=sQuery(id+"F27.wireOp",EDGE,"E713");var subQ148=sQuery(id+"F27.wireOp",EDGE,"E712");var subQ149=sQuery(id+"F27.wireOp",EDGE,"E711");var subQ150=sQuery(id+"F27.wireOp",EDGE,"E710");var subQ151=sQuery(id+"F27.wireOp",EDGE,"E709");var subQ152=sQuery(id+"F27.wireOp",EDGE,"E708");var subQ153=sQuery(id+"F27.wireOp",EDGE,"E707");var subQ154=sQuery(id+"F27.wireOp",EDGE,"E706");var subQ155=sQuery(id+"F27.wireOp",EDGE,"E705");var subQ156=sQuery(id+"F27.wireOp",EDGE,"E704");var subQ157=sQuery(id+"F27.wireOp",EDGE,"E703");var subQ158=sQuery(id+"F27.wireOp",EDGE,"E702");var subQ159=sQuery(id+"F27.wireOp",EDGE,"E701");var subQ160=sQuery(id+"F27.wireOp",EDGE,"E700");var subQ161=sQuery(id+"F27.wireOp",EDGE,"E699");var subQ162=sQuery(id+"F27.wireOp",EDGE,"E698");var subQ163=sQuery(id+"F27.wireOp",EDGE,"E697");var subQ164=sQuery(id+"F27.wireOp",EDGE,"E696");var subQ165=sQuery(id+"F27.wireOp",EDGE,"E695");var subQ166=sQuery(id+"F27.wireOp",EDGE,"E694");var subQ167=sQuery(id+"F27.wireOp",EDGE,"E693");var subQ168=sQuery(id+"F27.wireOp",EDGE,"E692");var subQ169=sQuery(id+"F27.wireOp",EDGE,"E691");var subQ170=sQuery(id+"F27.wireOp",EDGE,"E690");var subQ171=sQuery(id+"F27.wireOp",EDGE,"E689");var subQ172=sQuery(id+"F27.wireOp",EDGE,"E688");var subQ173=sQuery(id+"F27.wireOp",EDGE,"E687");var subQ174=sQuery(id+"F27.wireOp",EDGE,"E686");var subQ175=sQuery(id+"F27.wireOp",EDGE,"E685");var subQ176=sQuery(id+"F27.wireOp",EDGE,"E684");var subQ177=sQuery(id+"F27.wireOp",EDGE,"E683");var subQ178=sQuery(id+"F27.wireOp",EDGE,"E682");var subQ179=sQuery(id+"F27.wireOp",EDGE,"E681");var subQ180=sQuery(id+"F27.wireOp",EDGE,"E680");var subQ181=sQuery(id+"F27.wireOp",EDGE,"E679");var subQ182=sQuery(id+"F27.wireOp",EDGE,"E678");var subQ183=sQuery(id+"F27.wireOp",EDGE,"E677");var subQ184=sQuery(id+"F27.wireOp",EDGE,"E676");var subQ185=sQuery(id+"F27.wireOp",EDGE,"E675");var subQ186=sQuery(id+"F27.wireOp",EDGE,"E674");var subQ187=sQuery(id+"F27.wireOp",EDGE,"E673");var subQ188=sQuery(id+"F27.wireOp",EDGE,"E672");var subQ189=sQuery(id+"F27.wireOp",EDGE,"E671");var subQ190=sQuery(id+"F27.wireOp",EDGE,"E670");var subQ191=sQuery(id+"F27.wireOp",EDGE,"E669");var subQ192=sQuery(id+"F27.wireOp",EDGE,"E668");var subQ193=sQuery(id+"F27.wireOp",EDGE,"E667");var subQ194=sQuery(id+"F27.wireOp",EDGE,"E666");var subQ195=sQuery(id+"F27.wireOp",EDGE,"E869");var subQ196=sQuery(id+"F27.wireOp",EDGE,"E868");var subQ197=sQuery(id+"F27.wireOp",EDGE,"E867");var subQ198=sQuery(id+"F27.wireOp",EDGE,"E865");var subQ199=sQuery(id+"F27.wireOp",EDGE,"E864");var subQ200=sQuery(id+"F27.wireOp",EDGE,"E861");var subQ201=sQuery(id+"F27.wireOp",EDGE,"E336");var subQ202=sQuery(id+"F27.wireOp",EDGE,"E335");var subQ203=sQuery(id+"F27.wireOp",EDGE,"E334");var subQ204=sQuery(id+"F27.wireOp",EDGE,"E332");var subQ205=sQuery(id+"F27.wireOp",EDGE,"E331");var subQ206=sQuery(id+"F27.wireOp",EDGE,"E330");var subQ207=sQuery(id+"F27.wireOp",EDGE,"E329");var subQ208=sQuery(id+"F27.wireOp",EDGE,"E328");var subQ209=sQuery(id+"F27.wireOp",EDGE,"E327");var subQ210=sQuery(id+"F27.wireOp",EDGE,"E326");var subQ211=sQuery(id+"F27.wireOp",EDGE,"E325");var subQ212=sQuery(id+"F27.wireOp",EDGE,"E324");var subQ213=sQuery(id+"F27.wireOp",EDGE,"E323");var subQ214=sQuery(id+"F27.wireOp",EDGE,"E322");var subQ215=sQuery(id+"F27.wireOp",EDGE,"E321");var subQ216=sQuery(id+"F27.wireOp",EDGE,"E320");var subQ217=sQuery(id+"F27.wireOp",EDGE,"E319");var subQ218=sQuery(id+"F27.wireOp",EDGE,"E318");var subQ219=sQuery(id+"F27.wireOp",EDGE,"E317");var subQ220=sQuery(id+"F27.wireOp",EDGE,"E316");var subQ221=sQuery(id+"F27.wireOp",EDGE,"E315");var subQ222=sQuery(id+"F27.wireOp",EDGE,"E314");var subQ223=sQuery(id+"F27.wireOp",EDGE,"E313");var subQ224=sQuery(id+"F27.wireOp",EDGE,"E312");var subQ225=sQuery(id+"F27.wireOp",EDGE,"E311");var subQ226=sQuery(id+"F27.wireOp",EDGE,"E310");var subQ227=sQuery(id+"F27.wireOp",EDGE,"E309");var subQ228=sQuery(id+"F27.wireOp",EDGE,"E308");var subQ229=sQuery(id+"F27.wireOp",EDGE,"E307");var subQ230=sQuery(id+"F27.wireOp",EDGE,"E306");var subQ231=sQuery(id+"F27.wireOp",EDGE,"E305");var subQ232=sQuery(id+"F27.wireOp",EDGE,"E304");var subQ233=sQuery(id+"F27.wireOp",EDGE,"E303");var subQ234=sQuery(id+"F27.wireOp",EDGE,"E302");var subQ235=sQuery(id+"F27.wireOp",EDGE,"E301");var subQ236=sQuery(id+"F27.wireOp",EDGE,"E300");var subQ237=sQuery(id+"F27.wireOp",EDGE,"E299");var subQ238=sQuery(id+"F27.wireOp",EDGE,"E298");var subQ239=sQuery(id+"F27.wireOp",EDGE,"E297");var subQ240=sQuery(id+"F27.wireOp",EDGE,"E296");var subQ241=sQuery(id+"F27.wireOp",EDGE,"E295");var subQ242=sQuery(id+"F27.wireOp",EDGE,"E294");var subQ243=sQuery(id+"F27.wireOp",EDGE,"E293");var subQ244=sQuery(id+"F27.wireOp",EDGE,"E292");var subQ245=sQuery(id+"F27.wireOp",EDGE,"E291");var subQ246=sQuery(id+"F27.wireOp",EDGE,"E290");var subQ247=sQuery(id+"F27.wireOp",EDGE,"E289");var subQ248=sQuery(id+"F27.wireOp",EDGE,"E288");var subQ249=sQuery(id+"F27.wireOp",EDGE,"E287");var subQ250=sQuery(id+"F27.wireOp",EDGE,"E286");var subQ251=sQuery(id+"F27.wireOp",EDGE,"E285");var subQ252=sQuery(id+"F27.wireOp",EDGE,"E284");var subQ253=sQuery(id+"F27.wireOp",EDGE,"E283");var subQ254=sQuery(id+"F27.wireOp",EDGE,"E282");var subQ255=sQuery(id+"F27.wireOp",EDGE,"E281");var subQ256=sQuery(id+"F27.wireOp",EDGE,"E280");var subQ257=sQuery(id+"F27.wireOp",EDGE,"E279");var subQ258=sQuery(id+"F27.wireOp",EDGE,"E278");var subQ259=sQuery(id+"F27.wireOp",EDGE,"E277");var subQ260=sQuery(id+"F27.wireOp",EDGE,"E276");var subQ261=sQuery(id+"F27.wireOp",EDGE,"E275");var subQ262=sQuery(id+"F27.wireOp",EDGE,"E274");var subQ263=sQuery(id+"F27.wireOp",EDGE,"E273");var subQ264=sQuery(id+"F27.wireOp",EDGE,"E272");var subQ265=sQuery(id+"F27.wireOp",EDGE,"E271");var subQ266=sQuery(id+"F27.wireOp",EDGE,"E270");var subQ267=sQuery(id+"F27.wireOp",EDGE,"E269");var subQ268=sQuery(id+"F27.wireOp",EDGE,"E268");var subQ269=sQuery(id+"F27.wireOp",EDGE,"E267");var subQ270=sQuery(id+"F27.wireOp",EDGE,"E266");var subQ271=sQuery(id+"F27.wireOp",EDGE,"E265");var subQ272=sQuery(id+"F27.wireOp",EDGE,"E264");var subQ273=sQuery(id+"F27.wireOp",EDGE,"E263");var subQ274=sQuery(id+"F27.wireOp",EDGE,"E262");var subQ275=sQuery(id+"F27.wireOp",EDGE,"E261");var subQ276=sQuery(id+"F27.wireOp",EDGE,"E260");var subQ277=sQuery(id+"F27.wireOp",EDGE,"E259");var subQ278=sQuery(id+"F27.wireOp",EDGE,"E258");var subQ279=sQuery(id+"F27.wireOp",EDGE,"E257");var subQ280=sQuery(id+"F27.wireOp",EDGE,"E256");var subQ281=sQuery(id+"F27.wireOp",EDGE,"E255");var subQ282=sQuery(id+"F27.wireOp",EDGE,"E254");var subQ283=sQuery(id+"F27.wireOp",EDGE,"E253");var subQ284=sQuery(id+"F27.wireOp",EDGE,"E252");var subQ285=sQuery(id+"F27.wireOp",EDGE,"E193");var subQ286=sQuery(id+"F27.wireOp",EDGE,"E192");var subQ287=sQuery(id+"F27.wireOp",EDGE,"E191");var subQ288=sQuery(id+"F27.wireOp",EDGE,"E190");var subQ289=sQuery(id+"F27.wireOp",EDGE,"E189");var subQ290=sQuery(id+"F27.wireOp",EDGE,"E188");var subQ291=sQuery(id+"F27.wireOp",EDGE,"E187");var subQ292=sQuery(id+"F27.wireOp",EDGE,"E186");var subQ293=sQuery(id+"F27.wireOp",EDGE,"E185");var subQ294=sQuery(id+"F27.wireOp",EDGE,"E184");var subQ295=sQuery(id+"F27.wireOp",EDGE,"E183");var subQ296=sQuery(id+"F27.wireOp",EDGE,"E182");var subQ297=sQuery(id+"F27.wireOp",EDGE,"E181");var subQ298=sQuery(id+"F27.wireOp",EDGE,"E134");var subQ299=sQuery(id+"F0.wireOp",EDGE,"E7.rect.bottom");var subQ302=sQuery(id+"F0.wireOp",EDGE,"E7.rect.right");var subQ303=sQuery(id+"F0.wireOp",EDGE,"E7.rect.left");var subQ304=sQuery(id+"F0.wireOp",EDGE,"E7.rect.top");var subQ305=sQuery(id+"F0.wireOp",EDGE,"E5.MirrorC");var subQ306=sQuery(id+"F0.wireOp",EDGE,"E3");var subQ307=sQuery(id+"F0.wireOp",EDGE,"E2");var subQ308=sQuery(id+"F0.wireOp",EDGE,"E1");var subQ309=makeQuery(id+"F1.opExtrude","CAP_FACE",FACE,{"disambiguationData":[OSD([subQ308,subQ307,subQ306,subQ305,subQ299,subQ304,subQ303,subQ302])],"isStart":false});var subQ312=makeQuery(id+"F6.opShell","OFFSET_FACE",FACE,{"disambiguationData":[OSD([subQ308,subQ307,subQ306,subQ305,subQ299,subQ304,subQ303,subQ302]),TDD([subQ309])]});Q1=makeQuery(id+"F29.boolean.opBoolean","MERGE",FACE,{"derivedFrom":[makeQuery(id+"F28.boolean.opBoolean","SPLIT",FACE,{"disambiguationData":[TD([makeQuery(id+"F28.opExtrude","SWEPT_FACE",FACE,{"disambiguationData":[OSD([subQ298])]})])],"derivedFrom":subQ312}),makeQuery(id+"F28.boolean.opBoolean","SPLIT",FACE,{"disambiguationData":[TD([makeQuery(id+"F28.opExtrude","SWEPT_FACE",FACE,{"disambiguationData":[OSD([subQ262])]})])],"derivedFrom":subQ312}),makeQuery(id+"F28.boolean.opBoolean","SPLIT",FACE,{"disambiguationData":[TD([makeQuery(id+"F28.opExtrude","SWEPT_FACE",FACE,{"disambiguationData":[OSD([subQ297])]})])],"derivedFrom":subQ312}),makeQuery(id+"F29.opExtrude","CAP_FACE",FACE,{"disambiguationData":[OSD([subQ298,sQuery(id+"F27.wireOp",EDGE,"E135"),sQuery(id+"F27.wireOp",EDGE,"E136"),sQuery(id+"F27.wireOp",EDGE,"E137"),sQuery(id+"F27.wireOp",EDGE,"E138"),sQuery(id+"F27.wireOp",EDGE,"E139"),sQuery(id+"F27.wireOp",EDGE,"E140"),sQuery(id+"F27.wireOp",EDGE,"E141"),sQuery(id+"F27.wireOp",EDGE,"E142"),sQuery(id+"F27.wireOp",EDGE,"E143"),sQuery(id+"F27.wireOp",EDGE,"E144"),sQuery(id+"F27.wireOp",EDGE,"E145"),sQuery(id+"F27.wireOp",EDGE,"E146"),sQuery(id+"F27.wireOp",EDGE,"E147"),sQuery(id+"F27.wireOp",EDGE,"E148"),sQuery(id+"F27.wireOp",EDGE,"E149"),sQuery(id+"F27.wireOp",EDGE,"E150"),sQuery(id+"F27.wireOp",EDGE,"E151"),sQuery(id+"F27.wireOp",EDGE,"E152"),sQuery(id+"F27.wireOp",EDGE,"E153"),sQuery(id+"F27.wireOp",EDGE,"E154"),sQuery(id+"F27.wireOp",EDGE,"E155"),sQuery(id+"F27.wireOp",EDGE,"E156"),sQuery(id+"F27.wireOp",EDGE,"E157"),sQuery(id+"F27.wireOp",EDGE,"E158"),sQuery(id+"F27.wireOp",EDGE,"E159"),sQuery(id+"F27.wireOp",EDGE,"E160"),sQuery(id+"F27.wireOp",EDGE,"E161"),sQuery(id+"F27.wireOp",EDGE,"E162"),sQuery(id+"F27.wireOp",EDGE,"E163"),sQuery(id+"F27.wireOp",EDGE,"E164"),sQuery(id+"F27.wireOp",EDGE,"E165"),sQuery(id+"F27.wireOp",EDGE,"E166"),sQuery(id+"F27.wireOp",EDGE,"E167"),sQuery(id+"F27.wireOp",EDGE,"E168"),sQuery(id+"F27.wireOp",EDGE,"E169"),sQuery(id+"F27.wireOp",EDGE,"E170"),sQuery(id+"F27.wireOp",EDGE,"E171"),sQuery(id+"F27.wireOp",EDGE,"E172"),sQuery(id+"F27.wireOp",EDGE,"E173"),sQuery(id+"F27.wireOp",EDGE,"E174"),sQuery(id+"F27.wireOp",EDGE,"E175"),sQuery(id+"F27.wireOp",EDGE,"E176"),sQuery(id+"F27.wireOp",EDGE,"E177"),sQuery(id+"F27.wireOp",EDGE,"E178"),sQuery(id+"F27.wireOp",EDGE,"E179"),sQuery(id+"F27.wireOp",EDGE,"E180"),subQ297,subQ296,subQ295,subQ294,subQ293,subQ292,subQ291,subQ290,subQ289,subQ288,subQ287,subQ286,subQ285,sQuery(id+"F27.wireOp",EDGE,"E194"),sQuery(id+"F27.wireOp",EDGE,"E195"),sQuery(id+"F27.wireOp",EDGE,"E196"),sQuery(id+"F27.wireOp",EDGE,"E197"),sQuery(id+"F27.wireOp",EDGE,"E198"),sQuery(id+"F27.wireOp",EDGE,"E199"),sQuery(id+"F27.wireOp",EDGE,"E200"),sQuery(id+"F27.wireOp",EDGE,"E201"),sQuery(id+"F27.wireOp",EDGE,"E202"),sQuery(id+"F27.wireOp",EDGE,"E203"),sQuery(id+"F27.wireOp",EDGE,"E204"),sQuery(id+"F27.wireOp",EDGE,"E205"),sQuery(id+"F27.wireOp",EDGE,"E206"),sQuery(id+"F27.wireOp",EDGE,"E207"),sQuery(id+"F27.wireOp",EDGE,"E208"),sQuery(id+"F27.wireOp",EDGE,"E209"),sQuery(id+"F27.wireOp",EDGE,"E210"),sQuery(id+"F27.wireOp",EDGE,"E211"),sQuery(id+"F27.wireOp",EDGE,"E212"),sQuery(id+"F27.wireOp",EDGE,"E213"),sQuery(id+"F27.wireOp",EDGE,"E214"),sQuery(id+"F27.wireOp",EDGE,"E215"),sQuery(id+"F27.wireOp",EDGE,"E216"),sQuery(id+"F27.wireOp",EDGE,"E217"),sQuery(id+"F27.wireOp",EDGE,"E218"),sQuery(id+"F27.wireOp",EDGE,"E219"),sQuery(id+"F27.wireOp",EDGE,"E220"),sQuery(id+"F27.wireOp",EDGE,"E221"),sQuery(id+"F27.wireOp",EDGE,"E222"),sQuery(id+"F27.wireOp",EDGE,"E223"),sQuery(id+"F27.wireOp",EDGE,"E224"),sQuery(id+"F27.wireOp",EDGE,"E225"),sQuery(id+"F27.wireOp",EDGE,"E226"),sQuery(id+"F27.wireOp",EDGE,"E227"),sQuery(id+"F27.wireOp",EDGE,"E228"),sQuery(id+"F27.wireOp",EDGE,"E229"),sQuery(id+"F27.wireOp",EDGE,"E230"),sQuery(id+"F27.wireOp",EDGE,"E231"),sQuery(id+"F27.wireOp",EDGE,"E232"),sQuery(id+"F27.wireOp",EDGE,"E233"),sQuery(id+"F27.wireOp",EDGE,"E234"),sQuery(id+"F27.wireOp",EDGE,"E235"),sQuery(id+"F27.wireOp",EDGE,"E236"),sQuery(id+"F27.wireOp",EDGE,"E237"),sQuery(id+"F27.wireOp",EDGE,"E238"),sQuery(id+"F27.wireOp",EDGE,"E239"),sQuery(id+"F27.wireOp",EDGE,"E240"),sQuery(id+"F27.wireOp",EDGE,"E241"),sQuery(id+"F27.wireOp",EDGE,"E242"),sQuery(id+"F27.wireOp",EDGE,"E243"),sQuery(id+"F27.wireOp",EDGE,"E244"),sQuery(id+"F27.wireOp",EDGE,"E245"),sQuery(id+"F27.wireOp",EDGE,"E246"),sQuery(id+"F27.wireOp",EDGE,"E247"),sQuery(id+"F27.wireOp",EDGE,"E248"),sQuery(id+"F27.wireOp",EDGE,"E249"),sQuery(id+"F27.wireOp",EDGE,"E250"),sQuery(id+"F27.wireOp",EDGE,"E251"),subQ284,subQ283,subQ282,subQ281,subQ280,subQ279,subQ278,subQ277,subQ276,subQ275,subQ274,subQ273,subQ272,subQ271,subQ270,subQ269,subQ268,subQ267,subQ266,subQ265,subQ264,subQ263,subQ262,subQ261,subQ260,subQ259,subQ258,subQ257,subQ256,subQ255,subQ254,subQ253,subQ252,subQ251,subQ250,subQ249,subQ248,subQ247,subQ246,subQ245,subQ244,subQ243,subQ242,subQ241,subQ240,subQ239,subQ238,subQ237,subQ236,subQ235,subQ234,subQ233,subQ232,subQ231,subQ230,subQ229,subQ228,subQ227,subQ226,subQ225,subQ224,subQ223,subQ222,subQ221,subQ220,subQ219,subQ218,subQ217,subQ216,subQ215,subQ214,subQ213,subQ212,subQ211,subQ210,subQ209,subQ208,subQ207,subQ206,subQ205,subQ204,sQuery(id+"F27.wireOp",EDGE,"E333"),subQ203,subQ202,subQ201,subQ200,sQuery(id+"F27.wireOp",EDGE,"E862"),sQuery(id+"F27.wireOp",EDGE,"E863"),subQ199,subQ198,sQuery(id+"F27.wireOp",EDGE,"E866"),subQ197,subQ196,subQ195])],"isStart":false}),makeQuery(id+"F29.opExtrude","CAP_FACE",FACE,{"disambiguationData":[OSD([subQ194,subQ193,subQ192,subQ191,subQ190,subQ189,subQ188,subQ187,subQ186,subQ185,subQ184,subQ183,subQ182,subQ181,subQ180,subQ179,subQ178,subQ177,subQ176,subQ175,subQ174,subQ173,subQ172,subQ171,subQ170,subQ169,subQ168,subQ167,subQ166,subQ165,subQ164,subQ163,subQ162,subQ161,subQ160,subQ159,subQ158,subQ157,subQ156,subQ155,subQ154,subQ153,subQ152,subQ151,subQ150,subQ149])],"isStart":false}),makeQuery(id+"F29.opExtrude","CAP_FACE",FACE,{"disambiguationData":[OSD([subQ148,subQ147,subQ146,subQ145,subQ144,subQ143,subQ142,subQ141,subQ140,subQ139,subQ138,subQ137,subQ136,subQ135,subQ134,subQ133,subQ132,subQ131,subQ130,subQ129,subQ128,subQ127,subQ126,subQ125,subQ124,subQ123,subQ122,subQ121,subQ120,subQ119,subQ118,subQ117,subQ116,subQ115,subQ114,subQ113,subQ112,subQ111,subQ110,subQ109,subQ108,subQ107,subQ106,subQ105,subQ104,subQ103,subQ102,subQ101,subQ100])],"isStart":false}),makeQuery(id+"F29.opExtrude","CAP_FACE",FACE,{"disambiguationData":[OSD([subQ99,subQ98,subQ97,subQ96,subQ95,subQ94,subQ93,subQ92,subQ91,subQ90,subQ89,subQ88,subQ87,subQ86,subQ85,subQ84,subQ83,subQ82,subQ81,subQ80,subQ79,subQ78,subQ77,subQ76,subQ75,subQ74,subQ73,subQ72,subQ71,subQ70,subQ69,subQ68,subQ67,subQ66,subQ65,subQ64,subQ63,subQ62,subQ61,subQ60,subQ59,subQ58,subQ57,subQ56,subQ55,subQ54,subQ53,subQ52,subQ51,subQ50,subQ49,subQ48,subQ47,subQ46,subQ45,subQ44])],"isStart":false}),makeQuery(id+"F29.opExtrude","CAP_FACE",FACE,{"disambiguationData":[OSD([subQ43,subQ42,subQ41,subQ40,subQ39,subQ38,subQ37,subQ36,subQ35,subQ34,subQ33,subQ32,subQ31,subQ30,subQ29,subQ28,subQ27,subQ26,subQ25,subQ24,subQ23,subQ22,subQ21,subQ20,subQ19,subQ18,subQ17,subQ16,subQ15,subQ14,subQ13,subQ12,subQ11,subQ10,subQ9,subQ8,subQ7,subQ6,subQ5,subQ4,subQ3,subQ2,subQ1,subQ0])],"isStart":false})]});}
            extrude(context, id + "F43", {"entities" : qUnion([Q0]), "operationType" : NewBodyOperationType.ADD, "endBound" : BoundingType.UP_TO_SURFACE, "endBoundEntityFace" : qUnion([Q1]), "depth" : 25 * mm});
        }
        {
            var Q0;
            {var subQ0=sQuery(id+"F0.wireOp",EDGE,"E7.rect.right");var subQ2=sQuery(id+"F0.wireOp",EDGE,"E7.rect.bottom");var subQ3=makeQuery(id+"F1.opExtrude","SWEPT_FACE",FACE,{"disambiguationData":[OSD([subQ2])]});var subQ8=sQuery(id+"F0.wireOp",EDGE,"E7.rect.left");var subQ17=sQuery(id+"F0.wireOp",EDGE,"E7.rect.top");var subQ19=sQuery(id+"F0.wireOp",EDGE,"E5.MirrorC");var subQ20=sQuery(id+"F0.wireOp",EDGE,"E3");var subQ21=sQuery(id+"F0.wireOp",EDGE,"E2");var subQ22=sQuery(id+"F0.wireOp",EDGE,"E1");var subQ23=makeQuery(id+"F1.opExtrude","CAP_FACE",FACE,{"disambiguationData":[OSD([subQ22,subQ21,subQ20,subQ19,subQ2,subQ17,subQ8,subQ0])],"isStart":true});Q0=makeQuery(id+"F26.boolean.opBoolean","MERGE",FACE,{"derivedFrom":[makeQuery(id+"F6.opShell","OFFSET_FACE",FACE,{"disambiguationData":[OSD([subQ22,subQ21,subQ20,subQ19,subQ2,subQ17,subQ8,subQ0]),TDD([subQ23]),OD(2.0)]}),makeQuery(id+"F14.boolean.opBoolean","SPLIT",FACE,{"disambiguationData":[TD([makeQuery(id+"F1.opExtrude","SWEPT_FACE",FACE,{"disambiguationData":[OSD([subQ22])]})])],"derivedFrom":makeQuery(id+"F6.opShell","OFFSET_FACE",FACE,{"disambiguationData":[OSD([subQ22,subQ21,subQ20,subQ19,subQ2,subQ17,subQ8,subQ0]),TDD([subQ23]),OD(0.0)]})}),makeQuery(id+"F14.boolean.opBoolean","SPLIT",FACE,{"disambiguationData":[TD([subQ3])],"derivedFrom":makeQuery(id+"F10.boolean.opBoolean","SPLIT",FACE,{"disambiguationData":[TD([subQ3])],"derivedFrom":makeQuery(id+"F6.opShell","OFFSET_FACE",FACE,{"disambiguationData":[OSD([subQ22,subQ21,subQ20,subQ19,subQ2,subQ17,subQ8,subQ0]),TDD([subQ23]),OD(3.0)]})})}),makeQuery(id+"F26.opExtrude","CAP_FACE",FACE,{"disambiguationData":[OSD([sQuery(id+"F25.wireOp",EDGE,"E113.top"),sQuery(id+"F25.wireOp",EDGE,"E113.left"),sQuery(id+"F25.wireOp",EDGE,"E113.right"),sQuery(id+"F25.wireOp",EDGE,"E114.bottom"),sQuery(id+"F25.wireOp",EDGE,"E114.top"),sQuery(id+"F25.wireOp",EDGE,"E114.right"),sQuery(id+"F25.wireOp",EDGE,"E113.bottom"),sQuery(id+"F25.wireOp",EDGE,"E118.top"),sQuery(id+"F25.wireOp",EDGE,"E118.left"),sQuery(id+"F25.wireOp",EDGE,"E118.right")])],"isStart":true}),makeQuery(id+"F26.opExtrude","CAP_FACE",FACE,{"disambiguationData":[OSD([sQuery(id+"F25.wireOp",EDGE,"E116.bottom"),sQuery(id+"F25.wireOp",EDGE,"E116.top"),sQuery(id+"F25.wireOp",EDGE,"E116.left"),sQuery(id+"F25.wireOp",EDGE,"E116.right"),sQuery(id+"F25.wireOp",EDGE,"E117.bottom"),sQuery(id+"F25.wireOp",EDGE,"E117.top"),sQuery(id+"F25.wireOp",EDGE,"E117.right")])],"isStart":true})]});}
            cPlane(context, id + "F44", {"entities" : qUnion([Q0]), "cplaneType" : CPlaneType.OFFSET, "offset" : 0.6 * mm, "oppositeDirection" : true, "width" : 150 * mm, "height" : 150 * mm});
        }
        {
            var Q0;
            Q0=qCreatedBy(id+"F44.planeOp",FACE);
            var sketch = newSketch(context, id + "F45", { "sketchPlane" : qUnion([Q0])});
            skLineSegment(sketch, "E902.bottom", {"start": v(-24.07, 22.32) * mm, "end": v(-9.14, 22.32) * mm});
            skLineSegment(sketch, "E902.top", {"start": v(-24.07, -4.65) * mm, "end": v(-9.14, -4.65) * mm});
            skLineSegment(sketch, "E902.left", {"start": v(-24.07, 22.32) * mm, "end": v(-24.07, -4.65) * mm});
            skLineSegment(sketch, "E902.right", {"start": v(-9.14, 22.32) * mm, "end": v(-9.14, -4.65) * mm});
            skSolve(sketch);
        }
        {
            var Q0;
            Q0=qSketchRegion(id+"F45",true);
            extrude(context, id + "F46", {"entities" : qUnion([Q0]), "operationType" : NewBodyOperationType.ADD, "depth" : 0.6 * mm});
        }
        {
            var Q0;
            Q0=qCreatedBy(makeId("Top.planeOp"),FACE);
            var sketch = newSketch(context, id + "F47", { "sketchPlane" : qUnion([Q0])});
            skLineSegment(sketch, "E903.bottom", {"start": v(-32.16, -19.74) * mm, "end": v(-31.86, -19.74) * mm});
            skLineSegment(sketch, "E903.top", {"start": v(-32.16, -29.43) * mm, "end": v(-31.86, -29.43) * mm});
            skLineSegment(sketch, "E903.left", {"start": v(-32.16, -19.74) * mm, "end": v(-32.16, -29.43) * mm});
            skLineSegment(sketch, "E903.right", {"start": v(-31.86, -19.74) * mm, "end": v(-31.86, -29.43) * mm});
            skLineSegment(sketch, "E904.bottom", {"start": v(-34.1, 3.13) * mm, "end": v(-31.72, 3.13) * mm});
            skLineSegment(sketch, "E904.top", {"start": v(-34.1, 0.35) * mm, "end": v(-31.72, 0.35) * mm});
            skLineSegment(sketch, "E904.left", {"start": v(-34.1, 3.13) * mm, "end": v(-34.1, 0.35) * mm});
            skLineSegment(sketch, "E904.right", {"start": v(-31.72, 3.13) * mm, "end": v(-31.72, 0.35) * mm});
            skLineSegment(sketch, "E905.bottom", {"start": v(-34.13, -7.9) * mm, "end": v(-31.72, -7.9) * mm});
            skLineSegment(sketch, "E905.top", {"start": v(-34.13, -10.8) * mm, "end": v(-31.72, -10.8) * mm});
            skLineSegment(sketch, "E905.left", {"start": v(-34.13, -7.9) * mm, "end": v(-34.13, -10.8) * mm});
            skLineSegment(sketch, "E905.right", {"start": v(-31.72, -7.9) * mm, "end": v(-31.72, -10.8) * mm});
            skSolve(sketch);
        }
        {
            var Q0;
            Q0=qSketchRegion(id+"F47",true);
            var Q1;
            Q1=makeQuery(id+"F35.boolean.opBoolean","MERGE",FACE,{"derivedFrom":[makeQuery(id+"F3.boolean.opBoolean","COPY",FACE,{"derivedFrom":makeQuery(id+"F3.opExtrude","SWEPT_FACE",FACE,{"disambiguationData":[OSD([sQuery(id+"F2.wireOp",EDGE,"E14")])]})}),makeQuery(id+"F35.opExtrude","CAP_FACE",FACE,{"disambiguationData":[OSD([sQuery(id+"F34.wireOp",EDGE,"E875")])],"isStart":false}),makeQuery(id+"F35.opExtrude","CAP_FACE",FACE,{"disambiguationData":[OSD([sQuery(id+"F34.wireOp",EDGE,"E876")])],"isStart":false})]});
            extrude(context, id + "F48", {"entities" : qUnion([Q0]), "operationType" : NewBodyOperationType.ADD, "endBound" : BoundingType.UP_TO_SURFACE, "endBoundEntityFace" : qUnion([Q1]), "depth" : 25 * mm});
        }
        {
            var Q0;
            Q0=makeQuery(id+"F35.boolean.opBoolean","MERGE",FACE,{"derivedFrom":[makeQuery(id+"F3.boolean.opBoolean","COPY",FACE,{"derivedFrom":makeQuery(id+"F3.opExtrude","SWEPT_FACE",FACE,{"disambiguationData":[OSD([sQuery(id+"F2.wireOp",EDGE,"E14")])]})}),makeQuery(id+"F35.opExtrude","CAP_FACE",FACE,{"disambiguationData":[OSD([sQuery(id+"F34.wireOp",EDGE,"E875")])],"isStart":false}),makeQuery(id+"F35.opExtrude","CAP_FACE",FACE,{"disambiguationData":[OSD([sQuery(id+"F34.wireOp",EDGE,"E876")])],"isStart":false})]});
            var sketch = newSketch(context, id + "F49", { "sketchPlane" : qUnion([Q0])});
            skText(sketch, "E906", { "text": "12v", "fontName": "OpenSans-Bold.ttf"});
            skText(sketch, "E907", { "text": "L3 L2 L1", "fontName": "OpenSans-Bold.ttf"});
            const initialGuessF49  = {"E906": [0.01715, 0.00103, 1, 0, 0.00547], "E907": [-0.01124, -0.00554, 1, 0, 0.00554]};
            skSetInitialGuess(sketch, initialGuessF49);
            skSolve(sketch);
        }
        {
            var Q0;
            Q0=qSketchRegion(id+"F49",true);
            extrude(context, id + "F50", {"entities" : qUnion([Q0]), "operationType" : NewBodyOperationType.REMOVE, "oppositeDirection" : true, "depth" : 0.9 * mm});
        }
        {
            var Q0;
            {var subQ1=sQuery(id+"F0.wireOp",EDGE,"E7.rect.top");var subQ2=sQuery(id+"F0.wireOp",EDGE,"E7.rect.right");var subQ9=makeQuery(id+"F1.opExtrude","SWEPT_FACE",FACE,{"disambiguationData":[OSD([subQ1])]});Q0=makeQuery(id+"F19.boolean.opBoolean","SPLIT",FACE,{"disambiguationData":[TD([makeQuery(id+"F1.opExtrude","SWEPT_FACE",FACE,{"disambiguationData":[OSD([subQ2])]})])],"derivedFrom":subQ9});}
            var sketch = newSketch(context, id + "F51", { "sketchPlane" : qUnion([Q0])});
            skText(sketch, "E908", { "text": "S2", "fontName": "OpenSans-Bold.ttf"});
            skText(sketch, "E909", { "text": "S3", "fontName": "OpenSans-Bold.ttf"});
            skText(sketch, "E910", { "text": "S1", "fontName": "OpenSans-Bold.ttf"});
            const initialGuessF51  = {"E908": [0.00543, 0.00629, 1, 0, 0.005], "E909": [-0.0147, 0.00046, 1, 0, 0.005], "E910": [0.02787, 0.00057, 1, 0, 0.005]};
            skSetInitialGuess(sketch, initialGuessF51);
            skSolve(sketch);
        }
        {
            var Q0;
            Q0=qSketchRegion(id+"F51",true);
            extrude(context, id + "F52", {"entities" : qUnion([Q0]), "operationType" : NewBodyOperationType.REMOVE, "depth" : 1 * mm, "hasSecondDirection" : true, "secondDirectionOppositeDirection" : true, "secondDirectionDepth" : 1 * mm});
        }
        {
            var Q0;
            {var subQ0=sQuery(id+"F2.wireOp",EDGE,"E22");var subQ1=sQuery(id+"F2.wireOp",EDGE,"E20");Q0=makeQuery(id+"F38.boolean.opBoolean","MERGE",FACE,{"derivedFrom":[makeQuery(id+"F24.boolean.opBoolean","SPLIT",FACE,{"disambiguationData":[TD([makeQuery(id+"F1.opExtrude","SWEPT_FACE",FACE,{"disambiguationData":[OSD([sQuery(id+"F0.wireOp",EDGE,"E3")])]})])],"derivedFrom":makeQuery(id+"F3.boolean.opBoolean","COPY",FACE,{"derivedFrom":makeQuery(id+"F3.opExtrude","SWEPT_FACE",FACE,{"disambiguationData":[OSD([subQ1,subQ0])]})})}),makeQuery(id+"F38.opExtrude","CAP_FACE",FACE,{"disambiguationData":[OSD([sQuery(id+"F37.wireOp",EDGE,"E877")])],"isStart":false}),makeQuery(id+"F38.opExtrude","CAP_FACE",FACE,{"disambiguationData":[OSD([sQuery(id+"F37.wireOp",EDGE,"E878")])],"isStart":false})]});}
            var sketch = newSketch(context, id + "F53", { "sketchPlane" : qUnion([Q0])});
            skText(sketch, "E911", { "text": "S6", "fontName": "OpenSans-Bold.ttf"});
            const initialGuessF53  = {"E911": [0.00536, -0.02288, 1, 0, 0.005]};
            skSetInitialGuess(sketch, initialGuessF53);
            skSolve(sketch);
        }
        {
            var Q0;
            Q0=qSketchRegion(id+"F53",true);
            var Q1;
            Q1=makeQuery(id+"F4.opFillet","BLEND_FACE",FACE,{"disambiguationData":[OSD([sQuery(id+"F0.wireOp",EDGE,"E7.rect.left"),sQuery(id+"F2.wireOp",EDGE,"E20"),sQuery(id+"F2.wireOp",EDGE,"E22")])]});
            extrude(context, id + "F54", {"entities" : qUnion([Q0]), "operationType" : NewBodyOperationType.REMOVE, "oppositeDirection" : true, "depth" : 1 * mm});
        }
        {
            var Q0;
            {var subQ1=sQuery(id+"F0.wireOp",EDGE,"E7.rect.left");var subQ3=sQuery(id+"F0.wireOp",EDGE,"E7.rect.bottom");Q0=makeQuery(id+"F9.boolean.opBoolean","SPLIT",FACE,{"disambiguationData":[TD([makeQuery(id+"F1.opExtrude","SWEPT_FACE",FACE,{"disambiguationData":[OSD([subQ3])]})])],"derivedFrom":makeQuery(id+"F1.opExtrude","SWEPT_FACE",FACE,{"disambiguationData":[OSD([subQ1])]})});}
            var sketch = newSketch(context, id + "F55", { "sketchPlane" : qUnion([Q0])});
            skText(sketch, "E912", { "text": "S5", "fontName": "OpenSans-Bold.ttf"});
            skText(sketch, "E913", { "text": "S4", "fontName": "OpenSans-Bold.ttf"});
            const initialGuessF55  = {"E912": [-0.03102, 0.00035, 1, 0, 0.00488], "E913": [0.00797, 0.0003, 1, 0, 0.0048]};
            skSetInitialGuess(sketch, initialGuessF55);
            skSolve(sketch);
        }
        {
            var Q0;
            Q0 = qSketchRegion(id + "F55", true);
            extrude(context, id + "F56", {"entities" : qUnion([Q0]), "operationType" : NewBodyOperationType.REMOVE, "oppositeDirection" : true, "depth" : 1 * mm});
        }
        {
            var Q0;
            {var subQ0=sQuery(id+"F12.wireOp",EDGE,"E53");Q0=makeQuery(id+"F12.imprint","IMPRINT",FACE,{"disambiguationData":[TD([[makeQuery(id+"F12.imprint","IMPRINT",EDGE,{"derivedFrom":subQ0}),-1.0]])]});}
            extrude(context, id + "F57", {"entities" : qUnion([Q0]), "operationType" : NewBodyOperationType.REMOVE, "oppositeDirection" : true, "depth" : 8 * mm});
        }
        {
            var Q0;
            Q0=makeQuery(id+"F0.imprint","IMPRINT",FACE,{"disambiguationData":[TD([[makeQuery(id+"F0.imprint","IMPRINT",EDGE,{"derivedFrom":sQuery(id+"F0.wireOp",EDGE,"E1")}),-1.0]])]});
            var sketch = newSketch(context, id + "F58", { "sketchPlane" : qUnion([Q0])});
            skPoint(sketch, "E914.first.point", {"position": v(6.62, 7.4) * mm});
            skPoint(sketch, "E914.second.point", {"position": v(6.67, 13.38) * mm});
            skPoint(sketch, "E914.third.point", {"position": v(3.73, 10.32) * mm});
            skPoint(sketch, "E915.first.point", {"position": v(17.45, 10.32) * mm});
            skPoint(sketch, "E915.second.point", {"position": v(14.7, 13.34) * mm});
            skPoint(sketch, "E915.third.point", {"position": v(14.7, 7.45) * mm});
            skPoint(sketch, "E916.MirrorP", {"position": v(17.5, 10.32) * mm});
            skPoint(sketch, "E917.MirrorP", {"position": v(14.62, 7.4) * mm});
            skPoint(sketch, "E918.MirrorP", {"position": v(14.57, 13.38) * mm});
            skLineSegment(sketch, "E919", {"start": v(14.46, 6.75) * mm, "end": v(6.63, 6.75) * mm});
            skLineSegment(sketch, "E920", {"start": v(14.66, 13.88) * mm, "end": v(6.96, 13.88) * mm});
            skArc(sketch, "E921.trimOffspring", {"start": v(6.96, 13.88) * mm, "mid": v(3.17, 10.38) * mm, "end": v(6.84, 6.75) * mm});
            skArc(sketch, "E922.trimOffspring", {"start": v(14.27, 13.88) * mm, "mid": v(18.08, 10.42) * mm, "end": v(14.46, 6.75) * mm});
            skPoint(sketch, "E923.orphan", {"position": v(14.5, 10.4) * mm});
            skPoint(sketch, "E924.start.orphan", {"position": v(10.62, 10.36) * mm});
            skCircle(sketch, "E925", {"center": v(6.74, 10.32) * mm, "radius": 2.01 * mm});
            skCircle(sketch, "E926", {"center": v(14.51, 10.32) * mm, "radius": 2.16 * mm});
            skLineSegment(sketch, "E927.trimOffspring", {"start": v(6.52, 13.88) * mm, "end": v(6.5, 13.88) * mm});
            skSolve(sketch);
        }
        {
            var Q0;
            Q0=qSketchRegion(id+"F58",true);
            extrude(context, id + "F59", {"entities" : qUnion([Q0]), "operationType" : NewBodyOperationType.REMOVE, "depth" : 8.2 * mm});
        }
    });
